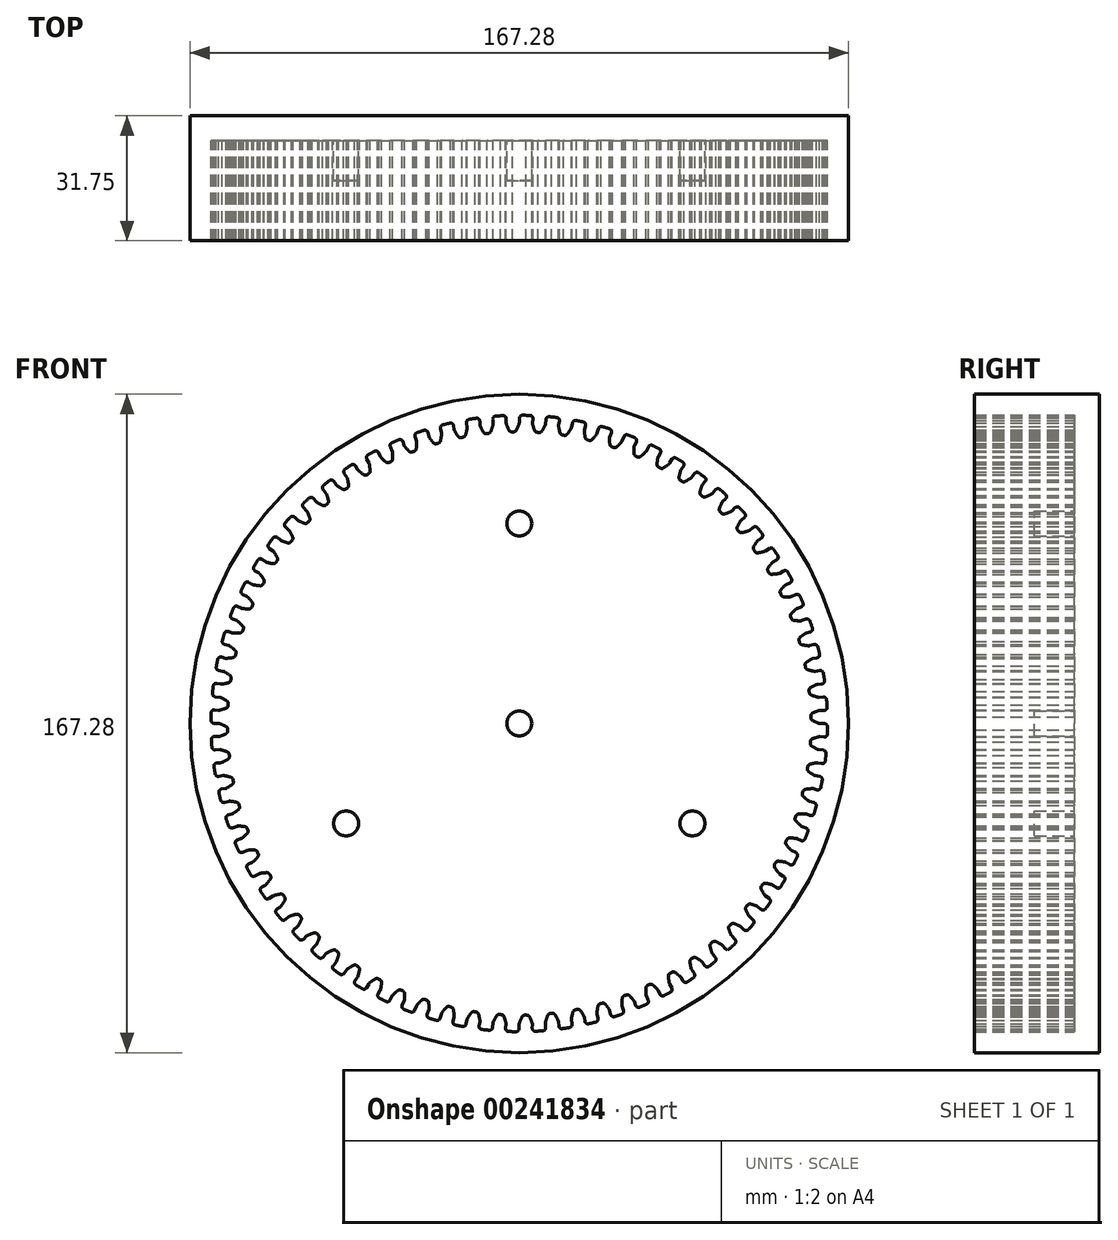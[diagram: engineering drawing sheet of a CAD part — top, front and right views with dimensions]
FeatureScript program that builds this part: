
annotation { "Feature Type Name" : "Feature", "Feature Type Description" : "" }
export const myFeature = defineFeature(function(context is Context, id is Id, definition is map)
    precondition{}
    {
        {
            var Q0;
            Q0=qCreatedBy(makeId("Front.planeOp"),FACE);
            var sketch = newSketch(context, id + "F0", { "sketchPlane" : qUnion([Q0])});
            skArc(sketch, "E0", {"start": v(-4.13, 78.2) * mm, "mid": v(-5.07, 78.15) * mm, "end": v(-6, 78.09) * mm});
            skLineSegment(sketch, "E1.MirrorCS", {"start": v(-3.32, 76.41) * mm, "end": v(-3.3, 77.4) * mm});
            skArc(sketch, "E2.MirrorCS", {"start": v(-3.28, 76.14) * mm, "mid": v(-2.99, 75.35) * mm, "end": v(-2.66, 74.57) * mm});
            skLineSegment(sketch, "E3.MirrorCS", {"start": v(-1.97, 74.1) * mm, "end": v(-1.7, 74.09) * mm});
            skLineSegment(sketch, "E4.MirrorCS", {"start": v(-1.44, 74.09) * mm, "end": v(-1.7, 74.09) * mm});
            skArc(sketch, "E5.MirrorCS", {"start": v(-0.05, 76.07) * mm, "mid": v(-0.38, 75.29) * mm, "end": v(-0.74, 74.52) * mm});
            skLineSegment(sketch, "E6.MirrorCS", {"start": v(0, 76.34) * mm, "end": v(0.03, 77.54) * mm});
            skPoint(sketch, "E7.visualSharp", {"position": v(-0.96, 74.09) * mm});
            skArc(sketch, "E7.filletArc", {"start": v(-1.44, 74.09) * mm, "mid": v(-1.03, 74.2) * mm, "end": v(-0.74, 74.52) * mm});
            skPoint(sketch, "E8.visualSharp", {"position": v(0, 76.2) * mm});
            skArc(sketch, "E8.filletArc", {"start": v(-0.05, 76.07) * mm, "mid": v(-0.01, 76.2) * mm, "end": v(0, 76.34) * mm});
            skPoint(sketch, "E9.visualSharp", {"position": v(-2.45, 74.12) * mm});
            skArc(sketch, "E9.filletArc", {"start": v(-2.66, 74.57) * mm, "mid": v(-2.38, 74.24) * mm, "end": v(-1.97, 74.1) * mm});
            skPoint(sketch, "E10.visualSharp", {"position": v(-3.32, 76.27) * mm});
            skArc(sketch, "E10.filletArc", {"start": v(-3.32, 76.41) * mm, "mid": v(-3.31, 76.27) * mm, "end": v(-3.28, 76.14) * mm});
            skPoint(sketch, "E11.visualSharp", {"position": v(0.05, 78.32) * mm});
            skArc(sketch, "E11.filletArc", {"start": v(0.82, 78.31) * mm, "mid": v(0.27, 78.1) * mm, "end": v(0.03, 77.54) * mm});
            skPoint(sketch, "E12.visualSharp", {"position": v(-3.28, 78.25) * mm});
            skArc(sketch, "E12.filletArc", {"start": v(-3.3, 77.4) * mm, "mid": v(-3.54, 77.99) * mm, "end": v(-4.13, 78.2) * mm});
            skArc(sketch, "E13.1.0", {"start": v(-6, 78.09) * mm, "mid": v(-6.54, 77.82) * mm, "end": v(-6.73, 77.25) * mm});
            skArc(sketch, "E13.1.1", {"start": v(-6.68, 75.77) * mm, "mid": v(-6.94, 74.97) * mm, "end": v(-7.23, 74.18) * mm});
            skLineSegment(sketch, "E13.1.2", {"start": v(-6.65, 76.05) * mm, "end": v(-6.73, 77.25) * mm});
            skArc(sketch, "E13.1.3", {"start": v(-6.68, 75.77) * mm, "mid": v(-6.65, 75.9) * mm, "end": v(-6.65, 76.05) * mm});
            skArc(sketch, "E13.1.4", {"start": v(-7.9, 73.68) * mm, "mid": v(-7.5, 73.83) * mm, "end": v(-7.23, 74.18) * mm});
            skLineSegment(sketch, "E13.1.5", {"start": v(-7.9, 73.68) * mm, "end": v(-8.16, 73.66) * mm});
            skLineSegment(sketch, "E13.1.6", {"start": v(-8.43, 73.65) * mm, "end": v(-8.16, 73.66) * mm});
            skArc(sketch, "E13.1.7", {"start": v(-9.15, 74.05) * mm, "mid": v(-8.84, 73.75) * mm, "end": v(-8.43, 73.65) * mm});
            skArc(sketch, "E13.1.8", {"start": v(-9.9, 75.56) * mm, "mid": v(-9.54, 74.8) * mm, "end": v(-9.15, 74.05) * mm});
            skArc(sketch, "E13.1.9", {"start": v(-9.97, 75.83) * mm, "mid": v(-9.95, 75.7) * mm, "end": v(-9.9, 75.56) * mm});
            skLineSegment(sketch, "E13.1.10", {"start": v(-9.97, 75.83) * mm, "end": v(-10.03, 76.82) * mm});
            skArc(sketch, "E13.1.11", {"start": v(-10.03, 76.82) * mm, "mid": v(-10.32, 77.38) * mm, "end": v(-10.93, 77.55) * mm});
            skArc(sketch, "E13.2.0", {"start": v(-12.79, 77.27) * mm, "mid": v(-13.3, 76.95) * mm, "end": v(-13.44, 76.37) * mm});
            skArc(sketch, "E13.2.1", {"start": v(-13.26, 74.9) * mm, "mid": v(-13.45, 74.08) * mm, "end": v(-13.67, 73.26) * mm});
            skLineSegment(sketch, "E13.2.2", {"start": v(-13.25, 75.18) * mm, "end": v(-13.44, 76.37) * mm});
            skArc(sketch, "E13.2.3", {"start": v(-13.26, 74.9) * mm, "mid": v(-13.24, 75.04) * mm, "end": v(-13.25, 75.18) * mm});
            skArc(sketch, "E13.2.4", {"start": v(-14.29, 72.71) * mm, "mid": v(-13.9, 72.9) * mm, "end": v(-13.67, 73.26) * mm});
            skLineSegment(sketch, "E13.2.5", {"start": v(-14.29, 72.71) * mm, "end": v(-14.55, 72.67) * mm});
            skLineSegment(sketch, "E13.2.6", {"start": v(-14.81, 72.63) * mm, "end": v(-14.55, 72.67) * mm});
            skArc(sketch, "E13.2.7", {"start": v(-15.57, 72.97) * mm, "mid": v(-15.24, 72.7) * mm, "end": v(-14.81, 72.63) * mm});
            skArc(sketch, "E13.2.8", {"start": v(-16.45, 74.41) * mm, "mid": v(-16.02, 73.68) * mm, "end": v(-15.57, 72.97) * mm});
            skArc(sketch, "E13.2.9", {"start": v(-16.54, 74.67) * mm, "mid": v(-16.5, 74.54) * mm, "end": v(-16.45, 74.41) * mm});
            skLineSegment(sketch, "E13.2.10", {"start": v(-16.54, 74.67) * mm, "end": v(-16.7, 75.66) * mm});
            skArc(sketch, "E13.2.11", {"start": v(-16.7, 75.66) * mm, "mid": v(-17.03, 76.19) * mm, "end": v(-17.65, 76.3) * mm});
            skArc(sketch, "E13.3.0", {"start": v(-19.47, 75.86) * mm, "mid": v(-19.95, 75.5) * mm, "end": v(-20.04, 74.9) * mm});
            skArc(sketch, "E13.3.1", {"start": v(-19.74, 73.46) * mm, "mid": v(-19.85, 72.63) * mm, "end": v(-20, 71.8) * mm});
            skLineSegment(sketch, "E13.3.2", {"start": v(-19.76, 73.74) * mm, "end": v(-20.04, 74.9) * mm});
            skArc(sketch, "E13.3.3", {"start": v(-19.74, 73.46) * mm, "mid": v(-19.73, 73.6) * mm, "end": v(-19.76, 73.74) * mm});
            skArc(sketch, "E13.3.4", {"start": v(-20.57, 71.2) * mm, "mid": v(-20.2, 71.41) * mm, "end": v(-20, 71.8) * mm});
            skLineSegment(sketch, "E13.3.5", {"start": v(-20.57, 71.2) * mm, "end": v(-20.83, 71.12) * mm});
            skLineSegment(sketch, "E13.3.6", {"start": v(-21.09, 71.06) * mm, "end": v(-20.83, 71.12) * mm});
            skArc(sketch, "E13.3.7", {"start": v(-21.87, 71.34) * mm, "mid": v(-21.52, 71.1) * mm, "end": v(-21.09, 71.06) * mm});
            skArc(sketch, "E13.3.8", {"start": v(-22.87, 72.7) * mm, "mid": v(-22.39, 72) * mm, "end": v(-21.87, 71.34) * mm});
            skArc(sketch, "E13.3.9", {"start": v(-22.98, 72.95) * mm, "mid": v(-22.94, 72.82) * mm, "end": v(-22.87, 72.7) * mm});
            skLineSegment(sketch, "E13.3.10", {"start": v(-22.98, 72.95) * mm, "end": v(-23.22, 73.91) * mm});
            skArc(sketch, "E13.3.11", {"start": v(-23.22, 73.91) * mm, "mid": v(-23.6, 74.41) * mm, "end": v(-24.23, 74.47) * mm});
            skArc(sketch, "E13.4.0", {"start": v(-26, 73.87) * mm, "mid": v(-26.46, 73.47) * mm, "end": v(-26.5, 72.88) * mm});
            skArc(sketch, "E13.4.1", {"start": v(-26.07, 71.46) * mm, "mid": v(-26.1, 70.62) * mm, "end": v(-26.18, 69.78) * mm});
            skLineSegment(sketch, "E13.4.2", {"start": v(-26.1, 71.74) * mm, "end": v(-26.5, 72.88) * mm});
            skArc(sketch, "E13.4.3", {"start": v(-26.07, 71.46) * mm, "mid": v(-26.07, 71.6) * mm, "end": v(-26.1, 71.74) * mm});
            skArc(sketch, "E13.4.4", {"start": v(-26.7, 69.13) * mm, "mid": v(-26.35, 69.38) * mm, "end": v(-26.18, 69.78) * mm});
            skLineSegment(sketch, "E13.4.5", {"start": v(-26.7, 69.13) * mm, "end": v(-26.95, 69.04) * mm});
            skLineSegment(sketch, "E13.4.6", {"start": v(-27.2, 68.96) * mm, "end": v(-26.95, 69.04) * mm});
            skArc(sketch, "E13.4.7", {"start": v(-28, 69.16) * mm, "mid": v(-27.63, 68.94) * mm, "end": v(-27.2, 68.96) * mm});
            skArc(sketch, "E13.4.8", {"start": v(-29.12, 70.43) * mm, "mid": v(-28.58, 69.78) * mm, "end": v(-28, 69.16) * mm});
            skArc(sketch, "E13.4.9", {"start": v(-29.25, 70.67) * mm, "mid": v(-29.2, 70.54) * mm, "end": v(-29.12, 70.43) * mm});
            skLineSegment(sketch, "E13.4.10", {"start": v(-29.25, 70.67) * mm, "end": v(-29.57, 71.6) * mm});
            skArc(sketch, "E13.4.11", {"start": v(-29.57, 71.6) * mm, "mid": v(-30, 72.07) * mm, "end": v(-30.63, 72.08) * mm});
            skArc(sketch, "E13.5.0", {"start": v(-32.35, 71.32) * mm, "mid": v(-32.76, 70.89) * mm, "end": v(-32.74, 70.29) * mm});
            skArc(sketch, "E13.5.1", {"start": v(-32.2, 68.92) * mm, "mid": v(-32.16, 68.08) * mm, "end": v(-32.16, 67.23) * mm});
            skLineSegment(sketch, "E13.5.2", {"start": v(-32.26, 69.19) * mm, "end": v(-32.74, 70.29) * mm});
            skArc(sketch, "E13.5.3", {"start": v(-32.2, 68.92) * mm, "mid": v(-32.21, 69.06) * mm, "end": v(-32.26, 69.19) * mm});
            skArc(sketch, "E13.5.4", {"start": v(-32.62, 66.54) * mm, "mid": v(-32.3, 66.82) * mm, "end": v(-32.16, 67.23) * mm});
            skLineSegment(sketch, "E13.5.5", {"start": v(-32.62, 66.54) * mm, "end": v(-32.86, 66.43) * mm});
            skLineSegment(sketch, "E13.5.6", {"start": v(-33.1, 66.32) * mm, "end": v(-32.86, 66.43) * mm});
            skArc(sketch, "E13.5.7", {"start": v(-33.92, 66.46) * mm, "mid": v(-33.53, 66.27) * mm, "end": v(-33.1, 66.32) * mm});
            skArc(sketch, "E13.5.8", {"start": v(-35.15, 67.62) * mm, "mid": v(-34.55, 67.02) * mm, "end": v(-33.92, 66.46) * mm});
            skArc(sketch, "E13.5.9", {"start": v(-35.3, 67.85) * mm, "mid": v(-35.24, 67.73) * mm, "end": v(-35.15, 67.62) * mm});
            skLineSegment(sketch, "E13.5.10", {"start": v(-35.3, 67.85) * mm, "end": v(-35.7, 68.76) * mm});
            skArc(sketch, "E13.5.11", {"start": v(-35.7, 68.76) * mm, "mid": v(-36.17, 69.18) * mm, "end": v(-36.8, 69.14) * mm});
            skArc(sketch, "E13.6.0", {"start": v(-38.44, 68.23) * mm, "mid": v(-38.81, 67.76) * mm, "end": v(-38.75, 67.17) * mm});
            skArc(sketch, "E13.6.1", {"start": v(-38.08, 65.85) * mm, "mid": v(-37.97, 65.01) * mm, "end": v(-37.9, 64.17) * mm});
            skLineSegment(sketch, "E13.6.2", {"start": v(-38.17, 66.11) * mm, "end": v(-38.75, 67.17) * mm});
            skArc(sketch, "E13.6.3", {"start": v(-38.08, 65.85) * mm, "mid": v(-38.11, 65.99) * mm, "end": v(-38.17, 66.11) * mm});
            skArc(sketch, "E13.6.4", {"start": v(-38.3, 63.44) * mm, "mid": v(-38, 63.75) * mm, "end": v(-37.9, 64.17) * mm});
            skLineSegment(sketch, "E13.6.5", {"start": v(-38.3, 63.44) * mm, "end": v(-38.52, 63.3) * mm});
            skLineSegment(sketch, "E13.6.6", {"start": v(-38.76, 63.19) * mm, "end": v(-38.52, 63.3) * mm});
            skArc(sketch, "E13.6.7", {"start": v(-39.59, 63.25) * mm, "mid": v(-39.18, 63.1) * mm, "end": v(-38.76, 63.19) * mm});
            skArc(sketch, "E13.6.8", {"start": v(-40.9, 64.3) * mm, "mid": v(-40.26, 63.76) * mm, "end": v(-39.59, 63.25) * mm});
            skArc(sketch, "E13.6.9", {"start": v(-41.08, 64.51) * mm, "mid": v(-41, 64.4) * mm, "end": v(-40.9, 64.3) * mm});
            skLineSegment(sketch, "E13.6.10", {"start": v(-41.08, 64.51) * mm, "end": v(-41.56, 65.38) * mm});
            skArc(sketch, "E13.6.11", {"start": v(-41.56, 65.38) * mm, "mid": v(-42.06, 65.77) * mm, "end": v(-42.68, 65.67) * mm});
            skArc(sketch, "E13.7.0", {"start": v(-44.24, 64.62) * mm, "mid": v(-44.57, 64.12) * mm, "end": v(-44.45, 63.54) * mm});
            skArc(sketch, "E13.7.1", {"start": v(-43.67, 62.28) * mm, "mid": v(-43.5, 61.46) * mm, "end": v(-43.35, 60.62) * mm});
            skLineSegment(sketch, "E13.7.2", {"start": v(-43.78, 62.53) * mm, "end": v(-44.45, 63.54) * mm});
            skArc(sketch, "E13.7.3", {"start": v(-43.67, 62.28) * mm, "mid": v(-43.72, 62.41) * mm, "end": v(-43.78, 62.53) * mm});
            skArc(sketch, "E13.7.4", {"start": v(-43.68, 59.86) * mm, "mid": v(-43.4, 60.2) * mm, "end": v(-43.35, 60.62) * mm});
            skLineSegment(sketch, "E13.7.5", {"start": v(-43.68, 59.86) * mm, "end": v(-43.9, 59.71) * mm});
            skLineSegment(sketch, "E13.7.6", {"start": v(-44.12, 59.57) * mm, "end": v(-43.9, 59.71) * mm});
            skArc(sketch, "E13.7.7", {"start": v(-44.95, 59.56) * mm, "mid": v(-44.53, 59.44) * mm, "end": v(-44.12, 59.57) * mm});
            skArc(sketch, "E13.7.8", {"start": v(-46.36, 60.49) * mm, "mid": v(-45.66, 60) * mm, "end": v(-44.95, 59.56) * mm});
            skArc(sketch, "E13.7.9", {"start": v(-46.55, 60.69) * mm, "mid": v(-46.46, 60.58) * mm, "end": v(-46.36, 60.49) * mm});
            skLineSegment(sketch, "E13.7.10", {"start": v(-46.55, 60.69) * mm, "end": v(-47.1, 61.51) * mm});
            skArc(sketch, "E13.7.11", {"start": v(-47.1, 61.51) * mm, "mid": v(-47.63, 61.85) * mm, "end": v(-48.24, 61.7) * mm});
            skArc(sketch, "E13.8.0", {"start": v(-49.7, 60.52) * mm, "mid": v(-49.99, 60) * mm, "end": v(-49.82, 59.42) * mm});
            skArc(sketch, "E13.8.1", {"start": v(-48.93, 58.24) * mm, "mid": v(-48.68, 57.43) * mm, "end": v(-48.47, 56.61) * mm});
            skLineSegment(sketch, "E13.8.2", {"start": v(-49.07, 58.48) * mm, "end": v(-49.82, 59.42) * mm});
            skArc(sketch, "E13.8.3", {"start": v(-48.93, 58.24) * mm, "mid": v(-49, 58.37) * mm, "end": v(-49.07, 58.48) * mm});
            skArc(sketch, "E13.8.4", {"start": v(-48.73, 55.83) * mm, "mid": v(-48.49, 56.18) * mm, "end": v(-48.47, 56.61) * mm});
            skLineSegment(sketch, "E13.8.5", {"start": v(-48.73, 55.83) * mm, "end": v(-48.93, 55.66) * mm});
            skLineSegment(sketch, "E13.8.6", {"start": v(-49.14, 55.5) * mm, "end": v(-48.93, 55.66) * mm});
            skArc(sketch, "E13.8.7", {"start": v(-49.97, 55.41) * mm, "mid": v(-49.54, 55.34) * mm, "end": v(-49.14, 55.5) * mm});
            skArc(sketch, "E13.8.8", {"start": v(-51.45, 56.22) * mm, "mid": v(-50.72, 55.8) * mm, "end": v(-49.97, 55.41) * mm});
            skArc(sketch, "E13.8.9", {"start": v(-51.66, 56.4) * mm, "mid": v(-51.56, 56.3) * mm, "end": v(-51.45, 56.22) * mm});
            skLineSegment(sketch, "E13.8.10", {"start": v(-51.66, 56.4) * mm, "end": v(-52.28, 57.17) * mm});
            skArc(sketch, "E13.8.11", {"start": v(-52.28, 57.17) * mm, "mid": v(-52.84, 57.47) * mm, "end": v(-53.43, 57.26) * mm});
            skArc(sketch, "E13.9.0", {"start": v(-54.8, 55.96) * mm, "mid": v(-55.03, 55.4) * mm, "end": v(-54.8, 54.85) * mm});
            skArc(sketch, "E13.9.1", {"start": v(-53.82, 53.75) * mm, "mid": v(-53.5, 52.97) * mm, "end": v(-53.22, 52.17) * mm});
            skLineSegment(sketch, "E13.9.2", {"start": v(-53.98, 53.98) * mm, "end": v(-54.8, 54.85) * mm});
            skArc(sketch, "E13.9.3", {"start": v(-53.82, 53.75) * mm, "mid": v(-53.9, 53.87) * mm, "end": v(-53.98, 53.98) * mm});
            skArc(sketch, "E13.9.4", {"start": v(-53.4, 51.37) * mm, "mid": v(-53.2, 51.74) * mm, "end": v(-53.22, 52.17) * mm});
            skLineSegment(sketch, "E13.9.5", {"start": v(-53.4, 51.37) * mm, "end": v(-53.6, 51.18) * mm});
            skLineSegment(sketch, "E13.9.6", {"start": v(-53.8, 51) * mm, "end": v(-53.6, 51.18) * mm});
            skArc(sketch, "E13.9.7", {"start": v(-54.6, 50.85) * mm, "mid": v(-54.18, 50.8) * mm, "end": v(-53.8, 51) * mm});
            skArc(sketch, "E13.9.8", {"start": v(-56.16, 51.52) * mm, "mid": v(-55.39, 51.17) * mm, "end": v(-54.6, 50.85) * mm});
            skArc(sketch, "E13.9.9", {"start": v(-56.38, 51.68) * mm, "mid": v(-56.27, 51.6) * mm, "end": v(-56.16, 51.52) * mm});
            skLineSegment(sketch, "E13.9.10", {"start": v(-56.38, 51.68) * mm, "end": v(-57.07, 52.4) * mm});
            skArc(sketch, "E13.9.11", {"start": v(-57.07, 52.4) * mm, "mid": v(-57.65, 52.64) * mm, "end": v(-58.22, 52.38) * mm});
            skArc(sketch, "E13.10.0", {"start": v(-59.46, 50.97) * mm, "mid": v(-59.65, 50.4) * mm, "end": v(-59.38, 49.87) * mm});
            skArc(sketch, "E13.10.1", {"start": v(-58.3, 48.86) * mm, "mid": v(-57.92, 48.1) * mm, "end": v(-57.56, 47.34) * mm});
            skLineSegment(sketch, "E13.10.2", {"start": v(-58.48, 49.07) * mm, "end": v(-59.38, 49.87) * mm});
            skArc(sketch, "E13.10.3", {"start": v(-58.3, 48.86) * mm, "mid": v(-58.38, 48.97) * mm, "end": v(-58.48, 49.07) * mm});
            skArc(sketch, "E13.10.4", {"start": v(-57.68, 46.52) * mm, "mid": v(-57.5, 46.91) * mm, "end": v(-57.56, 47.34) * mm});
            skLineSegment(sketch, "E13.10.5", {"start": v(-57.68, 46.52) * mm, "end": v(-57.85, 46.31) * mm});
            skLineSegment(sketch, "E13.10.6", {"start": v(-58.03, 46.12) * mm, "end": v(-57.85, 46.31) * mm});
            skArc(sketch, "E13.10.7", {"start": v(-58.83, 45.9) * mm, "mid": v(-58.4, 45.9) * mm, "end": v(-58.03, 46.12) * mm});
            skArc(sketch, "E13.10.8", {"start": v(-60.43, 46.43) * mm, "mid": v(-59.64, 46.14) * mm, "end": v(-58.83, 45.9) * mm});
            skArc(sketch, "E13.10.9", {"start": v(-60.67, 46.57) * mm, "mid": v(-60.56, 46.5) * mm, "end": v(-60.43, 46.43) * mm});
            skLineSegment(sketch, "E13.10.10", {"start": v(-60.67, 46.57) * mm, "end": v(-61.42, 47.23) * mm});
            skArc(sketch, "E13.10.11", {"start": v(-61.42, 47.23) * mm, "mid": v(-62.02, 47.42) * mm, "end": v(-62.56, 47.1) * mm});
            skArc(sketch, "E13.11.0", {"start": v(-63.68, 45.6) * mm, "mid": v(-63.81, 45.01) * mm, "end": v(-63.5, 44.5) * mm});
            skArc(sketch, "E13.11.1", {"start": v(-62.34, 43.59) * mm, "mid": v(-61.89, 42.87) * mm, "end": v(-61.47, 42.14) * mm});
            skLineSegment(sketch, "E13.11.2", {"start": v(-62.53, 43.79) * mm, "end": v(-63.5, 44.5) * mm});
            skArc(sketch, "E13.11.3", {"start": v(-62.34, 43.59) * mm, "mid": v(-62.43, 43.7) * mm, "end": v(-62.53, 43.79) * mm});
            skArc(sketch, "E13.11.4", {"start": v(-61.52, 41.31) * mm, "mid": v(-61.38, 41.72) * mm, "end": v(-61.47, 42.14) * mm});
            skLineSegment(sketch, "E13.11.5", {"start": v(-61.52, 41.31) * mm, "end": v(-61.67, 41.1) * mm});
            skLineSegment(sketch, "E13.11.6", {"start": v(-61.83, 40.89) * mm, "end": v(-61.67, 41.1) * mm});
            skArc(sketch, "E13.11.7", {"start": v(-62.6, 40.6) * mm, "mid": v(-62.18, 40.63) * mm, "end": v(-61.83, 40.89) * mm});
            skArc(sketch, "E13.11.8", {"start": v(-64.25, 40.99) * mm, "mid": v(-63.43, 40.77) * mm, "end": v(-62.6, 40.6) * mm});
            skArc(sketch, "E13.11.9", {"start": v(-64.5, 41.1) * mm, "mid": v(-64.38, 41.04) * mm, "end": v(-64.25, 40.99) * mm});
            skLineSegment(sketch, "E13.11.10", {"start": v(-64.5, 41.1) * mm, "end": v(-65.3, 41.7) * mm});
            skArc(sketch, "E13.11.11", {"start": v(-65.3, 41.7) * mm, "mid": v(-65.91, 41.83) * mm, "end": v(-66.43, 41.48) * mm});
            skArc(sketch, "E13.12.0", {"start": v(-67.4, 39.87) * mm, "mid": v(-67.5, 39.28) * mm, "end": v(-67.14, 38.8) * mm});
            skArc(sketch, "E13.12.1", {"start": v(-65.9, 37.99) * mm, "mid": v(-65.4, 37.32) * mm, "end": v(-64.9, 36.62) * mm});
            skLineSegment(sketch, "E13.12.2", {"start": v(-66.1, 38.17) * mm, "end": v(-67.14, 38.8) * mm});
            skArc(sketch, "E13.12.3", {"start": v(-65.9, 37.99) * mm, "mid": v(-66, 38.09) * mm, "end": v(-66.1, 38.17) * mm});
            skArc(sketch, "E13.12.4", {"start": v(-64.88, 35.8) * mm, "mid": v(-64.78, 36.21) * mm, "end": v(-64.9, 36.62) * mm});
            skLineSegment(sketch, "E13.12.5", {"start": v(-64.88, 35.8) * mm, "end": v(-65.02, 35.56) * mm});
            skLineSegment(sketch, "E13.12.6", {"start": v(-65.16, 35.34) * mm, "end": v(-65.02, 35.56) * mm});
            skArc(sketch, "E13.12.7", {"start": v(-65.9, 34.98) * mm, "mid": v(-65.48, 35.05) * mm, "end": v(-65.16, 35.34) * mm});
            skArc(sketch, "E13.12.8", {"start": v(-67.58, 35.23) * mm, "mid": v(-66.74, 35.09) * mm, "end": v(-65.9, 34.98) * mm});
            skArc(sketch, "E13.12.9", {"start": v(-67.83, 35.33) * mm, "mid": v(-67.71, 35.27) * mm, "end": v(-67.58, 35.23) * mm});
            skLineSegment(sketch, "E13.12.10", {"start": v(-67.83, 35.33) * mm, "end": v(-68.68, 35.85) * mm});
            skArc(sketch, "E13.12.11", {"start": v(-68.68, 35.85) * mm, "mid": v(-69.3, 35.93) * mm, "end": v(-69.8, 35.53) * mm});
            skArc(sketch, "E13.13.0", {"start": v(-70.63, 33.84) * mm, "mid": v(-70.66, 33.25) * mm, "end": v(-70.26, 32.8) * mm});
            skArc(sketch, "E13.13.1", {"start": v(-68.96, 32.1) * mm, "mid": v(-68.4, 31.48) * mm, "end": v(-67.85, 30.83) * mm});
            skLineSegment(sketch, "E13.13.2", {"start": v(-69.19, 32.26) * mm, "end": v(-70.26, 32.8) * mm});
            skArc(sketch, "E13.13.3", {"start": v(-68.96, 32.1) * mm, "mid": v(-69.07, 32.2) * mm, "end": v(-69.19, 32.26) * mm});
            skArc(sketch, "E13.13.4", {"start": v(-67.76, 30) * mm, "mid": v(-67.69, 30.43) * mm, "end": v(-67.85, 30.83) * mm});
            skLineSegment(sketch, "E13.13.5", {"start": v(-67.76, 30) * mm, "end": v(-67.87, 29.76) * mm});
            skLineSegment(sketch, "E13.13.6", {"start": v(-68, 29.53) * mm, "end": v(-67.87, 29.76) * mm});
            skArc(sketch, "E13.13.7", {"start": v(-68.7, 29.1) * mm, "mid": v(-68.29, 29.21) * mm, "end": v(-68, 29.53) * mm});
            skArc(sketch, "E13.13.8", {"start": v(-70.4, 29.2) * mm, "mid": v(-69.55, 29.14) * mm, "end": v(-68.7, 29.1) * mm});
            skArc(sketch, "E13.13.9", {"start": v(-70.66, 29.28) * mm, "mid": v(-70.53, 29.23) * mm, "end": v(-70.4, 29.2) * mm});
            skLineSegment(sketch, "E13.13.10", {"start": v(-70.66, 29.28) * mm, "end": v(-71.55, 29.72) * mm});
            skArc(sketch, "E13.13.11", {"start": v(-71.55, 29.72) * mm, "mid": v(-72.18, 29.75) * mm, "end": v(-72.62, 29.31) * mm});
            skArc(sketch, "E13.14.0", {"start": v(-73.3, 27.56) * mm, "mid": v(-73.29, 26.96) * mm, "end": v(-72.86, 26.55) * mm});
            skArc(sketch, "E13.14.1", {"start": v(-71.5, 25.97) * mm, "mid": v(-70.88, 25.4) * mm, "end": v(-70.28, 24.8) * mm});
            skLineSegment(sketch, "E13.14.2", {"start": v(-71.73, 26.11) * mm, "end": v(-72.86, 26.55) * mm});
            skArc(sketch, "E13.14.3", {"start": v(-71.5, 25.97) * mm, "mid": v(-71.6, 26.05) * mm, "end": v(-71.73, 26.11) * mm});
            skArc(sketch, "E13.14.4", {"start": v(-70.11, 23.98) * mm, "mid": v(-70.08, 24.41) * mm, "end": v(-70.28, 24.8) * mm});
            skLineSegment(sketch, "E13.14.5", {"start": v(-70.11, 23.98) * mm, "end": v(-70.2, 23.73) * mm});
            skLineSegment(sketch, "E13.14.6", {"start": v(-70.3, 23.49) * mm, "end": v(-70.2, 23.73) * mm});
            skArc(sketch, "E13.14.7", {"start": v(-70.98, 23) * mm, "mid": v(-70.57, 23.15) * mm, "end": v(-70.3, 23.49) * mm});
            skArc(sketch, "E13.14.8", {"start": v(-72.67, 22.96) * mm, "mid": v(-71.82, 22.96) * mm, "end": v(-70.98, 23) * mm});
            skArc(sketch, "E13.14.9", {"start": v(-72.94, 23.01) * mm, "mid": v(-72.8, 22.98) * mm, "end": v(-72.67, 22.96) * mm});
            skLineSegment(sketch, "E13.14.10", {"start": v(-72.94, 23.01) * mm, "end": v(-73.86, 23.37) * mm});
            skArc(sketch, "E13.14.11", {"start": v(-73.86, 23.37) * mm, "mid": v(-74.5, 23.35) * mm, "end": v(-74.9, 22.87) * mm});
            skArc(sketch, "E13.15.0", {"start": v(-75.43, 21.07) * mm, "mid": v(-75.36, 20.47) * mm, "end": v(-74.9, 20.1) * mm});
            skArc(sketch, "E13.15.1", {"start": v(-73.49, 19.64) * mm, "mid": v(-72.82, 19.12) * mm, "end": v(-72.18, 18.58) * mm});
            skLineSegment(sketch, "E13.15.2", {"start": v(-73.74, 19.76) * mm, "end": v(-74.9, 20.1) * mm});
            skArc(sketch, "E13.15.3", {"start": v(-73.49, 19.64) * mm, "mid": v(-73.6, 19.71) * mm, "end": v(-73.74, 19.76) * mm});
            skArc(sketch, "E13.15.4", {"start": v(-71.94, 17.78) * mm, "mid": v(-71.94, 18.21) * mm, "end": v(-72.18, 18.58) * mm});
            skLineSegment(sketch, "E13.15.5", {"start": v(-71.94, 17.78) * mm, "end": v(-72, 17.53) * mm});
            skLineSegment(sketch, "E13.15.6", {"start": v(-72.09, 17.27) * mm, "end": v(-72, 17.53) * mm});
            skArc(sketch, "E13.15.7", {"start": v(-72.71, 16.73) * mm, "mid": v(-72.32, 16.91) * mm, "end": v(-72.09, 17.27) * mm});
            skArc(sketch, "E13.15.8", {"start": v(-74.4, 16.54) * mm, "mid": v(-73.55, 16.62) * mm, "end": v(-72.71, 16.73) * mm});
            skArc(sketch, "E13.15.9", {"start": v(-74.67, 16.57) * mm, "mid": v(-74.53, 16.54) * mm, "end": v(-74.4, 16.54) * mm});
            skLineSegment(sketch, "E13.15.10", {"start": v(-74.67, 16.57) * mm, "end": v(-75.62, 16.85) * mm});
            skArc(sketch, "E13.15.11", {"start": v(-75.62, 16.85) * mm, "mid": v(-76.25, 16.77) * mm, "end": v(-76.61, 16.25) * mm});
            skArc(sketch, "E13.16.0", {"start": v(-76.98, 14.41) * mm, "mid": v(-76.86, 13.83) * mm, "end": v(-76.36, 13.5) * mm});
            skArc(sketch, "E13.16.1", {"start": v(-74.92, 13.16) * mm, "mid": v(-74.21, 12.7) * mm, "end": v(-73.52, 12.21) * mm});
            skLineSegment(sketch, "E13.16.2", {"start": v(-75.18, 13.26) * mm, "end": v(-76.36, 13.5) * mm});
            skArc(sketch, "E13.16.3", {"start": v(-74.92, 13.16) * mm, "mid": v(-75.05, 13.22) * mm, "end": v(-75.18, 13.26) * mm});
            skArc(sketch, "E13.16.4", {"start": v(-73.21, 11.44) * mm, "mid": v(-73.26, 11.87) * mm, "end": v(-73.52, 12.21) * mm});
            skLineSegment(sketch, "E13.16.5", {"start": v(-73.21, 11.44) * mm, "end": v(-73.26, 11.18) * mm});
            skLineSegment(sketch, "E13.16.6", {"start": v(-73.32, 10.92) * mm, "end": v(-73.26, 11.18) * mm});
            skArc(sketch, "E13.16.7", {"start": v(-73.9, 10.33) * mm, "mid": v(-73.52, 10.54) * mm, "end": v(-73.32, 10.92) * mm});
            skArc(sketch, "E13.16.8", {"start": v(-75.55, 10) * mm, "mid": v(-74.72, 10.14) * mm, "end": v(-73.9, 10.33) * mm});
            skArc(sketch, "E13.16.9", {"start": v(-75.83, 10) * mm, "mid": v(-75.69, 9.98) * mm, "end": v(-75.55, 10) * mm});
            skLineSegment(sketch, "E13.16.10", {"start": v(-75.83, 10) * mm, "end": v(-76.8, 10.2) * mm});
            skArc(sketch, "E13.16.11", {"start": v(-76.8, 10.2) * mm, "mid": v(-77.42, 10.06) * mm, "end": v(-77.74, 9.52) * mm});
            skArc(sketch, "E13.17.0", {"start": v(-77.94, 7.65) * mm, "mid": v(-77.77, 7.07) * mm, "end": v(-77.24, 6.79) * mm});
            skArc(sketch, "E13.17.1", {"start": v(-75.78, 6.58) * mm, "mid": v(-75.04, 6.19) * mm, "end": v(-74.3, 5.76) * mm});
            skLineSegment(sketch, "E13.17.2", {"start": v(-76.05, 6.66) * mm, "end": v(-77.24, 6.79) * mm});
            skArc(sketch, "E13.17.3", {"start": v(-75.78, 6.58) * mm, "mid": v(-75.91, 6.63) * mm, "end": v(-76.05, 6.66) * mm});
            skArc(sketch, "E13.17.4", {"start": v(-73.93, 5.02) * mm, "mid": v(-74.01, 5.44) * mm, "end": v(-74.3, 5.76) * mm});
            skLineSegment(sketch, "E13.17.5", {"start": v(-73.93, 5.02) * mm, "end": v(-73.96, 4.76) * mm});
            skLineSegment(sketch, "E13.17.6", {"start": v(-74, 4.5) * mm, "end": v(-73.96, 4.76) * mm});
            skArc(sketch, "E13.17.7", {"start": v(-74.51, 3.85) * mm, "mid": v(-74.16, 4.1) * mm, "end": v(-74, 4.5) * mm});
            skArc(sketch, "E13.17.8", {"start": v(-76.13, 3.37) * mm, "mid": v(-75.32, 3.6) * mm, "end": v(-74.51, 3.85) * mm});
            skArc(sketch, "E13.17.9", {"start": v(-76.4, 3.35) * mm, "mid": v(-76.27, 3.35) * mm, "end": v(-76.13, 3.37) * mm});
            skLineSegment(sketch, "E13.17.10", {"start": v(-76.4, 3.35) * mm, "end": v(-77.4, 3.46) * mm});
            skArc(sketch, "E13.17.11", {"start": v(-77.4, 3.46) * mm, "mid": v(-78, 3.27) * mm, "end": v(-78.27, 2.7) * mm});
            skArc(sketch, "E13.18.0", {"start": v(-78.31, 0.82) * mm, "mid": v(-78.1, 0.27) * mm, "end": v(-77.54, 0.03) * mm});
            skArc(sketch, "E13.18.1", {"start": v(-76.07, -0.05) * mm, "mid": v(-75.29, -0.38) * mm, "end": v(-74.52, -0.74) * mm});
            skLineSegment(sketch, "E13.18.2", {"start": v(-76.34, 0) * mm, "end": v(-77.54, 0.03) * mm});
            skArc(sketch, "E13.18.3", {"start": v(-76.07, -0.05) * mm, "mid": v(-76.2, -0.01) * mm, "end": v(-76.34, 0) * mm});
            skArc(sketch, "E13.18.4", {"start": v(-74.09, -1.44) * mm, "mid": v(-74.2, -1.03) * mm, "end": v(-74.52, -0.74) * mm});
            skLineSegment(sketch, "E13.18.5", {"start": v(-74.09, -1.44) * mm, "end": v(-74.09, -1.7) * mm});
            skLineSegment(sketch, "E13.18.6", {"start": v(-74.1, -1.97) * mm, "end": v(-74.09, -1.7) * mm});
            skArc(sketch, "E13.18.7", {"start": v(-74.57, -2.66) * mm, "mid": v(-74.24, -2.38) * mm, "end": v(-74.1, -1.97) * mm});
            skArc(sketch, "E13.18.8", {"start": v(-76.14, -3.28) * mm, "mid": v(-75.35, -2.99) * mm, "end": v(-74.57, -2.66) * mm});
            skArc(sketch, "E13.18.9", {"start": v(-76.41, -3.32) * mm, "mid": v(-76.27, -3.31) * mm, "end": v(-76.14, -3.28) * mm});
            skLineSegment(sketch, "E13.18.10", {"start": v(-76.41, -3.32) * mm, "end": v(-77.4, -3.3) * mm});
            skArc(sketch, "E13.18.11", {"start": v(-77.4, -3.3) * mm, "mid": v(-77.99, -3.54) * mm, "end": v(-78.2, -4.13) * mm});
            skArc(sketch, "E13.19.0", {"start": v(-78.09, -6) * mm, "mid": v(-77.82, -6.54) * mm, "end": v(-77.25, -6.73) * mm});
            skArc(sketch, "E13.19.1", {"start": v(-75.77, -6.68) * mm, "mid": v(-74.97, -6.94) * mm, "end": v(-74.18, -7.23) * mm});
            skLineSegment(sketch, "E13.19.2", {"start": v(-76.05, -6.65) * mm, "end": v(-77.25, -6.73) * mm});
            skArc(sketch, "E13.19.3", {"start": v(-75.77, -6.68) * mm, "mid": v(-75.9, -6.65) * mm, "end": v(-76.05, -6.65) * mm});
            skArc(sketch, "E13.19.4", {"start": v(-73.68, -7.9) * mm, "mid": v(-73.83, -7.5) * mm, "end": v(-74.18, -7.23) * mm});
            skLineSegment(sketch, "E13.19.5", {"start": v(-73.68, -7.9) * mm, "end": v(-73.66, -8.16) * mm});
            skLineSegment(sketch, "E13.19.6", {"start": v(-73.65, -8.43) * mm, "end": v(-73.66, -8.16) * mm});
            skArc(sketch, "E13.19.7", {"start": v(-74.05, -9.15) * mm, "mid": v(-73.75, -8.84) * mm, "end": v(-73.65, -8.43) * mm});
            skArc(sketch, "E13.19.8", {"start": v(-75.56, -9.9) * mm, "mid": v(-74.8, -9.54) * mm, "end": v(-74.05, -9.15) * mm});
            skArc(sketch, "E13.19.9", {"start": v(-75.83, -9.97) * mm, "mid": v(-75.7, -9.95) * mm, "end": v(-75.56, -9.9) * mm});
            skLineSegment(sketch, "E13.19.10", {"start": v(-75.83, -9.97) * mm, "end": v(-76.82, -10.03) * mm});
            skArc(sketch, "E13.19.11", {"start": v(-76.82, -10.03) * mm, "mid": v(-77.38, -10.32) * mm, "end": v(-77.55, -10.93) * mm});
            skArc(sketch, "E13.20.0", {"start": v(-77.27, -12.79) * mm, "mid": v(-76.95, -13.3) * mm, "end": v(-76.37, -13.44) * mm});
            skArc(sketch, "E13.20.1", {"start": v(-74.9, -13.26) * mm, "mid": v(-74.08, -13.45) * mm, "end": v(-73.26, -13.67) * mm});
            skLineSegment(sketch, "E13.20.2", {"start": v(-75.18, -13.25) * mm, "end": v(-76.37, -13.44) * mm});
            skArc(sketch, "E13.20.3", {"start": v(-74.9, -13.26) * mm, "mid": v(-75.04, -13.24) * mm, "end": v(-75.18, -13.25) * mm});
            skArc(sketch, "E13.20.4", {"start": v(-72.71, -14.29) * mm, "mid": v(-72.9, -13.9) * mm, "end": v(-73.26, -13.67) * mm});
            skLineSegment(sketch, "E13.20.5", {"start": v(-72.71, -14.29) * mm, "end": v(-72.67, -14.55) * mm});
            skLineSegment(sketch, "E13.20.6", {"start": v(-72.63, -14.81) * mm, "end": v(-72.67, -14.55) * mm});
            skArc(sketch, "E13.20.7", {"start": v(-72.97, -15.57) * mm, "mid": v(-72.7, -15.24) * mm, "end": v(-72.63, -14.81) * mm});
            skArc(sketch, "E13.20.8", {"start": v(-74.41, -16.45) * mm, "mid": v(-73.68, -16.02) * mm, "end": v(-72.97, -15.57) * mm});
            skArc(sketch, "E13.20.9", {"start": v(-74.67, -16.54) * mm, "mid": v(-74.54, -16.5) * mm, "end": v(-74.41, -16.45) * mm});
            skLineSegment(sketch, "E13.20.10", {"start": v(-74.67, -16.54) * mm, "end": v(-75.66, -16.7) * mm});
            skArc(sketch, "E13.20.11", {"start": v(-75.66, -16.7) * mm, "mid": v(-76.19, -17.03) * mm, "end": v(-76.3, -17.65) * mm});
            skArc(sketch, "E13.21.0", {"start": v(-75.86, -19.47) * mm, "mid": v(-75.5, -19.95) * mm, "end": v(-74.9, -20.04) * mm});
            skArc(sketch, "E13.21.1", {"start": v(-73.46, -19.74) * mm, "mid": v(-72.63, -19.85) * mm, "end": v(-71.8, -20) * mm});
            skLineSegment(sketch, "E13.21.2", {"start": v(-73.74, -19.76) * mm, "end": v(-74.9, -20.04) * mm});
            skArc(sketch, "E13.21.3", {"start": v(-73.46, -19.74) * mm, "mid": v(-73.6, -19.73) * mm, "end": v(-73.74, -19.76) * mm});
            skArc(sketch, "E13.21.4", {"start": v(-71.2, -20.57) * mm, "mid": v(-71.41, -20.2) * mm, "end": v(-71.8, -20) * mm});
            skLineSegment(sketch, "E13.21.5", {"start": v(-71.2, -20.57) * mm, "end": v(-71.12, -20.83) * mm});
            skLineSegment(sketch, "E13.21.6", {"start": v(-71.06, -21.09) * mm, "end": v(-71.12, -20.83) * mm});
            skArc(sketch, "E13.21.7", {"start": v(-71.34, -21.87) * mm, "mid": v(-71.1, -21.52) * mm, "end": v(-71.06, -21.09) * mm});
            skArc(sketch, "E13.21.8", {"start": v(-72.7, -22.87) * mm, "mid": v(-72, -22.39) * mm, "end": v(-71.34, -21.87) * mm});
            skArc(sketch, "E13.21.9", {"start": v(-72.95, -22.98) * mm, "mid": v(-72.82, -22.94) * mm, "end": v(-72.7, -22.87) * mm});
            skLineSegment(sketch, "E13.21.10", {"start": v(-72.95, -22.98) * mm, "end": v(-73.91, -23.22) * mm});
            skArc(sketch, "E13.21.11", {"start": v(-73.91, -23.22) * mm, "mid": v(-74.41, -23.6) * mm, "end": v(-74.47, -24.23) * mm});
            skArc(sketch, "E13.22.0", {"start": v(-73.87, -26) * mm, "mid": v(-73.47, -26.46) * mm, "end": v(-72.88, -26.5) * mm});
            skArc(sketch, "E13.22.1", {"start": v(-71.46, -26.07) * mm, "mid": v(-70.62, -26.1) * mm, "end": v(-69.78, -26.18) * mm});
            skLineSegment(sketch, "E13.22.2", {"start": v(-71.74, -26.1) * mm, "end": v(-72.88, -26.5) * mm});
            skArc(sketch, "E13.22.3", {"start": v(-71.46, -26.07) * mm, "mid": v(-71.6, -26.07) * mm, "end": v(-71.74, -26.1) * mm});
            skArc(sketch, "E13.22.4", {"start": v(-69.13, -26.7) * mm, "mid": v(-69.38, -26.35) * mm, "end": v(-69.78, -26.18) * mm});
            skLineSegment(sketch, "E13.22.5", {"start": v(-69.13, -26.7) * mm, "end": v(-69.04, -26.95) * mm});
            skLineSegment(sketch, "E13.22.6", {"start": v(-68.96, -27.2) * mm, "end": v(-69.04, -26.95) * mm});
            skArc(sketch, "E13.22.7", {"start": v(-69.16, -28) * mm, "mid": v(-68.94, -27.63) * mm, "end": v(-68.96, -27.2) * mm});
            skArc(sketch, "E13.22.8", {"start": v(-70.43, -29.12) * mm, "mid": v(-69.78, -28.58) * mm, "end": v(-69.16, -28) * mm});
            skArc(sketch, "E13.22.9", {"start": v(-70.67, -29.25) * mm, "mid": v(-70.54, -29.2) * mm, "end": v(-70.43, -29.12) * mm});
            skLineSegment(sketch, "E13.22.10", {"start": v(-70.67, -29.25) * mm, "end": v(-71.6, -29.57) * mm});
            skArc(sketch, "E13.22.11", {"start": v(-71.6, -29.57) * mm, "mid": v(-72.07, -30) * mm, "end": v(-72.08, -30.63) * mm});
            skArc(sketch, "E13.23.0", {"start": v(-71.32, -32.35) * mm, "mid": v(-70.89, -32.76) * mm, "end": v(-70.29, -32.74) * mm});
            skArc(sketch, "E13.23.1", {"start": v(-68.92, -32.2) * mm, "mid": v(-68.08, -32.16) * mm, "end": v(-67.23, -32.16) * mm});
            skLineSegment(sketch, "E13.23.2", {"start": v(-69.19, -32.26) * mm, "end": v(-70.29, -32.74) * mm});
            skArc(sketch, "E13.23.3", {"start": v(-68.92, -32.2) * mm, "mid": v(-69.06, -32.21) * mm, "end": v(-69.19, -32.26) * mm});
            skArc(sketch, "E13.23.4", {"start": v(-66.54, -32.62) * mm, "mid": v(-66.82, -32.3) * mm, "end": v(-67.23, -32.16) * mm});
            skLineSegment(sketch, "E13.23.5", {"start": v(-66.54, -32.62) * mm, "end": v(-66.43, -32.86) * mm});
            skLineSegment(sketch, "E13.23.6", {"start": v(-66.32, -33.1) * mm, "end": v(-66.43, -32.86) * mm});
            skArc(sketch, "E13.23.7", {"start": v(-66.46, -33.92) * mm, "mid": v(-66.27, -33.53) * mm, "end": v(-66.32, -33.1) * mm});
            skArc(sketch, "E13.23.8", {"start": v(-67.62, -35.15) * mm, "mid": v(-67.02, -34.55) * mm, "end": v(-66.46, -33.92) * mm});
            skArc(sketch, "E13.23.9", {"start": v(-67.85, -35.3) * mm, "mid": v(-67.73, -35.24) * mm, "end": v(-67.62, -35.15) * mm});
            skLineSegment(sketch, "E13.23.10", {"start": v(-67.85, -35.3) * mm, "end": v(-68.76, -35.7) * mm});
            skArc(sketch, "E13.23.11", {"start": v(-68.76, -35.7) * mm, "mid": v(-69.18, -36.17) * mm, "end": v(-69.14, -36.8) * mm});
            skArc(sketch, "E13.24.0", {"start": v(-68.23, -38.44) * mm, "mid": v(-67.76, -38.81) * mm, "end": v(-67.17, -38.75) * mm});
            skArc(sketch, "E13.24.1", {"start": v(-65.85, -38.08) * mm, "mid": v(-65.01, -37.97) * mm, "end": v(-64.17, -37.9) * mm});
            skLineSegment(sketch, "E13.24.2", {"start": v(-66.11, -38.17) * mm, "end": v(-67.17, -38.75) * mm});
            skArc(sketch, "E13.24.3", {"start": v(-65.85, -38.08) * mm, "mid": v(-65.99, -38.11) * mm, "end": v(-66.11, -38.17) * mm});
            skArc(sketch, "E13.24.4", {"start": v(-63.44, -38.3) * mm, "mid": v(-63.75, -38) * mm, "end": v(-64.17, -37.9) * mm});
            skLineSegment(sketch, "E13.24.5", {"start": v(-63.44, -38.3) * mm, "end": v(-63.3, -38.52) * mm});
            skLineSegment(sketch, "E13.24.6", {"start": v(-63.19, -38.76) * mm, "end": v(-63.3, -38.52) * mm});
            skArc(sketch, "E13.24.7", {"start": v(-63.25, -39.59) * mm, "mid": v(-63.1, -39.18) * mm, "end": v(-63.19, -38.76) * mm});
            skArc(sketch, "E13.24.8", {"start": v(-64.3, -40.9) * mm, "mid": v(-63.76, -40.26) * mm, "end": v(-63.25, -39.59) * mm});
            skArc(sketch, "E13.24.9", {"start": v(-64.51, -41.08) * mm, "mid": v(-64.4, -41) * mm, "end": v(-64.3, -40.9) * mm});
            skLineSegment(sketch, "E13.24.10", {"start": v(-64.51, -41.08) * mm, "end": v(-65.38, -41.56) * mm});
            skArc(sketch, "E13.24.11", {"start": v(-65.38, -41.56) * mm, "mid": v(-65.77, -42.06) * mm, "end": v(-65.67, -42.68) * mm});
            skArc(sketch, "E13.25.0", {"start": v(-64.62, -44.24) * mm, "mid": v(-64.12, -44.57) * mm, "end": v(-63.54, -44.45) * mm});
            skArc(sketch, "E13.25.1", {"start": v(-62.28, -43.67) * mm, "mid": v(-61.46, -43.5) * mm, "end": v(-60.62, -43.35) * mm});
            skLineSegment(sketch, "E13.25.2", {"start": v(-62.53, -43.78) * mm, "end": v(-63.54, -44.45) * mm});
            skArc(sketch, "E13.25.3", {"start": v(-62.28, -43.67) * mm, "mid": v(-62.41, -43.72) * mm, "end": v(-62.53, -43.78) * mm});
            skArc(sketch, "E13.25.4", {"start": v(-59.86, -43.68) * mm, "mid": v(-60.2, -43.4) * mm, "end": v(-60.62, -43.35) * mm});
            skLineSegment(sketch, "E13.25.5", {"start": v(-59.86, -43.68) * mm, "end": v(-59.71, -43.9) * mm});
            skLineSegment(sketch, "E13.25.6", {"start": v(-59.57, -44.12) * mm, "end": v(-59.71, -43.9) * mm});
            skArc(sketch, "E13.25.7", {"start": v(-59.56, -44.95) * mm, "mid": v(-59.44, -44.53) * mm, "end": v(-59.57, -44.12) * mm});
            skArc(sketch, "E13.25.8", {"start": v(-60.49, -46.36) * mm, "mid": v(-60, -45.66) * mm, "end": v(-59.56, -44.95) * mm});
            skArc(sketch, "E13.25.9", {"start": v(-60.69, -46.55) * mm, "mid": v(-60.58, -46.46) * mm, "end": v(-60.49, -46.36) * mm});
            skLineSegment(sketch, "E13.25.10", {"start": v(-60.69, -46.55) * mm, "end": v(-61.51, -47.1) * mm});
            skArc(sketch, "E13.25.11", {"start": v(-61.51, -47.1) * mm, "mid": v(-61.85, -47.63) * mm, "end": v(-61.7, -48.24) * mm});
            skArc(sketch, "E13.26.0", {"start": v(-60.52, -49.7) * mm, "mid": v(-60, -49.99) * mm, "end": v(-59.42, -49.82) * mm});
            skArc(sketch, "E13.26.1", {"start": v(-58.24, -48.93) * mm, "mid": v(-57.43, -48.68) * mm, "end": v(-56.61, -48.47) * mm});
            skLineSegment(sketch, "E13.26.2", {"start": v(-58.48, -49.07) * mm, "end": v(-59.42, -49.82) * mm});
            skArc(sketch, "E13.26.3", {"start": v(-58.24, -48.93) * mm, "mid": v(-58.37, -49) * mm, "end": v(-58.48, -49.07) * mm});
            skArc(sketch, "E13.26.4", {"start": v(-55.83, -48.73) * mm, "mid": v(-56.18, -48.49) * mm, "end": v(-56.61, -48.47) * mm});
            skLineSegment(sketch, "E13.26.5", {"start": v(-55.83, -48.73) * mm, "end": v(-55.66, -48.93) * mm});
            skLineSegment(sketch, "E13.26.6", {"start": v(-55.5, -49.14) * mm, "end": v(-55.66, -48.93) * mm});
            skArc(sketch, "E13.26.7", {"start": v(-55.41, -49.97) * mm, "mid": v(-55.34, -49.54) * mm, "end": v(-55.5, -49.14) * mm});
            skArc(sketch, "E13.26.8", {"start": v(-56.22, -51.45) * mm, "mid": v(-55.8, -50.72) * mm, "end": v(-55.41, -49.97) * mm});
            skArc(sketch, "E13.26.9", {"start": v(-56.4, -51.66) * mm, "mid": v(-56.3, -51.56) * mm, "end": v(-56.22, -51.45) * mm});
            skLineSegment(sketch, "E13.26.10", {"start": v(-56.4, -51.66) * mm, "end": v(-57.17, -52.28) * mm});
            skArc(sketch, "E13.26.11", {"start": v(-57.17, -52.28) * mm, "mid": v(-57.47, -52.84) * mm, "end": v(-57.26, -53.43) * mm});
            skArc(sketch, "E13.27.0", {"start": v(-55.96, -54.8) * mm, "mid": v(-55.4, -55.03) * mm, "end": v(-54.85, -54.8) * mm});
            skArc(sketch, "E13.27.1", {"start": v(-53.75, -53.82) * mm, "mid": v(-52.97, -53.5) * mm, "end": v(-52.17, -53.22) * mm});
            skLineSegment(sketch, "E13.27.2", {"start": v(-53.98, -53.98) * mm, "end": v(-54.85, -54.8) * mm});
            skArc(sketch, "E13.27.3", {"start": v(-53.75, -53.82) * mm, "mid": v(-53.87, -53.9) * mm, "end": v(-53.98, -53.98) * mm});
            skArc(sketch, "E13.27.4", {"start": v(-51.37, -53.4) * mm, "mid": v(-51.74, -53.2) * mm, "end": v(-52.17, -53.22) * mm});
            skLineSegment(sketch, "E13.27.5", {"start": v(-51.37, -53.4) * mm, "end": v(-51.18, -53.6) * mm});
            skLineSegment(sketch, "E13.27.6", {"start": v(-51, -53.8) * mm, "end": v(-51.18, -53.6) * mm});
            skArc(sketch, "E13.27.7", {"start": v(-50.85, -54.6) * mm, "mid": v(-50.8, -54.18) * mm, "end": v(-51, -53.8) * mm});
            skArc(sketch, "E13.27.8", {"start": v(-51.52, -56.16) * mm, "mid": v(-51.17, -55.39) * mm, "end": v(-50.85, -54.6) * mm});
            skArc(sketch, "E13.27.9", {"start": v(-51.68, -56.38) * mm, "mid": v(-51.6, -56.27) * mm, "end": v(-51.52, -56.16) * mm});
            skLineSegment(sketch, "E13.27.10", {"start": v(-51.68, -56.38) * mm, "end": v(-52.4, -57.07) * mm});
            skArc(sketch, "E13.27.11", {"start": v(-52.4, -57.07) * mm, "mid": v(-52.64, -57.65) * mm, "end": v(-52.38, -58.22) * mm});
            skArc(sketch, "E13.28.0", {"start": v(-50.97, -59.46) * mm, "mid": v(-50.4, -59.65) * mm, "end": v(-49.87, -59.38) * mm});
            skArc(sketch, "E13.28.1", {"start": v(-48.86, -58.3) * mm, "mid": v(-48.1, -57.92) * mm, "end": v(-47.34, -57.56) * mm});
            skLineSegment(sketch, "E13.28.2", {"start": v(-49.07, -58.48) * mm, "end": v(-49.87, -59.38) * mm});
            skArc(sketch, "E13.28.3", {"start": v(-48.86, -58.3) * mm, "mid": v(-48.97, -58.38) * mm, "end": v(-49.07, -58.48) * mm});
            skArc(sketch, "E13.28.4", {"start": v(-46.52, -57.68) * mm, "mid": v(-46.91, -57.5) * mm, "end": v(-47.34, -57.56) * mm});
            skLineSegment(sketch, "E13.28.5", {"start": v(-46.52, -57.68) * mm, "end": v(-46.31, -57.85) * mm});
            skLineSegment(sketch, "E13.28.6", {"start": v(-46.12, -58.03) * mm, "end": v(-46.31, -57.85) * mm});
            skArc(sketch, "E13.28.7", {"start": v(-45.9, -58.83) * mm, "mid": v(-45.9, -58.4) * mm, "end": v(-46.12, -58.03) * mm});
            skArc(sketch, "E13.28.8", {"start": v(-46.43, -60.43) * mm, "mid": v(-46.14, -59.64) * mm, "end": v(-45.9, -58.83) * mm});
            skArc(sketch, "E13.28.9", {"start": v(-46.57, -60.67) * mm, "mid": v(-46.5, -60.56) * mm, "end": v(-46.43, -60.43) * mm});
            skLineSegment(sketch, "E13.28.10", {"start": v(-46.57, -60.67) * mm, "end": v(-47.23, -61.42) * mm});
            skArc(sketch, "E13.28.11", {"start": v(-47.23, -61.42) * mm, "mid": v(-47.42, -62.02) * mm, "end": v(-47.1, -62.56) * mm});
            skArc(sketch, "E13.29.0", {"start": v(-45.6, -63.68) * mm, "mid": v(-45.01, -63.81) * mm, "end": v(-44.5, -63.5) * mm});
            skArc(sketch, "E13.29.1", {"start": v(-43.59, -62.34) * mm, "mid": v(-42.87, -61.89) * mm, "end": v(-42.14, -61.47) * mm});
            skLineSegment(sketch, "E13.29.2", {"start": v(-43.79, -62.53) * mm, "end": v(-44.5, -63.5) * mm});
            skArc(sketch, "E13.29.3", {"start": v(-43.59, -62.34) * mm, "mid": v(-43.7, -62.43) * mm, "end": v(-43.79, -62.53) * mm});
            skArc(sketch, "E13.29.4", {"start": v(-41.31, -61.52) * mm, "mid": v(-41.72, -61.38) * mm, "end": v(-42.14, -61.47) * mm});
            skLineSegment(sketch, "E13.29.5", {"start": v(-41.31, -61.52) * mm, "end": v(-41.1, -61.67) * mm});
            skLineSegment(sketch, "E13.29.6", {"start": v(-40.89, -61.83) * mm, "end": v(-41.1, -61.67) * mm});
            skArc(sketch, "E13.29.7", {"start": v(-40.6, -62.6) * mm, "mid": v(-40.63, -62.18) * mm, "end": v(-40.89, -61.83) * mm});
            skArc(sketch, "E13.29.8", {"start": v(-40.99, -64.25) * mm, "mid": v(-40.77, -63.43) * mm, "end": v(-40.6, -62.6) * mm});
            skArc(sketch, "E13.29.9", {"start": v(-41.1, -64.5) * mm, "mid": v(-41.04, -64.38) * mm, "end": v(-40.99, -64.25) * mm});
            skLineSegment(sketch, "E13.29.10", {"start": v(-41.1, -64.5) * mm, "end": v(-41.7, -65.3) * mm});
            skArc(sketch, "E13.29.11", {"start": v(-41.7, -65.3) * mm, "mid": v(-41.83, -65.91) * mm, "end": v(-41.48, -66.43) * mm});
            skArc(sketch, "E13.30.0", {"start": v(-39.87, -67.4) * mm, "mid": v(-39.28, -67.5) * mm, "end": v(-38.8, -67.14) * mm});
            skArc(sketch, "E13.30.1", {"start": v(-37.99, -65.9) * mm, "mid": v(-37.32, -65.4) * mm, "end": v(-36.62, -64.9) * mm});
            skLineSegment(sketch, "E13.30.2", {"start": v(-38.17, -66.1) * mm, "end": v(-38.8, -67.14) * mm});
            skArc(sketch, "E13.30.3", {"start": v(-37.99, -65.9) * mm, "mid": v(-38.09, -66) * mm, "end": v(-38.17, -66.1) * mm});
            skArc(sketch, "E13.30.4", {"start": v(-35.8, -64.88) * mm, "mid": v(-36.21, -64.78) * mm, "end": v(-36.62, -64.9) * mm});
            skLineSegment(sketch, "E13.30.5", {"start": v(-35.8, -64.88) * mm, "end": v(-35.56, -65.02) * mm});
            skLineSegment(sketch, "E13.30.6", {"start": v(-35.34, -65.16) * mm, "end": v(-35.56, -65.02) * mm});
            skArc(sketch, "E13.30.7", {"start": v(-34.98, -65.9) * mm, "mid": v(-35.05, -65.48) * mm, "end": v(-35.34, -65.16) * mm});
            skArc(sketch, "E13.30.8", {"start": v(-35.23, -67.58) * mm, "mid": v(-35.09, -66.74) * mm, "end": v(-34.98, -65.9) * mm});
            skArc(sketch, "E13.30.9", {"start": v(-35.33, -67.83) * mm, "mid": v(-35.27, -67.71) * mm, "end": v(-35.23, -67.58) * mm});
            skLineSegment(sketch, "E13.30.10", {"start": v(-35.33, -67.83) * mm, "end": v(-35.85, -68.68) * mm});
            skArc(sketch, "E13.30.11", {"start": v(-35.85, -68.68) * mm, "mid": v(-35.93, -69.3) * mm, "end": v(-35.53, -69.8) * mm});
            skArc(sketch, "E13.31.0", {"start": v(-33.84, -70.63) * mm, "mid": v(-33.25, -70.66) * mm, "end": v(-32.8, -70.26) * mm});
            skArc(sketch, "E13.31.1", {"start": v(-32.1, -68.96) * mm, "mid": v(-31.48, -68.4) * mm, "end": v(-30.83, -67.85) * mm});
            skLineSegment(sketch, "E13.31.2", {"start": v(-32.26, -69.19) * mm, "end": v(-32.8, -70.26) * mm});
            skArc(sketch, "E13.31.3", {"start": v(-32.1, -68.96) * mm, "mid": v(-32.2, -69.07) * mm, "end": v(-32.26, -69.19) * mm});
            skArc(sketch, "E13.31.4", {"start": v(-30, -67.76) * mm, "mid": v(-30.43, -67.69) * mm, "end": v(-30.83, -67.85) * mm});
            skLineSegment(sketch, "E13.31.5", {"start": v(-30, -67.76) * mm, "end": v(-29.76, -67.87) * mm});
            skLineSegment(sketch, "E13.31.6", {"start": v(-29.53, -68) * mm, "end": v(-29.76, -67.87) * mm});
            skArc(sketch, "E13.31.7", {"start": v(-29.1, -68.7) * mm, "mid": v(-29.21, -68.29) * mm, "end": v(-29.53, -68) * mm});
            skArc(sketch, "E13.31.8", {"start": v(-29.2, -70.4) * mm, "mid": v(-29.14, -69.55) * mm, "end": v(-29.1, -68.7) * mm});
            skArc(sketch, "E13.31.9", {"start": v(-29.28, -70.66) * mm, "mid": v(-29.23, -70.53) * mm, "end": v(-29.2, -70.4) * mm});
            skLineSegment(sketch, "E13.31.10", {"start": v(-29.28, -70.66) * mm, "end": v(-29.72, -71.55) * mm});
            skArc(sketch, "E13.31.11", {"start": v(-29.72, -71.55) * mm, "mid": v(-29.75, -72.18) * mm, "end": v(-29.31, -72.62) * mm});
            skArc(sketch, "E13.32.0", {"start": v(-27.56, -73.3) * mm, "mid": v(-26.96, -73.29) * mm, "end": v(-26.55, -72.86) * mm});
            skArc(sketch, "E13.32.1", {"start": v(-25.97, -71.5) * mm, "mid": v(-25.4, -70.88) * mm, "end": v(-24.8, -70.28) * mm});
            skLineSegment(sketch, "E13.32.2", {"start": v(-26.11, -71.73) * mm, "end": v(-26.55, -72.86) * mm});
            skArc(sketch, "E13.32.3", {"start": v(-25.97, -71.5) * mm, "mid": v(-26.05, -71.6) * mm, "end": v(-26.11, -71.73) * mm});
            skArc(sketch, "E13.32.4", {"start": v(-23.98, -70.11) * mm, "mid": v(-24.41, -70.08) * mm, "end": v(-24.8, -70.28) * mm});
            skLineSegment(sketch, "E13.32.5", {"start": v(-23.98, -70.11) * mm, "end": v(-23.73, -70.2) * mm});
            skLineSegment(sketch, "E13.32.6", {"start": v(-23.49, -70.3) * mm, "end": v(-23.73, -70.2) * mm});
            skArc(sketch, "E13.32.7", {"start": v(-23, -70.98) * mm, "mid": v(-23.15, -70.57) * mm, "end": v(-23.49, -70.3) * mm});
            skArc(sketch, "E13.32.8", {"start": v(-22.96, -72.67) * mm, "mid": v(-22.96, -71.82) * mm, "end": v(-23, -70.98) * mm});
            skArc(sketch, "E13.32.9", {"start": v(-23.01, -72.94) * mm, "mid": v(-22.98, -72.8) * mm, "end": v(-22.96, -72.67) * mm});
            skLineSegment(sketch, "E13.32.10", {"start": v(-23.01, -72.94) * mm, "end": v(-23.37, -73.86) * mm});
            skArc(sketch, "E13.32.11", {"start": v(-23.37, -73.86) * mm, "mid": v(-23.35, -74.5) * mm, "end": v(-22.87, -74.9) * mm});
            skArc(sketch, "E13.33.0", {"start": v(-21.07, -75.43) * mm, "mid": v(-20.47, -75.36) * mm, "end": v(-20.1, -74.9) * mm});
            skArc(sketch, "E13.33.1", {"start": v(-19.64, -73.49) * mm, "mid": v(-19.12, -72.82) * mm, "end": v(-18.58, -72.18) * mm});
            skLineSegment(sketch, "E13.33.2", {"start": v(-19.76, -73.74) * mm, "end": v(-20.1, -74.9) * mm});
            skArc(sketch, "E13.33.3", {"start": v(-19.64, -73.49) * mm, "mid": v(-19.71, -73.6) * mm, "end": v(-19.76, -73.74) * mm});
            skArc(sketch, "E13.33.4", {"start": v(-17.78, -71.94) * mm, "mid": v(-18.21, -71.94) * mm, "end": v(-18.58, -72.18) * mm});
            skLineSegment(sketch, "E13.33.5", {"start": v(-17.78, -71.94) * mm, "end": v(-17.53, -72) * mm});
            skLineSegment(sketch, "E13.33.6", {"start": v(-17.27, -72.09) * mm, "end": v(-17.53, -72) * mm});
            skArc(sketch, "E13.33.7", {"start": v(-16.73, -72.71) * mm, "mid": v(-16.91, -72.32) * mm, "end": v(-17.27, -72.09) * mm});
            skArc(sketch, "E13.33.8", {"start": v(-16.54, -74.4) * mm, "mid": v(-16.62, -73.55) * mm, "end": v(-16.73, -72.71) * mm});
            skArc(sketch, "E13.33.9", {"start": v(-16.57, -74.67) * mm, "mid": v(-16.54, -74.53) * mm, "end": v(-16.54, -74.4) * mm});
            skLineSegment(sketch, "E13.33.10", {"start": v(-16.57, -74.67) * mm, "end": v(-16.85, -75.62) * mm});
            skArc(sketch, "E13.33.11", {"start": v(-16.85, -75.62) * mm, "mid": v(-16.77, -76.25) * mm, "end": v(-16.25, -76.61) * mm});
            skArc(sketch, "E13.34.0", {"start": v(-14.41, -76.98) * mm, "mid": v(-13.83, -76.86) * mm, "end": v(-13.5, -76.36) * mm});
            skArc(sketch, "E13.34.1", {"start": v(-13.16, -74.92) * mm, "mid": v(-12.7, -74.21) * mm, "end": v(-12.21, -73.52) * mm});
            skLineSegment(sketch, "E13.34.2", {"start": v(-13.26, -75.18) * mm, "end": v(-13.5, -76.36) * mm});
            skArc(sketch, "E13.34.3", {"start": v(-13.16, -74.92) * mm, "mid": v(-13.22, -75.05) * mm, "end": v(-13.26, -75.18) * mm});
            skArc(sketch, "E13.34.4", {"start": v(-11.44, -73.21) * mm, "mid": v(-11.87, -73.26) * mm, "end": v(-12.21, -73.52) * mm});
            skLineSegment(sketch, "E13.34.5", {"start": v(-11.44, -73.21) * mm, "end": v(-11.18, -73.26) * mm});
            skLineSegment(sketch, "E13.34.6", {"start": v(-10.92, -73.32) * mm, "end": v(-11.18, -73.26) * mm});
            skArc(sketch, "E13.34.7", {"start": v(-10.33, -73.9) * mm, "mid": v(-10.54, -73.52) * mm, "end": v(-10.92, -73.32) * mm});
            skArc(sketch, "E13.34.8", {"start": v(-10, -75.55) * mm, "mid": v(-10.14, -74.72) * mm, "end": v(-10.33, -73.9) * mm});
            skArc(sketch, "E13.34.9", {"start": v(-10, -75.83) * mm, "mid": v(-9.98, -75.69) * mm, "end": v(-10, -75.55) * mm});
            skLineSegment(sketch, "E13.34.10", {"start": v(-10, -75.83) * mm, "end": v(-10.2, -76.8) * mm});
            skArc(sketch, "E13.34.11", {"start": v(-10.2, -76.8) * mm, "mid": v(-10.06, -77.42) * mm, "end": v(-9.52, -77.74) * mm});
            skArc(sketch, "E13.35.0", {"start": v(-7.65, -77.94) * mm, "mid": v(-7.07, -77.77) * mm, "end": v(-6.79, -77.24) * mm});
            skArc(sketch, "E13.35.1", {"start": v(-6.58, -75.78) * mm, "mid": v(-6.19, -75.04) * mm, "end": v(-5.76, -74.3) * mm});
            skLineSegment(sketch, "E13.35.2", {"start": v(-6.66, -76.05) * mm, "end": v(-6.79, -77.24) * mm});
            skArc(sketch, "E13.35.3", {"start": v(-6.58, -75.78) * mm, "mid": v(-6.63, -75.91) * mm, "end": v(-6.66, -76.05) * mm});
            skArc(sketch, "E13.35.4", {"start": v(-5.02, -73.93) * mm, "mid": v(-5.44, -74.01) * mm, "end": v(-5.76, -74.3) * mm});
            skLineSegment(sketch, "E13.35.5", {"start": v(-5.02, -73.93) * mm, "end": v(-4.76, -73.96) * mm});
            skLineSegment(sketch, "E13.35.6", {"start": v(-4.5, -74) * mm, "end": v(-4.76, -73.96) * mm});
            skArc(sketch, "E13.35.7", {"start": v(-3.85, -74.51) * mm, "mid": v(-4.1, -74.16) * mm, "end": v(-4.5, -74) * mm});
            skArc(sketch, "E13.35.8", {"start": v(-3.37, -76.13) * mm, "mid": v(-3.6, -75.32) * mm, "end": v(-3.85, -74.51) * mm});
            skArc(sketch, "E13.35.9", {"start": v(-3.35, -76.4) * mm, "mid": v(-3.35, -76.27) * mm, "end": v(-3.37, -76.13) * mm});
            skLineSegment(sketch, "E13.35.10", {"start": v(-3.35, -76.4) * mm, "end": v(-3.46, -77.4) * mm});
            skArc(sketch, "E13.35.11", {"start": v(-3.46, -77.4) * mm, "mid": v(-3.27, -78) * mm, "end": v(-2.7, -78.27) * mm});
            skArc(sketch, "E13.36.0", {"start": v(-0.82, -78.31) * mm, "mid": v(-0.27, -78.1) * mm, "end": v(-0.03, -77.54) * mm});
            skArc(sketch, "E13.36.1", {"start": v(0.05, -76.07) * mm, "mid": v(0.38, -75.29) * mm, "end": v(0.74, -74.52) * mm});
            skLineSegment(sketch, "E13.36.2", {"start": v(0, -76.34) * mm, "end": v(-0.03, -77.54) * mm});
            skArc(sketch, "E13.36.3", {"start": v(0.05, -76.07) * mm, "mid": v(0.01, -76.2) * mm, "end": v(0, -76.34) * mm});
            skArc(sketch, "E13.36.4", {"start": v(1.44, -74.09) * mm, "mid": v(1.03, -74.2) * mm, "end": v(0.74, -74.52) * mm});
            skLineSegment(sketch, "E13.36.5", {"start": v(1.44, -74.09) * mm, "end": v(1.7, -74.09) * mm});
            skLineSegment(sketch, "E13.36.6", {"start": v(1.97, -74.1) * mm, "end": v(1.7, -74.09) * mm});
            skArc(sketch, "E13.36.7", {"start": v(2.66, -74.57) * mm, "mid": v(2.38, -74.24) * mm, "end": v(1.97, -74.1) * mm});
            skArc(sketch, "E13.36.8", {"start": v(3.28, -76.14) * mm, "mid": v(2.99, -75.35) * mm, "end": v(2.66, -74.57) * mm});
            skArc(sketch, "E13.36.9", {"start": v(3.32, -76.41) * mm, "mid": v(3.31, -76.27) * mm, "end": v(3.28, -76.14) * mm});
            skLineSegment(sketch, "E13.36.10", {"start": v(3.32, -76.41) * mm, "end": v(3.3, -77.4) * mm});
            skArc(sketch, "E13.36.11", {"start": v(3.3, -77.4) * mm, "mid": v(3.54, -77.99) * mm, "end": v(4.13, -78.2) * mm});
            skArc(sketch, "E13.37.0", {"start": v(6, -78.09) * mm, "mid": v(6.54, -77.82) * mm, "end": v(6.73, -77.25) * mm});
            skArc(sketch, "E13.37.1", {"start": v(6.68, -75.77) * mm, "mid": v(6.94, -74.97) * mm, "end": v(7.23, -74.18) * mm});
            skLineSegment(sketch, "E13.37.2", {"start": v(6.65, -76.05) * mm, "end": v(6.73, -77.25) * mm});
            skArc(sketch, "E13.37.3", {"start": v(6.68, -75.77) * mm, "mid": v(6.65, -75.9) * mm, "end": v(6.65, -76.05) * mm});
            skArc(sketch, "E13.37.4", {"start": v(7.9, -73.68) * mm, "mid": v(7.5, -73.83) * mm, "end": v(7.23, -74.18) * mm});
            skLineSegment(sketch, "E13.37.5", {"start": v(7.9, -73.68) * mm, "end": v(8.16, -73.66) * mm});
            skLineSegment(sketch, "E13.37.6", {"start": v(8.43, -73.65) * mm, "end": v(8.16, -73.66) * mm});
            skArc(sketch, "E13.37.7", {"start": v(9.15, -74.05) * mm, "mid": v(8.84, -73.75) * mm, "end": v(8.43, -73.65) * mm});
            skArc(sketch, "E13.37.8", {"start": v(9.9, -75.56) * mm, "mid": v(9.54, -74.8) * mm, "end": v(9.15, -74.05) * mm});
            skArc(sketch, "E13.37.9", {"start": v(9.97, -75.83) * mm, "mid": v(9.95, -75.7) * mm, "end": v(9.9, -75.56) * mm});
            skLineSegment(sketch, "E13.37.10", {"start": v(9.97, -75.83) * mm, "end": v(10.03, -76.82) * mm});
            skArc(sketch, "E13.37.11", {"start": v(10.03, -76.82) * mm, "mid": v(10.32, -77.38) * mm, "end": v(10.93, -77.55) * mm});
            skArc(sketch, "E13.38.0", {"start": v(12.79, -77.27) * mm, "mid": v(13.3, -76.95) * mm, "end": v(13.44, -76.37) * mm});
            skArc(sketch, "E13.38.1", {"start": v(13.26, -74.9) * mm, "mid": v(13.45, -74.08) * mm, "end": v(13.67, -73.26) * mm});
            skLineSegment(sketch, "E13.38.2", {"start": v(13.25, -75.18) * mm, "end": v(13.44, -76.37) * mm});
            skArc(sketch, "E13.38.3", {"start": v(13.26, -74.9) * mm, "mid": v(13.24, -75.04) * mm, "end": v(13.25, -75.18) * mm});
            skArc(sketch, "E13.38.4", {"start": v(14.29, -72.71) * mm, "mid": v(13.9, -72.9) * mm, "end": v(13.67, -73.26) * mm});
            skLineSegment(sketch, "E13.38.5", {"start": v(14.29, -72.71) * mm, "end": v(14.55, -72.67) * mm});
            skLineSegment(sketch, "E13.38.6", {"start": v(14.81, -72.63) * mm, "end": v(14.55, -72.67) * mm});
            skArc(sketch, "E13.38.7", {"start": v(15.57, -72.97) * mm, "mid": v(15.24, -72.7) * mm, "end": v(14.81, -72.63) * mm});
            skArc(sketch, "E13.38.8", {"start": v(16.45, -74.41) * mm, "mid": v(16.02, -73.68) * mm, "end": v(15.57, -72.97) * mm});
            skArc(sketch, "E13.38.9", {"start": v(16.54, -74.67) * mm, "mid": v(16.5, -74.54) * mm, "end": v(16.45, -74.41) * mm});
            skLineSegment(sketch, "E13.38.10", {"start": v(16.54, -74.67) * mm, "end": v(16.7, -75.66) * mm});
            skArc(sketch, "E13.38.11", {"start": v(16.7, -75.66) * mm, "mid": v(17.03, -76.19) * mm, "end": v(17.65, -76.3) * mm});
            skArc(sketch, "E13.39.0", {"start": v(19.47, -75.86) * mm, "mid": v(19.95, -75.5) * mm, "end": v(20.04, -74.9) * mm});
            skArc(sketch, "E13.39.1", {"start": v(19.74, -73.46) * mm, "mid": v(19.85, -72.63) * mm, "end": v(20, -71.8) * mm});
            skLineSegment(sketch, "E13.39.2", {"start": v(19.76, -73.74) * mm, "end": v(20.04, -74.9) * mm});
            skArc(sketch, "E13.39.3", {"start": v(19.74, -73.46) * mm, "mid": v(19.73, -73.6) * mm, "end": v(19.76, -73.74) * mm});
            skArc(sketch, "E13.39.4", {"start": v(20.57, -71.2) * mm, "mid": v(20.2, -71.41) * mm, "end": v(20, -71.8) * mm});
            skLineSegment(sketch, "E13.39.5", {"start": v(20.57, -71.2) * mm, "end": v(20.83, -71.12) * mm});
            skLineSegment(sketch, "E13.39.6", {"start": v(21.09, -71.06) * mm, "end": v(20.83, -71.12) * mm});
            skArc(sketch, "E13.39.7", {"start": v(21.87, -71.34) * mm, "mid": v(21.52, -71.1) * mm, "end": v(21.09, -71.06) * mm});
            skArc(sketch, "E13.39.8", {"start": v(22.87, -72.7) * mm, "mid": v(22.39, -72) * mm, "end": v(21.87, -71.34) * mm});
            skArc(sketch, "E13.39.9", {"start": v(22.98, -72.95) * mm, "mid": v(22.94, -72.82) * mm, "end": v(22.87, -72.7) * mm});
            skLineSegment(sketch, "E13.39.10", {"start": v(22.98, -72.95) * mm, "end": v(23.22, -73.91) * mm});
            skArc(sketch, "E13.39.11", {"start": v(23.22, -73.91) * mm, "mid": v(23.6, -74.41) * mm, "end": v(24.23, -74.47) * mm});
            skArc(sketch, "E13.40.0", {"start": v(26, -73.87) * mm, "mid": v(26.46, -73.47) * mm, "end": v(26.5, -72.88) * mm});
            skArc(sketch, "E13.40.1", {"start": v(26.07, -71.46) * mm, "mid": v(26.1, -70.62) * mm, "end": v(26.18, -69.78) * mm});
            skLineSegment(sketch, "E13.40.2", {"start": v(26.1, -71.74) * mm, "end": v(26.5, -72.88) * mm});
            skArc(sketch, "E13.40.3", {"start": v(26.07, -71.46) * mm, "mid": v(26.07, -71.6) * mm, "end": v(26.1, -71.74) * mm});
            skArc(sketch, "E13.40.4", {"start": v(26.7, -69.13) * mm, "mid": v(26.35, -69.38) * mm, "end": v(26.18, -69.78) * mm});
            skLineSegment(sketch, "E13.40.5", {"start": v(26.7, -69.13) * mm, "end": v(26.95, -69.04) * mm});
            skLineSegment(sketch, "E13.40.6", {"start": v(27.2, -68.96) * mm, "end": v(26.95, -69.04) * mm});
            skArc(sketch, "E13.40.7", {"start": v(28, -69.16) * mm, "mid": v(27.63, -68.94) * mm, "end": v(27.2, -68.96) * mm});
            skArc(sketch, "E13.40.8", {"start": v(29.12, -70.43) * mm, "mid": v(28.58, -69.78) * mm, "end": v(28, -69.16) * mm});
            skArc(sketch, "E13.40.9", {"start": v(29.25, -70.67) * mm, "mid": v(29.2, -70.54) * mm, "end": v(29.12, -70.43) * mm});
            skLineSegment(sketch, "E13.40.10", {"start": v(29.25, -70.67) * mm, "end": v(29.57, -71.6) * mm});
            skArc(sketch, "E13.40.11", {"start": v(29.57, -71.6) * mm, "mid": v(30, -72.07) * mm, "end": v(30.63, -72.08) * mm});
            skArc(sketch, "E13.41.0", {"start": v(32.35, -71.32) * mm, "mid": v(32.76, -70.89) * mm, "end": v(32.74, -70.29) * mm});
            skArc(sketch, "E13.41.1", {"start": v(32.2, -68.92) * mm, "mid": v(32.16, -68.08) * mm, "end": v(32.16, -67.23) * mm});
            skLineSegment(sketch, "E13.41.2", {"start": v(32.26, -69.19) * mm, "end": v(32.74, -70.29) * mm});
            skArc(sketch, "E13.41.3", {"start": v(32.2, -68.92) * mm, "mid": v(32.21, -69.06) * mm, "end": v(32.26, -69.19) * mm});
            skArc(sketch, "E13.41.4", {"start": v(32.62, -66.54) * mm, "mid": v(32.3, -66.82) * mm, "end": v(32.16, -67.23) * mm});
            skLineSegment(sketch, "E13.41.5", {"start": v(32.62, -66.54) * mm, "end": v(32.86, -66.43) * mm});
            skLineSegment(sketch, "E13.41.6", {"start": v(33.1, -66.32) * mm, "end": v(32.86, -66.43) * mm});
            skArc(sketch, "E13.41.7", {"start": v(33.92, -66.46) * mm, "mid": v(33.53, -66.27) * mm, "end": v(33.1, -66.32) * mm});
            skArc(sketch, "E13.41.8", {"start": v(35.15, -67.62) * mm, "mid": v(34.55, -67.02) * mm, "end": v(33.92, -66.46) * mm});
            skArc(sketch, "E13.41.9", {"start": v(35.3, -67.85) * mm, "mid": v(35.24, -67.73) * mm, "end": v(35.15, -67.62) * mm});
            skLineSegment(sketch, "E13.41.10", {"start": v(35.3, -67.85) * mm, "end": v(35.7, -68.76) * mm});
            skArc(sketch, "E13.41.11", {"start": v(35.7, -68.76) * mm, "mid": v(36.17, -69.18) * mm, "end": v(36.8, -69.14) * mm});
            skArc(sketch, "E13.42.0", {"start": v(38.44, -68.23) * mm, "mid": v(38.81, -67.76) * mm, "end": v(38.75, -67.17) * mm});
            skArc(sketch, "E13.42.1", {"start": v(38.08, -65.85) * mm, "mid": v(37.97, -65.01) * mm, "end": v(37.9, -64.17) * mm});
            skLineSegment(sketch, "E13.42.2", {"start": v(38.17, -66.11) * mm, "end": v(38.75, -67.17) * mm});
            skArc(sketch, "E13.42.3", {"start": v(38.08, -65.85) * mm, "mid": v(38.11, -65.99) * mm, "end": v(38.17, -66.11) * mm});
            skArc(sketch, "E13.42.4", {"start": v(38.3, -63.44) * mm, "mid": v(38, -63.75) * mm, "end": v(37.9, -64.17) * mm});
            skLineSegment(sketch, "E13.42.5", {"start": v(38.3, -63.44) * mm, "end": v(38.52, -63.3) * mm});
            skLineSegment(sketch, "E13.42.6", {"start": v(38.76, -63.19) * mm, "end": v(38.52, -63.3) * mm});
            skArc(sketch, "E13.42.7", {"start": v(39.59, -63.25) * mm, "mid": v(39.18, -63.1) * mm, "end": v(38.76, -63.19) * mm});
            skArc(sketch, "E13.42.8", {"start": v(40.9, -64.3) * mm, "mid": v(40.26, -63.76) * mm, "end": v(39.59, -63.25) * mm});
            skArc(sketch, "E13.42.9", {"start": v(41.08, -64.51) * mm, "mid": v(41, -64.4) * mm, "end": v(40.9, -64.3) * mm});
            skLineSegment(sketch, "E13.42.10", {"start": v(41.08, -64.51) * mm, "end": v(41.56, -65.38) * mm});
            skArc(sketch, "E13.42.11", {"start": v(41.56, -65.38) * mm, "mid": v(42.06, -65.77) * mm, "end": v(42.68, -65.67) * mm});
            skArc(sketch, "E13.43.0", {"start": v(44.24, -64.62) * mm, "mid": v(44.57, -64.12) * mm, "end": v(44.45, -63.54) * mm});
            skArc(sketch, "E13.43.1", {"start": v(43.67, -62.28) * mm, "mid": v(43.5, -61.46) * mm, "end": v(43.35, -60.62) * mm});
            skLineSegment(sketch, "E13.43.2", {"start": v(43.78, -62.53) * mm, "end": v(44.45, -63.54) * mm});
            skArc(sketch, "E13.43.3", {"start": v(43.67, -62.28) * mm, "mid": v(43.72, -62.41) * mm, "end": v(43.78, -62.53) * mm});
            skArc(sketch, "E13.43.4", {"start": v(43.68, -59.86) * mm, "mid": v(43.4, -60.2) * mm, "end": v(43.35, -60.62) * mm});
            skLineSegment(sketch, "E13.43.5", {"start": v(43.68, -59.86) * mm, "end": v(43.9, -59.71) * mm});
            skLineSegment(sketch, "E13.43.6", {"start": v(44.12, -59.57) * mm, "end": v(43.9, -59.71) * mm});
            skArc(sketch, "E13.43.7", {"start": v(44.95, -59.56) * mm, "mid": v(44.53, -59.44) * mm, "end": v(44.12, -59.57) * mm});
            skArc(sketch, "E13.43.8", {"start": v(46.36, -60.49) * mm, "mid": v(45.66, -60) * mm, "end": v(44.95, -59.56) * mm});
            skArc(sketch, "E13.43.9", {"start": v(46.55, -60.69) * mm, "mid": v(46.46, -60.58) * mm, "end": v(46.36, -60.49) * mm});
            skLineSegment(sketch, "E13.43.10", {"start": v(46.55, -60.69) * mm, "end": v(47.1, -61.51) * mm});
            skArc(sketch, "E13.43.11", {"start": v(47.1, -61.51) * mm, "mid": v(47.63, -61.85) * mm, "end": v(48.24, -61.7) * mm});
            skArc(sketch, "E13.44.0", {"start": v(49.7, -60.52) * mm, "mid": v(49.99, -60) * mm, "end": v(49.82, -59.42) * mm});
            skArc(sketch, "E13.44.1", {"start": v(48.93, -58.24) * mm, "mid": v(48.68, -57.43) * mm, "end": v(48.47, -56.61) * mm});
            skLineSegment(sketch, "E13.44.2", {"start": v(49.07, -58.48) * mm, "end": v(49.82, -59.42) * mm});
            skArc(sketch, "E13.44.3", {"start": v(48.93, -58.24) * mm, "mid": v(49, -58.37) * mm, "end": v(49.07, -58.48) * mm});
            skArc(sketch, "E13.44.4", {"start": v(48.73, -55.83) * mm, "mid": v(48.49, -56.18) * mm, "end": v(48.47, -56.61) * mm});
            skLineSegment(sketch, "E13.44.5", {"start": v(48.73, -55.83) * mm, "end": v(48.93, -55.66) * mm});
            skLineSegment(sketch, "E13.44.6", {"start": v(49.14, -55.5) * mm, "end": v(48.93, -55.66) * mm});
            skArc(sketch, "E13.44.7", {"start": v(49.97, -55.41) * mm, "mid": v(49.54, -55.34) * mm, "end": v(49.14, -55.5) * mm});
            skArc(sketch, "E13.44.8", {"start": v(51.45, -56.22) * mm, "mid": v(50.72, -55.8) * mm, "end": v(49.97, -55.41) * mm});
            skArc(sketch, "E13.44.9", {"start": v(51.66, -56.4) * mm, "mid": v(51.56, -56.3) * mm, "end": v(51.45, -56.22) * mm});
            skLineSegment(sketch, "E13.44.10", {"start": v(51.66, -56.4) * mm, "end": v(52.28, -57.17) * mm});
            skArc(sketch, "E13.44.11", {"start": v(52.28, -57.17) * mm, "mid": v(52.84, -57.47) * mm, "end": v(53.43, -57.26) * mm});
            skArc(sketch, "E13.45.0", {"start": v(54.8, -55.96) * mm, "mid": v(55.03, -55.4) * mm, "end": v(54.8, -54.85) * mm});
            skArc(sketch, "E13.45.1", {"start": v(53.82, -53.75) * mm, "mid": v(53.5, -52.97) * mm, "end": v(53.22, -52.17) * mm});
            skLineSegment(sketch, "E13.45.2", {"start": v(53.98, -53.98) * mm, "end": v(54.8, -54.85) * mm});
            skArc(sketch, "E13.45.3", {"start": v(53.82, -53.75) * mm, "mid": v(53.9, -53.87) * mm, "end": v(53.98, -53.98) * mm});
            skArc(sketch, "E13.45.4", {"start": v(53.4, -51.37) * mm, "mid": v(53.2, -51.74) * mm, "end": v(53.22, -52.17) * mm});
            skLineSegment(sketch, "E13.45.5", {"start": v(53.4, -51.37) * mm, "end": v(53.6, -51.18) * mm});
            skLineSegment(sketch, "E13.45.6", {"start": v(53.8, -51) * mm, "end": v(53.6, -51.18) * mm});
            skArc(sketch, "E13.45.7", {"start": v(54.6, -50.85) * mm, "mid": v(54.18, -50.8) * mm, "end": v(53.8, -51) * mm});
            skArc(sketch, "E13.45.8", {"start": v(56.16, -51.52) * mm, "mid": v(55.39, -51.17) * mm, "end": v(54.6, -50.85) * mm});
            skArc(sketch, "E13.45.9", {"start": v(56.38, -51.68) * mm, "mid": v(56.27, -51.6) * mm, "end": v(56.16, -51.52) * mm});
            skLineSegment(sketch, "E13.45.10", {"start": v(56.38, -51.68) * mm, "end": v(57.07, -52.4) * mm});
            skArc(sketch, "E13.45.11", {"start": v(57.07, -52.4) * mm, "mid": v(57.65, -52.64) * mm, "end": v(58.22, -52.38) * mm});
            skArc(sketch, "E13.46.0", {"start": v(59.46, -50.97) * mm, "mid": v(59.65, -50.4) * mm, "end": v(59.38, -49.87) * mm});
            skArc(sketch, "E13.46.1", {"start": v(58.3, -48.86) * mm, "mid": v(57.92, -48.1) * mm, "end": v(57.56, -47.34) * mm});
            skLineSegment(sketch, "E13.46.2", {"start": v(58.48, -49.07) * mm, "end": v(59.38, -49.87) * mm});
            skArc(sketch, "E13.46.3", {"start": v(58.3, -48.86) * mm, "mid": v(58.38, -48.97) * mm, "end": v(58.48, -49.07) * mm});
            skArc(sketch, "E13.46.4", {"start": v(57.68, -46.52) * mm, "mid": v(57.5, -46.91) * mm, "end": v(57.56, -47.34) * mm});
            skLineSegment(sketch, "E13.46.5", {"start": v(57.68, -46.52) * mm, "end": v(57.85, -46.31) * mm});
            skLineSegment(sketch, "E13.46.6", {"start": v(58.03, -46.12) * mm, "end": v(57.85, -46.31) * mm});
            skArc(sketch, "E13.46.7", {"start": v(58.83, -45.9) * mm, "mid": v(58.4, -45.9) * mm, "end": v(58.03, -46.12) * mm});
            skArc(sketch, "E13.46.8", {"start": v(60.43, -46.43) * mm, "mid": v(59.64, -46.14) * mm, "end": v(58.83, -45.9) * mm});
            skArc(sketch, "E13.46.9", {"start": v(60.67, -46.57) * mm, "mid": v(60.56, -46.5) * mm, "end": v(60.43, -46.43) * mm});
            skLineSegment(sketch, "E13.46.10", {"start": v(60.67, -46.57) * mm, "end": v(61.42, -47.23) * mm});
            skArc(sketch, "E13.46.11", {"start": v(61.42, -47.23) * mm, "mid": v(62.02, -47.42) * mm, "end": v(62.56, -47.1) * mm});
            skArc(sketch, "E13.47.0", {"start": v(63.68, -45.6) * mm, "mid": v(63.81, -45.01) * mm, "end": v(63.5, -44.5) * mm});
            skArc(sketch, "E13.47.1", {"start": v(62.34, -43.59) * mm, "mid": v(61.89, -42.87) * mm, "end": v(61.47, -42.14) * mm});
            skLineSegment(sketch, "E13.47.2", {"start": v(62.53, -43.79) * mm, "end": v(63.5, -44.5) * mm});
            skArc(sketch, "E13.47.3", {"start": v(62.34, -43.59) * mm, "mid": v(62.43, -43.7) * mm, "end": v(62.53, -43.79) * mm});
            skArc(sketch, "E13.47.4", {"start": v(61.52, -41.31) * mm, "mid": v(61.38, -41.72) * mm, "end": v(61.47, -42.14) * mm});
            skLineSegment(sketch, "E13.47.5", {"start": v(61.52, -41.31) * mm, "end": v(61.67, -41.1) * mm});
            skLineSegment(sketch, "E13.47.6", {"start": v(61.83, -40.89) * mm, "end": v(61.67, -41.1) * mm});
            skArc(sketch, "E13.47.7", {"start": v(62.6, -40.6) * mm, "mid": v(62.18, -40.63) * mm, "end": v(61.83, -40.89) * mm});
            skArc(sketch, "E13.47.8", {"start": v(64.25, -40.99) * mm, "mid": v(63.43, -40.77) * mm, "end": v(62.6, -40.6) * mm});
            skArc(sketch, "E13.47.9", {"start": v(64.5, -41.1) * mm, "mid": v(64.38, -41.04) * mm, "end": v(64.25, -40.99) * mm});
            skLineSegment(sketch, "E13.47.10", {"start": v(64.5, -41.1) * mm, "end": v(65.3, -41.7) * mm});
            skArc(sketch, "E13.47.11", {"start": v(65.3, -41.7) * mm, "mid": v(65.91, -41.83) * mm, "end": v(66.43, -41.48) * mm});
            skArc(sketch, "E13.48.0", {"start": v(67.4, -39.87) * mm, "mid": v(67.5, -39.28) * mm, "end": v(67.14, -38.8) * mm});
            skArc(sketch, "E13.48.1", {"start": v(65.9, -37.99) * mm, "mid": v(65.4, -37.32) * mm, "end": v(64.9, -36.62) * mm});
            skLineSegment(sketch, "E13.48.2", {"start": v(66.1, -38.17) * mm, "end": v(67.14, -38.8) * mm});
            skArc(sketch, "E13.48.3", {"start": v(65.9, -37.99) * mm, "mid": v(66, -38.09) * mm, "end": v(66.1, -38.17) * mm});
            skArc(sketch, "E13.48.4", {"start": v(64.88, -35.8) * mm, "mid": v(64.78, -36.21) * mm, "end": v(64.9, -36.62) * mm});
            skLineSegment(sketch, "E13.48.5", {"start": v(64.88, -35.8) * mm, "end": v(65.02, -35.56) * mm});
            skLineSegment(sketch, "E13.48.6", {"start": v(65.16, -35.34) * mm, "end": v(65.02, -35.56) * mm});
            skArc(sketch, "E13.48.7", {"start": v(65.9, -34.98) * mm, "mid": v(65.48, -35.05) * mm, "end": v(65.16, -35.34) * mm});
            skArc(sketch, "E13.48.8", {"start": v(67.58, -35.23) * mm, "mid": v(66.74, -35.09) * mm, "end": v(65.9, -34.98) * mm});
            skArc(sketch, "E13.48.9", {"start": v(67.83, -35.33) * mm, "mid": v(67.71, -35.27) * mm, "end": v(67.58, -35.23) * mm});
            skLineSegment(sketch, "E13.48.10", {"start": v(67.83, -35.33) * mm, "end": v(68.68, -35.85) * mm});
            skArc(sketch, "E13.48.11", {"start": v(68.68, -35.85) * mm, "mid": v(69.3, -35.93) * mm, "end": v(69.8, -35.53) * mm});
            skArc(sketch, "E13.49.0", {"start": v(70.63, -33.84) * mm, "mid": v(70.66, -33.25) * mm, "end": v(70.26, -32.8) * mm});
            skArc(sketch, "E13.49.1", {"start": v(68.96, -32.1) * mm, "mid": v(68.4, -31.48) * mm, "end": v(67.85, -30.83) * mm});
            skLineSegment(sketch, "E13.49.2", {"start": v(69.19, -32.26) * mm, "end": v(70.26, -32.8) * mm});
            skArc(sketch, "E13.49.3", {"start": v(68.96, -32.1) * mm, "mid": v(69.07, -32.2) * mm, "end": v(69.19, -32.26) * mm});
            skArc(sketch, "E13.49.4", {"start": v(67.76, -30) * mm, "mid": v(67.69, -30.43) * mm, "end": v(67.85, -30.83) * mm});
            skLineSegment(sketch, "E13.49.5", {"start": v(67.76, -30) * mm, "end": v(67.87, -29.76) * mm});
            skLineSegment(sketch, "E13.49.6", {"start": v(68, -29.53) * mm, "end": v(67.87, -29.76) * mm});
            skArc(sketch, "E13.49.7", {"start": v(68.7, -29.1) * mm, "mid": v(68.29, -29.21) * mm, "end": v(68, -29.53) * mm});
            skArc(sketch, "E13.49.8", {"start": v(70.4, -29.2) * mm, "mid": v(69.55, -29.14) * mm, "end": v(68.7, -29.1) * mm});
            skArc(sketch, "E13.49.9", {"start": v(70.66, -29.28) * mm, "mid": v(70.53, -29.23) * mm, "end": v(70.4, -29.2) * mm});
            skLineSegment(sketch, "E13.49.10", {"start": v(70.66, -29.28) * mm, "end": v(71.55, -29.72) * mm});
            skArc(sketch, "E13.49.11", {"start": v(71.55, -29.72) * mm, "mid": v(72.18, -29.75) * mm, "end": v(72.62, -29.31) * mm});
            skArc(sketch, "E13.50.0", {"start": v(73.3, -27.56) * mm, "mid": v(73.29, -26.96) * mm, "end": v(72.86, -26.55) * mm});
            skArc(sketch, "E13.50.1", {"start": v(71.5, -25.97) * mm, "mid": v(70.88, -25.4) * mm, "end": v(70.28, -24.8) * mm});
            skLineSegment(sketch, "E13.50.2", {"start": v(71.73, -26.11) * mm, "end": v(72.86, -26.55) * mm});
            skArc(sketch, "E13.50.3", {"start": v(71.5, -25.97) * mm, "mid": v(71.6, -26.05) * mm, "end": v(71.73, -26.11) * mm});
            skArc(sketch, "E13.50.4", {"start": v(70.11, -23.98) * mm, "mid": v(70.08, -24.41) * mm, "end": v(70.28, -24.8) * mm});
            skLineSegment(sketch, "E13.50.5", {"start": v(70.11, -23.98) * mm, "end": v(70.2, -23.73) * mm});
            skLineSegment(sketch, "E13.50.6", {"start": v(70.3, -23.49) * mm, "end": v(70.2, -23.73) * mm});
            skArc(sketch, "E13.50.7", {"start": v(70.98, -23) * mm, "mid": v(70.57, -23.15) * mm, "end": v(70.3, -23.49) * mm});
            skArc(sketch, "E13.50.8", {"start": v(72.67, -22.96) * mm, "mid": v(71.82, -22.96) * mm, "end": v(70.98, -23) * mm});
            skArc(sketch, "E13.50.9", {"start": v(72.94, -23.01) * mm, "mid": v(72.8, -22.98) * mm, "end": v(72.67, -22.96) * mm});
            skLineSegment(sketch, "E13.50.10", {"start": v(72.94, -23.01) * mm, "end": v(73.86, -23.37) * mm});
            skArc(sketch, "E13.50.11", {"start": v(73.86, -23.37) * mm, "mid": v(74.5, -23.35) * mm, "end": v(74.9, -22.87) * mm});
            skArc(sketch, "E13.51.0", {"start": v(75.43, -21.07) * mm, "mid": v(75.36, -20.47) * mm, "end": v(74.9, -20.1) * mm});
            skArc(sketch, "E13.51.1", {"start": v(73.49, -19.64) * mm, "mid": v(72.82, -19.12) * mm, "end": v(72.18, -18.58) * mm});
            skLineSegment(sketch, "E13.51.2", {"start": v(73.74, -19.76) * mm, "end": v(74.9, -20.1) * mm});
            skArc(sketch, "E13.51.3", {"start": v(73.49, -19.64) * mm, "mid": v(73.6, -19.71) * mm, "end": v(73.74, -19.76) * mm});
            skArc(sketch, "E13.51.4", {"start": v(71.94, -17.78) * mm, "mid": v(71.94, -18.21) * mm, "end": v(72.18, -18.58) * mm});
            skLineSegment(sketch, "E13.51.5", {"start": v(71.94, -17.78) * mm, "end": v(72, -17.53) * mm});
            skLineSegment(sketch, "E13.51.6", {"start": v(72.09, -17.27) * mm, "end": v(72, -17.53) * mm});
            skArc(sketch, "E13.51.7", {"start": v(72.71, -16.73) * mm, "mid": v(72.32, -16.91) * mm, "end": v(72.09, -17.27) * mm});
            skArc(sketch, "E13.51.8", {"start": v(74.4, -16.54) * mm, "mid": v(73.55, -16.62) * mm, "end": v(72.71, -16.73) * mm});
            skArc(sketch, "E13.51.9", {"start": v(74.67, -16.57) * mm, "mid": v(74.53, -16.54) * mm, "end": v(74.4, -16.54) * mm});
            skLineSegment(sketch, "E13.51.10", {"start": v(74.67, -16.57) * mm, "end": v(75.62, -16.85) * mm});
            skArc(sketch, "E13.51.11", {"start": v(75.62, -16.85) * mm, "mid": v(76.25, -16.77) * mm, "end": v(76.61, -16.25) * mm});
            skArc(sketch, "E13.52.0", {"start": v(76.98, -14.41) * mm, "mid": v(76.86, -13.83) * mm, "end": v(76.36, -13.5) * mm});
            skArc(sketch, "E13.52.1", {"start": v(74.92, -13.16) * mm, "mid": v(74.21, -12.7) * mm, "end": v(73.52, -12.21) * mm});
            skLineSegment(sketch, "E13.52.2", {"start": v(75.18, -13.26) * mm, "end": v(76.36, -13.5) * mm});
            skArc(sketch, "E13.52.3", {"start": v(74.92, -13.16) * mm, "mid": v(75.05, -13.22) * mm, "end": v(75.18, -13.26) * mm});
            skArc(sketch, "E13.52.4", {"start": v(73.21, -11.44) * mm, "mid": v(73.26, -11.87) * mm, "end": v(73.52, -12.21) * mm});
            skLineSegment(sketch, "E13.52.5", {"start": v(73.21, -11.44) * mm, "end": v(73.26, -11.18) * mm});
            skLineSegment(sketch, "E13.52.6", {"start": v(73.32, -10.92) * mm, "end": v(73.26, -11.18) * mm});
            skArc(sketch, "E13.52.7", {"start": v(73.9, -10.33) * mm, "mid": v(73.52, -10.54) * mm, "end": v(73.32, -10.92) * mm});
            skArc(sketch, "E13.52.8", {"start": v(75.55, -10) * mm, "mid": v(74.72, -10.14) * mm, "end": v(73.9, -10.33) * mm});
            skArc(sketch, "E13.52.9", {"start": v(75.83, -10) * mm, "mid": v(75.69, -9.98) * mm, "end": v(75.55, -10) * mm});
            skLineSegment(sketch, "E13.52.10", {"start": v(75.83, -10) * mm, "end": v(76.8, -10.2) * mm});
            skArc(sketch, "E13.52.11", {"start": v(76.8, -10.2) * mm, "mid": v(77.42, -10.06) * mm, "end": v(77.74, -9.52) * mm});
            skArc(sketch, "E13.53.0", {"start": v(77.94, -7.65) * mm, "mid": v(77.77, -7.07) * mm, "end": v(77.24, -6.79) * mm});
            skArc(sketch, "E13.53.1", {"start": v(75.78, -6.58) * mm, "mid": v(75.04, -6.19) * mm, "end": v(74.3, -5.76) * mm});
            skLineSegment(sketch, "E13.53.2", {"start": v(76.05, -6.66) * mm, "end": v(77.24, -6.79) * mm});
            skArc(sketch, "E13.53.3", {"start": v(75.78, -6.58) * mm, "mid": v(75.91, -6.63) * mm, "end": v(76.05, -6.66) * mm});
            skArc(sketch, "E13.53.4", {"start": v(73.93, -5.02) * mm, "mid": v(74.01, -5.44) * mm, "end": v(74.3, -5.76) * mm});
            skLineSegment(sketch, "E13.53.5", {"start": v(73.93, -5.02) * mm, "end": v(73.96, -4.76) * mm});
            skLineSegment(sketch, "E13.53.6", {"start": v(74, -4.5) * mm, "end": v(73.96, -4.76) * mm});
            skArc(sketch, "E13.53.7", {"start": v(74.51, -3.85) * mm, "mid": v(74.16, -4.1) * mm, "end": v(74, -4.5) * mm});
            skArc(sketch, "E13.53.8", {"start": v(76.13, -3.37) * mm, "mid": v(75.32, -3.6) * mm, "end": v(74.51, -3.85) * mm});
            skArc(sketch, "E13.53.9", {"start": v(76.4, -3.35) * mm, "mid": v(76.27, -3.35) * mm, "end": v(76.13, -3.37) * mm});
            skLineSegment(sketch, "E13.53.10", {"start": v(76.4, -3.35) * mm, "end": v(77.4, -3.46) * mm});
            skArc(sketch, "E13.53.11", {"start": v(77.4, -3.46) * mm, "mid": v(78, -3.27) * mm, "end": v(78.27, -2.7) * mm});
            skArc(sketch, "E13.54.0", {"start": v(78.31, -0.82) * mm, "mid": v(78.1, -0.27) * mm, "end": v(77.54, -0.03) * mm});
            skArc(sketch, "E13.54.1", {"start": v(76.07, 0.05) * mm, "mid": v(75.29, 0.38) * mm, "end": v(74.52, 0.74) * mm});
            skLineSegment(sketch, "E13.54.2", {"start": v(76.34, 0) * mm, "end": v(77.54, -0.03) * mm});
            skArc(sketch, "E13.54.3", {"start": v(76.07, 0.05) * mm, "mid": v(76.2, 0.01) * mm, "end": v(76.34, 0) * mm});
            skArc(sketch, "E13.54.4", {"start": v(74.09, 1.44) * mm, "mid": v(74.2, 1.03) * mm, "end": v(74.52, 0.74) * mm});
            skLineSegment(sketch, "E13.54.5", {"start": v(74.09, 1.44) * mm, "end": v(74.09, 1.7) * mm});
            skLineSegment(sketch, "E13.54.6", {"start": v(74.1, 1.97) * mm, "end": v(74.09, 1.7) * mm});
            skArc(sketch, "E13.54.7", {"start": v(74.57, 2.66) * mm, "mid": v(74.24, 2.38) * mm, "end": v(74.1, 1.97) * mm});
            skArc(sketch, "E13.54.8", {"start": v(76.14, 3.28) * mm, "mid": v(75.35, 2.99) * mm, "end": v(74.57, 2.66) * mm});
            skArc(sketch, "E13.54.9", {"start": v(76.41, 3.32) * mm, "mid": v(76.27, 3.31) * mm, "end": v(76.14, 3.28) * mm});
            skLineSegment(sketch, "E13.54.10", {"start": v(76.41, 3.32) * mm, "end": v(77.4, 3.3) * mm});
            skArc(sketch, "E13.54.11", {"start": v(77.4, 3.3) * mm, "mid": v(77.99, 3.54) * mm, "end": v(78.2, 4.13) * mm});
            skArc(sketch, "E13.55.0", {"start": v(78.09, 6) * mm, "mid": v(77.82, 6.54) * mm, "end": v(77.25, 6.73) * mm});
            skArc(sketch, "E13.55.1", {"start": v(75.77, 6.68) * mm, "mid": v(74.97, 6.94) * mm, "end": v(74.18, 7.23) * mm});
            skLineSegment(sketch, "E13.55.2", {"start": v(76.05, 6.65) * mm, "end": v(77.25, 6.73) * mm});
            skArc(sketch, "E13.55.3", {"start": v(75.77, 6.68) * mm, "mid": v(75.9, 6.65) * mm, "end": v(76.05, 6.65) * mm});
            skArc(sketch, "E13.55.4", {"start": v(73.68, 7.9) * mm, "mid": v(73.83, 7.5) * mm, "end": v(74.18, 7.23) * mm});
            skLineSegment(sketch, "E13.55.5", {"start": v(73.68, 7.9) * mm, "end": v(73.66, 8.16) * mm});
            skLineSegment(sketch, "E13.55.6", {"start": v(73.65, 8.43) * mm, "end": v(73.66, 8.16) * mm});
            skArc(sketch, "E13.55.7", {"start": v(74.05, 9.15) * mm, "mid": v(73.75, 8.84) * mm, "end": v(73.65, 8.43) * mm});
            skArc(sketch, "E13.55.8", {"start": v(75.56, 9.9) * mm, "mid": v(74.8, 9.54) * mm, "end": v(74.05, 9.15) * mm});
            skArc(sketch, "E13.55.9", {"start": v(75.83, 9.97) * mm, "mid": v(75.7, 9.95) * mm, "end": v(75.56, 9.9) * mm});
            skLineSegment(sketch, "E13.55.10", {"start": v(75.83, 9.97) * mm, "end": v(76.82, 10.03) * mm});
            skArc(sketch, "E13.55.11", {"start": v(76.82, 10.03) * mm, "mid": v(77.38, 10.32) * mm, "end": v(77.55, 10.93) * mm});
            skArc(sketch, "E13.56.0", {"start": v(77.27, 12.79) * mm, "mid": v(76.95, 13.3) * mm, "end": v(76.37, 13.44) * mm});
            skArc(sketch, "E13.56.1", {"start": v(74.9, 13.26) * mm, "mid": v(74.08, 13.45) * mm, "end": v(73.26, 13.67) * mm});
            skLineSegment(sketch, "E13.56.2", {"start": v(75.18, 13.25) * mm, "end": v(76.37, 13.44) * mm});
            skArc(sketch, "E13.56.3", {"start": v(74.9, 13.26) * mm, "mid": v(75.04, 13.24) * mm, "end": v(75.18, 13.25) * mm});
            skArc(sketch, "E13.56.4", {"start": v(72.71, 14.29) * mm, "mid": v(72.9, 13.9) * mm, "end": v(73.26, 13.67) * mm});
            skLineSegment(sketch, "E13.56.5", {"start": v(72.71, 14.29) * mm, "end": v(72.67, 14.55) * mm});
            skLineSegment(sketch, "E13.56.6", {"start": v(72.63, 14.81) * mm, "end": v(72.67, 14.55) * mm});
            skArc(sketch, "E13.56.7", {"start": v(72.97, 15.57) * mm, "mid": v(72.7, 15.24) * mm, "end": v(72.63, 14.81) * mm});
            skArc(sketch, "E13.56.8", {"start": v(74.41, 16.45) * mm, "mid": v(73.68, 16.02) * mm, "end": v(72.97, 15.57) * mm});
            skArc(sketch, "E13.56.9", {"start": v(74.67, 16.54) * mm, "mid": v(74.54, 16.5) * mm, "end": v(74.41, 16.45) * mm});
            skLineSegment(sketch, "E13.56.10", {"start": v(74.67, 16.54) * mm, "end": v(75.66, 16.7) * mm});
            skArc(sketch, "E13.56.11", {"start": v(75.66, 16.7) * mm, "mid": v(76.19, 17.03) * mm, "end": v(76.3, 17.65) * mm});
            skArc(sketch, "E13.57.0", {"start": v(75.86, 19.47) * mm, "mid": v(75.5, 19.95) * mm, "end": v(74.9, 20.04) * mm});
            skArc(sketch, "E13.57.1", {"start": v(73.46, 19.74) * mm, "mid": v(72.63, 19.85) * mm, "end": v(71.8, 20) * mm});
            skLineSegment(sketch, "E13.57.2", {"start": v(73.74, 19.76) * mm, "end": v(74.9, 20.04) * mm});
            skArc(sketch, "E13.57.3", {"start": v(73.46, 19.74) * mm, "mid": v(73.6, 19.73) * mm, "end": v(73.74, 19.76) * mm});
            skArc(sketch, "E13.57.4", {"start": v(71.2, 20.57) * mm, "mid": v(71.41, 20.2) * mm, "end": v(71.8, 20) * mm});
            skLineSegment(sketch, "E13.57.5", {"start": v(71.2, 20.57) * mm, "end": v(71.12, 20.83) * mm});
            skLineSegment(sketch, "E13.57.6", {"start": v(71.06, 21.09) * mm, "end": v(71.12, 20.83) * mm});
            skArc(sketch, "E13.57.7", {"start": v(71.34, 21.87) * mm, "mid": v(71.1, 21.52) * mm, "end": v(71.06, 21.09) * mm});
            skArc(sketch, "E13.57.8", {"start": v(72.7, 22.87) * mm, "mid": v(72, 22.39) * mm, "end": v(71.34, 21.87) * mm});
            skArc(sketch, "E13.57.9", {"start": v(72.95, 22.98) * mm, "mid": v(72.82, 22.94) * mm, "end": v(72.7, 22.87) * mm});
            skLineSegment(sketch, "E13.57.10", {"start": v(72.95, 22.98) * mm, "end": v(73.91, 23.22) * mm});
            skArc(sketch, "E13.57.11", {"start": v(73.91, 23.22) * mm, "mid": v(74.41, 23.6) * mm, "end": v(74.47, 24.23) * mm});
            skArc(sketch, "E13.58.0", {"start": v(73.87, 26) * mm, "mid": v(73.47, 26.46) * mm, "end": v(72.88, 26.5) * mm});
            skArc(sketch, "E13.58.1", {"start": v(71.46, 26.07) * mm, "mid": v(70.62, 26.1) * mm, "end": v(69.78, 26.18) * mm});
            skLineSegment(sketch, "E13.58.2", {"start": v(71.74, 26.1) * mm, "end": v(72.88, 26.5) * mm});
            skArc(sketch, "E13.58.3", {"start": v(71.46, 26.07) * mm, "mid": v(71.6, 26.07) * mm, "end": v(71.74, 26.1) * mm});
            skArc(sketch, "E13.58.4", {"start": v(69.13, 26.7) * mm, "mid": v(69.38, 26.35) * mm, "end": v(69.78, 26.18) * mm});
            skLineSegment(sketch, "E13.58.5", {"start": v(69.13, 26.7) * mm, "end": v(69.04, 26.95) * mm});
            skLineSegment(sketch, "E13.58.6", {"start": v(68.96, 27.2) * mm, "end": v(69.04, 26.95) * mm});
            skArc(sketch, "E13.58.7", {"start": v(69.16, 28) * mm, "mid": v(68.94, 27.63) * mm, "end": v(68.96, 27.2) * mm});
            skArc(sketch, "E13.58.8", {"start": v(70.43, 29.12) * mm, "mid": v(69.78, 28.58) * mm, "end": v(69.16, 28) * mm});
            skArc(sketch, "E13.58.9", {"start": v(70.67, 29.25) * mm, "mid": v(70.54, 29.2) * mm, "end": v(70.43, 29.12) * mm});
            skLineSegment(sketch, "E13.58.10", {"start": v(70.67, 29.25) * mm, "end": v(71.6, 29.57) * mm});
            skArc(sketch, "E13.58.11", {"start": v(71.6, 29.57) * mm, "mid": v(72.07, 30) * mm, "end": v(72.08, 30.63) * mm});
            skArc(sketch, "E13.59.0", {"start": v(71.32, 32.35) * mm, "mid": v(70.89, 32.76) * mm, "end": v(70.29, 32.74) * mm});
            skArc(sketch, "E13.59.1", {"start": v(68.92, 32.2) * mm, "mid": v(68.08, 32.16) * mm, "end": v(67.23, 32.16) * mm});
            skLineSegment(sketch, "E13.59.2", {"start": v(69.19, 32.26) * mm, "end": v(70.29, 32.74) * mm});
            skArc(sketch, "E13.59.3", {"start": v(68.92, 32.2) * mm, "mid": v(69.06, 32.21) * mm, "end": v(69.19, 32.26) * mm});
            skArc(sketch, "E13.59.4", {"start": v(66.54, 32.62) * mm, "mid": v(66.82, 32.3) * mm, "end": v(67.23, 32.16) * mm});
            skLineSegment(sketch, "E13.59.5", {"start": v(66.54, 32.62) * mm, "end": v(66.43, 32.86) * mm});
            skLineSegment(sketch, "E13.59.6", {"start": v(66.32, 33.1) * mm, "end": v(66.43, 32.86) * mm});
            skArc(sketch, "E13.59.7", {"start": v(66.46, 33.92) * mm, "mid": v(66.27, 33.53) * mm, "end": v(66.32, 33.1) * mm});
            skArc(sketch, "E13.59.8", {"start": v(67.62, 35.15) * mm, "mid": v(67.02, 34.55) * mm, "end": v(66.46, 33.92) * mm});
            skArc(sketch, "E13.59.9", {"start": v(67.85, 35.3) * mm, "mid": v(67.73, 35.24) * mm, "end": v(67.62, 35.15) * mm});
            skLineSegment(sketch, "E13.59.10", {"start": v(67.85, 35.3) * mm, "end": v(68.76, 35.7) * mm});
            skArc(sketch, "E13.59.11", {"start": v(68.76, 35.7) * mm, "mid": v(69.18, 36.17) * mm, "end": v(69.14, 36.8) * mm});
            skArc(sketch, "E13.60.0", {"start": v(68.23, 38.44) * mm, "mid": v(67.76, 38.81) * mm, "end": v(67.17, 38.75) * mm});
            skArc(sketch, "E13.60.1", {"start": v(65.85, 38.08) * mm, "mid": v(65.01, 37.97) * mm, "end": v(64.17, 37.9) * mm});
            skLineSegment(sketch, "E13.60.2", {"start": v(66.11, 38.17) * mm, "end": v(67.17, 38.75) * mm});
            skArc(sketch, "E13.60.3", {"start": v(65.85, 38.08) * mm, "mid": v(65.99, 38.11) * mm, "end": v(66.11, 38.17) * mm});
            skArc(sketch, "E13.60.4", {"start": v(63.44, 38.3) * mm, "mid": v(63.75, 38) * mm, "end": v(64.17, 37.9) * mm});
            skLineSegment(sketch, "E13.60.5", {"start": v(63.44, 38.3) * mm, "end": v(63.3, 38.52) * mm});
            skLineSegment(sketch, "E13.60.6", {"start": v(63.19, 38.76) * mm, "end": v(63.3, 38.52) * mm});
            skArc(sketch, "E13.60.7", {"start": v(63.25, 39.59) * mm, "mid": v(63.1, 39.18) * mm, "end": v(63.19, 38.76) * mm});
            skArc(sketch, "E13.60.8", {"start": v(64.3, 40.9) * mm, "mid": v(63.76, 40.26) * mm, "end": v(63.25, 39.59) * mm});
            skArc(sketch, "E13.60.9", {"start": v(64.51, 41.08) * mm, "mid": v(64.4, 41) * mm, "end": v(64.3, 40.9) * mm});
            skLineSegment(sketch, "E13.60.10", {"start": v(64.51, 41.08) * mm, "end": v(65.38, 41.56) * mm});
            skArc(sketch, "E13.60.11", {"start": v(65.38, 41.56) * mm, "mid": v(65.77, 42.06) * mm, "end": v(65.67, 42.68) * mm});
            skArc(sketch, "E13.61.0", {"start": v(64.62, 44.24) * mm, "mid": v(64.12, 44.57) * mm, "end": v(63.54, 44.45) * mm});
            skArc(sketch, "E13.61.1", {"start": v(62.28, 43.67) * mm, "mid": v(61.46, 43.5) * mm, "end": v(60.62, 43.35) * mm});
            skLineSegment(sketch, "E13.61.2", {"start": v(62.53, 43.78) * mm, "end": v(63.54, 44.45) * mm});
            skArc(sketch, "E13.61.3", {"start": v(62.28, 43.67) * mm, "mid": v(62.41, 43.72) * mm, "end": v(62.53, 43.78) * mm});
            skArc(sketch, "E13.61.4", {"start": v(59.86, 43.68) * mm, "mid": v(60.2, 43.4) * mm, "end": v(60.62, 43.35) * mm});
            skLineSegment(sketch, "E13.61.5", {"start": v(59.86, 43.68) * mm, "end": v(59.71, 43.9) * mm});
            skLineSegment(sketch, "E13.61.6", {"start": v(59.57, 44.12) * mm, "end": v(59.71, 43.9) * mm});
            skArc(sketch, "E13.61.7", {"start": v(59.56, 44.95) * mm, "mid": v(59.44, 44.53) * mm, "end": v(59.57, 44.12) * mm});
            skArc(sketch, "E13.61.8", {"start": v(60.49, 46.36) * mm, "mid": v(60, 45.66) * mm, "end": v(59.56, 44.95) * mm});
            skArc(sketch, "E13.61.9", {"start": v(60.69, 46.55) * mm, "mid": v(60.58, 46.46) * mm, "end": v(60.49, 46.36) * mm});
            skLineSegment(sketch, "E13.61.10", {"start": v(60.69, 46.55) * mm, "end": v(61.51, 47.1) * mm});
            skArc(sketch, "E13.61.11", {"start": v(61.51, 47.1) * mm, "mid": v(61.85, 47.63) * mm, "end": v(61.7, 48.24) * mm});
            skArc(sketch, "E13.62.0", {"start": v(60.52, 49.7) * mm, "mid": v(60, 49.99) * mm, "end": v(59.42, 49.82) * mm});
            skArc(sketch, "E13.62.1", {"start": v(58.24, 48.93) * mm, "mid": v(57.43, 48.68) * mm, "end": v(56.61, 48.47) * mm});
            skLineSegment(sketch, "E13.62.2", {"start": v(58.48, 49.07) * mm, "end": v(59.42, 49.82) * mm});
            skArc(sketch, "E13.62.3", {"start": v(58.24, 48.93) * mm, "mid": v(58.37, 49) * mm, "end": v(58.48, 49.07) * mm});
            skArc(sketch, "E13.62.4", {"start": v(55.83, 48.73) * mm, "mid": v(56.18, 48.49) * mm, "end": v(56.61, 48.47) * mm});
            skLineSegment(sketch, "E13.62.5", {"start": v(55.83, 48.73) * mm, "end": v(55.66, 48.93) * mm});
            skLineSegment(sketch, "E13.62.6", {"start": v(55.5, 49.14) * mm, "end": v(55.66, 48.93) * mm});
            skArc(sketch, "E13.62.7", {"start": v(55.41, 49.97) * mm, "mid": v(55.34, 49.54) * mm, "end": v(55.5, 49.14) * mm});
            skArc(sketch, "E13.62.8", {"start": v(56.22, 51.45) * mm, "mid": v(55.8, 50.72) * mm, "end": v(55.41, 49.97) * mm});
            skArc(sketch, "E13.62.9", {"start": v(56.4, 51.66) * mm, "mid": v(56.3, 51.56) * mm, "end": v(56.22, 51.45) * mm});
            skLineSegment(sketch, "E13.62.10", {"start": v(56.4, 51.66) * mm, "end": v(57.17, 52.28) * mm});
            skArc(sketch, "E13.62.11", {"start": v(57.17, 52.28) * mm, "mid": v(57.47, 52.84) * mm, "end": v(57.26, 53.43) * mm});
            skArc(sketch, "E13.63.0", {"start": v(55.96, 54.8) * mm, "mid": v(55.4, 55.03) * mm, "end": v(54.85, 54.8) * mm});
            skArc(sketch, "E13.63.1", {"start": v(53.75, 53.82) * mm, "mid": v(52.97, 53.5) * mm, "end": v(52.17, 53.22) * mm});
            skLineSegment(sketch, "E13.63.2", {"start": v(53.98, 53.98) * mm, "end": v(54.85, 54.8) * mm});
            skArc(sketch, "E13.63.3", {"start": v(53.75, 53.82) * mm, "mid": v(53.87, 53.9) * mm, "end": v(53.98, 53.98) * mm});
            skArc(sketch, "E13.63.4", {"start": v(51.37, 53.4) * mm, "mid": v(51.74, 53.2) * mm, "end": v(52.17, 53.22) * mm});
            skLineSegment(sketch, "E13.63.5", {"start": v(51.37, 53.4) * mm, "end": v(51.18, 53.6) * mm});
            skLineSegment(sketch, "E13.63.6", {"start": v(51, 53.8) * mm, "end": v(51.18, 53.6) * mm});
            skArc(sketch, "E13.63.7", {"start": v(50.85, 54.6) * mm, "mid": v(50.8, 54.18) * mm, "end": v(51, 53.8) * mm});
            skArc(sketch, "E13.63.8", {"start": v(51.52, 56.16) * mm, "mid": v(51.17, 55.39) * mm, "end": v(50.85, 54.6) * mm});
            skArc(sketch, "E13.63.9", {"start": v(51.68, 56.38) * mm, "mid": v(51.6, 56.27) * mm, "end": v(51.52, 56.16) * mm});
            skLineSegment(sketch, "E13.63.10", {"start": v(51.68, 56.38) * mm, "end": v(52.4, 57.07) * mm});
            skArc(sketch, "E13.63.11", {"start": v(52.4, 57.07) * mm, "mid": v(52.64, 57.65) * mm, "end": v(52.38, 58.22) * mm});
            skArc(sketch, "E13.64.0", {"start": v(50.97, 59.46) * mm, "mid": v(50.4, 59.65) * mm, "end": v(49.87, 59.38) * mm});
            skArc(sketch, "E13.64.1", {"start": v(48.86, 58.3) * mm, "mid": v(48.1, 57.92) * mm, "end": v(47.34, 57.56) * mm});
            skLineSegment(sketch, "E13.64.2", {"start": v(49.07, 58.48) * mm, "end": v(49.87, 59.38) * mm});
            skArc(sketch, "E13.64.3", {"start": v(48.86, 58.3) * mm, "mid": v(48.97, 58.38) * mm, "end": v(49.07, 58.48) * mm});
            skArc(sketch, "E13.64.4", {"start": v(46.52, 57.68) * mm, "mid": v(46.91, 57.5) * mm, "end": v(47.34, 57.56) * mm});
            skLineSegment(sketch, "E13.64.5", {"start": v(46.52, 57.68) * mm, "end": v(46.31, 57.85) * mm});
            skLineSegment(sketch, "E13.64.6", {"start": v(46.12, 58.03) * mm, "end": v(46.31, 57.85) * mm});
            skArc(sketch, "E13.64.7", {"start": v(45.9, 58.83) * mm, "mid": v(45.9, 58.4) * mm, "end": v(46.12, 58.03) * mm});
            skArc(sketch, "E13.64.8", {"start": v(46.43, 60.43) * mm, "mid": v(46.14, 59.64) * mm, "end": v(45.9, 58.83) * mm});
            skArc(sketch, "E13.64.9", {"start": v(46.57, 60.67) * mm, "mid": v(46.5, 60.56) * mm, "end": v(46.43, 60.43) * mm});
            skLineSegment(sketch, "E13.64.10", {"start": v(46.57, 60.67) * mm, "end": v(47.23, 61.42) * mm});
            skArc(sketch, "E13.64.11", {"start": v(47.23, 61.42) * mm, "mid": v(47.42, 62.02) * mm, "end": v(47.1, 62.56) * mm});
            skArc(sketch, "E13.65.0", {"start": v(45.6, 63.68) * mm, "mid": v(45.01, 63.81) * mm, "end": v(44.5, 63.5) * mm});
            skArc(sketch, "E13.65.1", {"start": v(43.59, 62.34) * mm, "mid": v(42.87, 61.89) * mm, "end": v(42.14, 61.47) * mm});
            skLineSegment(sketch, "E13.65.2", {"start": v(43.79, 62.53) * mm, "end": v(44.5, 63.5) * mm});
            skArc(sketch, "E13.65.3", {"start": v(43.59, 62.34) * mm, "mid": v(43.7, 62.43) * mm, "end": v(43.79, 62.53) * mm});
            skArc(sketch, "E13.65.4", {"start": v(41.31, 61.52) * mm, "mid": v(41.72, 61.38) * mm, "end": v(42.14, 61.47) * mm});
            skLineSegment(sketch, "E13.65.5", {"start": v(41.31, 61.52) * mm, "end": v(41.1, 61.67) * mm});
            skLineSegment(sketch, "E13.65.6", {"start": v(40.89, 61.83) * mm, "end": v(41.1, 61.67) * mm});
            skArc(sketch, "E13.65.7", {"start": v(40.6, 62.6) * mm, "mid": v(40.63, 62.18) * mm, "end": v(40.89, 61.83) * mm});
            skArc(sketch, "E13.65.8", {"start": v(40.99, 64.25) * mm, "mid": v(40.77, 63.43) * mm, "end": v(40.6, 62.6) * mm});
            skArc(sketch, "E13.65.9", {"start": v(41.1, 64.5) * mm, "mid": v(41.04, 64.38) * mm, "end": v(40.99, 64.25) * mm});
            skLineSegment(sketch, "E13.65.10", {"start": v(41.1, 64.5) * mm, "end": v(41.7, 65.3) * mm});
            skArc(sketch, "E13.65.11", {"start": v(41.7, 65.3) * mm, "mid": v(41.83, 65.91) * mm, "end": v(41.48, 66.43) * mm});
            skArc(sketch, "E13.66.0", {"start": v(39.87, 67.4) * mm, "mid": v(39.28, 67.5) * mm, "end": v(38.8, 67.14) * mm});
            skArc(sketch, "E13.66.1", {"start": v(37.99, 65.9) * mm, "mid": v(37.32, 65.4) * mm, "end": v(36.62, 64.9) * mm});
            skLineSegment(sketch, "E13.66.2", {"start": v(38.17, 66.1) * mm, "end": v(38.8, 67.14) * mm});
            skArc(sketch, "E13.66.3", {"start": v(37.99, 65.9) * mm, "mid": v(38.09, 66) * mm, "end": v(38.17, 66.1) * mm});
            skArc(sketch, "E13.66.4", {"start": v(35.8, 64.88) * mm, "mid": v(36.21, 64.78) * mm, "end": v(36.62, 64.9) * mm});
            skLineSegment(sketch, "E13.66.5", {"start": v(35.8, 64.88) * mm, "end": v(35.56, 65.02) * mm});
            skLineSegment(sketch, "E13.66.6", {"start": v(35.34, 65.16) * mm, "end": v(35.56, 65.02) * mm});
            skArc(sketch, "E13.66.7", {"start": v(34.98, 65.9) * mm, "mid": v(35.05, 65.48) * mm, "end": v(35.34, 65.16) * mm});
            skArc(sketch, "E13.66.8", {"start": v(35.23, 67.58) * mm, "mid": v(35.09, 66.74) * mm, "end": v(34.98, 65.9) * mm});
            skArc(sketch, "E13.66.9", {"start": v(35.33, 67.83) * mm, "mid": v(35.27, 67.71) * mm, "end": v(35.23, 67.58) * mm});
            skLineSegment(sketch, "E13.66.10", {"start": v(35.33, 67.83) * mm, "end": v(35.85, 68.68) * mm});
            skArc(sketch, "E13.66.11", {"start": v(35.85, 68.68) * mm, "mid": v(35.93, 69.3) * mm, "end": v(35.53, 69.8) * mm});
            skArc(sketch, "E13.67.0", {"start": v(33.84, 70.63) * mm, "mid": v(33.25, 70.66) * mm, "end": v(32.8, 70.26) * mm});
            skArc(sketch, "E13.67.1", {"start": v(32.1, 68.96) * mm, "mid": v(31.48, 68.4) * mm, "end": v(30.83, 67.85) * mm});
            skLineSegment(sketch, "E13.67.2", {"start": v(32.26, 69.19) * mm, "end": v(32.8, 70.26) * mm});
            skArc(sketch, "E13.67.3", {"start": v(32.1, 68.96) * mm, "mid": v(32.2, 69.07) * mm, "end": v(32.26, 69.19) * mm});
            skArc(sketch, "E13.67.4", {"start": v(30, 67.76) * mm, "mid": v(30.43, 67.69) * mm, "end": v(30.83, 67.85) * mm});
            skLineSegment(sketch, "E13.67.5", {"start": v(30, 67.76) * mm, "end": v(29.76, 67.87) * mm});
            skLineSegment(sketch, "E13.67.6", {"start": v(29.53, 68) * mm, "end": v(29.76, 67.87) * mm});
            skArc(sketch, "E13.67.7", {"start": v(29.1, 68.7) * mm, "mid": v(29.21, 68.29) * mm, "end": v(29.53, 68) * mm});
            skArc(sketch, "E13.67.8", {"start": v(29.2, 70.4) * mm, "mid": v(29.14, 69.55) * mm, "end": v(29.1, 68.7) * mm});
            skArc(sketch, "E13.67.9", {"start": v(29.28, 70.66) * mm, "mid": v(29.23, 70.53) * mm, "end": v(29.2, 70.4) * mm});
            skLineSegment(sketch, "E13.67.10", {"start": v(29.28, 70.66) * mm, "end": v(29.72, 71.55) * mm});
            skArc(sketch, "E13.67.11", {"start": v(29.72, 71.55) * mm, "mid": v(29.75, 72.18) * mm, "end": v(29.31, 72.62) * mm});
            skArc(sketch, "E13.68.0", {"start": v(27.56, 73.3) * mm, "mid": v(26.96, 73.29) * mm, "end": v(26.55, 72.86) * mm});
            skArc(sketch, "E13.68.1", {"start": v(25.97, 71.5) * mm, "mid": v(25.4, 70.88) * mm, "end": v(24.8, 70.28) * mm});
            skLineSegment(sketch, "E13.68.2", {"start": v(26.11, 71.73) * mm, "end": v(26.55, 72.86) * mm});
            skArc(sketch, "E13.68.3", {"start": v(25.97, 71.5) * mm, "mid": v(26.05, 71.6) * mm, "end": v(26.11, 71.73) * mm});
            skArc(sketch, "E13.68.4", {"start": v(23.98, 70.11) * mm, "mid": v(24.41, 70.08) * mm, "end": v(24.8, 70.28) * mm});
            skLineSegment(sketch, "E13.68.5", {"start": v(23.98, 70.11) * mm, "end": v(23.73, 70.2) * mm});
            skLineSegment(sketch, "E13.68.6", {"start": v(23.49, 70.3) * mm, "end": v(23.73, 70.2) * mm});
            skArc(sketch, "E13.68.7", {"start": v(23, 70.98) * mm, "mid": v(23.15, 70.57) * mm, "end": v(23.49, 70.3) * mm});
            skArc(sketch, "E13.68.8", {"start": v(22.96, 72.67) * mm, "mid": v(22.96, 71.82) * mm, "end": v(23, 70.98) * mm});
            skArc(sketch, "E13.68.9", {"start": v(23.01, 72.94) * mm, "mid": v(22.98, 72.8) * mm, "end": v(22.96, 72.67) * mm});
            skLineSegment(sketch, "E13.68.10", {"start": v(23.01, 72.94) * mm, "end": v(23.37, 73.86) * mm});
            skArc(sketch, "E13.68.11", {"start": v(23.37, 73.86) * mm, "mid": v(23.35, 74.5) * mm, "end": v(22.87, 74.9) * mm});
            skArc(sketch, "E13.69.0", {"start": v(21.07, 75.43) * mm, "mid": v(20.47, 75.36) * mm, "end": v(20.1, 74.9) * mm});
            skArc(sketch, "E13.69.1", {"start": v(19.64, 73.49) * mm, "mid": v(19.12, 72.82) * mm, "end": v(18.58, 72.18) * mm});
            skLineSegment(sketch, "E13.69.2", {"start": v(19.76, 73.74) * mm, "end": v(20.1, 74.9) * mm});
            skArc(sketch, "E13.69.3", {"start": v(19.64, 73.49) * mm, "mid": v(19.71, 73.6) * mm, "end": v(19.76, 73.74) * mm});
            skArc(sketch, "E13.69.4", {"start": v(17.78, 71.94) * mm, "mid": v(18.21, 71.94) * mm, "end": v(18.58, 72.18) * mm});
            skLineSegment(sketch, "E13.69.5", {"start": v(17.78, 71.94) * mm, "end": v(17.53, 72) * mm});
            skLineSegment(sketch, "E13.69.6", {"start": v(17.27, 72.09) * mm, "end": v(17.53, 72) * mm});
            skArc(sketch, "E13.69.7", {"start": v(16.73, 72.71) * mm, "mid": v(16.91, 72.32) * mm, "end": v(17.27, 72.09) * mm});
            skArc(sketch, "E13.69.8", {"start": v(16.54, 74.4) * mm, "mid": v(16.62, 73.55) * mm, "end": v(16.73, 72.71) * mm});
            skArc(sketch, "E13.69.9", {"start": v(16.57, 74.67) * mm, "mid": v(16.54, 74.53) * mm, "end": v(16.54, 74.4) * mm});
            skLineSegment(sketch, "E13.69.10", {"start": v(16.57, 74.67) * mm, "end": v(16.85, 75.62) * mm});
            skArc(sketch, "E13.69.11", {"start": v(16.85, 75.62) * mm, "mid": v(16.77, 76.25) * mm, "end": v(16.25, 76.61) * mm});
            skArc(sketch, "E13.70.0", {"start": v(14.41, 76.98) * mm, "mid": v(13.83, 76.86) * mm, "end": v(13.5, 76.36) * mm});
            skArc(sketch, "E13.70.1", {"start": v(13.16, 74.92) * mm, "mid": v(12.7, 74.21) * mm, "end": v(12.21, 73.52) * mm});
            skLineSegment(sketch, "E13.70.2", {"start": v(13.26, 75.18) * mm, "end": v(13.5, 76.36) * mm});
            skArc(sketch, "E13.70.3", {"start": v(13.16, 74.92) * mm, "mid": v(13.22, 75.05) * mm, "end": v(13.26, 75.18) * mm});
            skArc(sketch, "E13.70.4", {"start": v(11.44, 73.21) * mm, "mid": v(11.87, 73.26) * mm, "end": v(12.21, 73.52) * mm});
            skLineSegment(sketch, "E13.70.5", {"start": v(11.44, 73.21) * mm, "end": v(11.18, 73.26) * mm});
            skLineSegment(sketch, "E13.70.6", {"start": v(10.92, 73.32) * mm, "end": v(11.18, 73.26) * mm});
            skArc(sketch, "E13.70.7", {"start": v(10.33, 73.9) * mm, "mid": v(10.54, 73.52) * mm, "end": v(10.92, 73.32) * mm});
            skArc(sketch, "E13.70.8", {"start": v(10, 75.55) * mm, "mid": v(10.14, 74.72) * mm, "end": v(10.33, 73.9) * mm});
            skArc(sketch, "E13.70.9", {"start": v(10, 75.83) * mm, "mid": v(9.98, 75.69) * mm, "end": v(10, 75.55) * mm});
            skLineSegment(sketch, "E13.70.10", {"start": v(10, 75.83) * mm, "end": v(10.2, 76.8) * mm});
            skArc(sketch, "E13.70.11", {"start": v(10.2, 76.8) * mm, "mid": v(10.06, 77.42) * mm, "end": v(9.52, 77.74) * mm});
            skArc(sketch, "E13.71.0", {"start": v(7.65, 77.94) * mm, "mid": v(7.07, 77.77) * mm, "end": v(6.79, 77.24) * mm});
            skArc(sketch, "E13.71.1", {"start": v(6.58, 75.78) * mm, "mid": v(6.19, 75.04) * mm, "end": v(5.76, 74.3) * mm});
            skLineSegment(sketch, "E13.71.2", {"start": v(6.66, 76.05) * mm, "end": v(6.79, 77.24) * mm});
            skArc(sketch, "E13.71.3", {"start": v(6.58, 75.78) * mm, "mid": v(6.63, 75.91) * mm, "end": v(6.66, 76.05) * mm});
            skArc(sketch, "E13.71.4", {"start": v(5.02, 73.93) * mm, "mid": v(5.44, 74.01) * mm, "end": v(5.76, 74.3) * mm});
            skLineSegment(sketch, "E13.71.5", {"start": v(5.02, 73.93) * mm, "end": v(4.76, 73.96) * mm});
            skLineSegment(sketch, "E13.71.6", {"start": v(4.5, 74) * mm, "end": v(4.76, 73.96) * mm});
            skArc(sketch, "E13.71.7", {"start": v(3.85, 74.51) * mm, "mid": v(4.1, 74.16) * mm, "end": v(4.5, 74) * mm});
            skArc(sketch, "E13.71.8", {"start": v(3.37, 76.13) * mm, "mid": v(3.6, 75.32) * mm, "end": v(3.85, 74.51) * mm});
            skArc(sketch, "E13.71.9", {"start": v(3.35, 76.4) * mm, "mid": v(3.35, 76.27) * mm, "end": v(3.37, 76.13) * mm});
            skLineSegment(sketch, "E13.71.10", {"start": v(3.35, 76.4) * mm, "end": v(3.46, 77.4) * mm});
            skArc(sketch, "E13.71.11", {"start": v(3.46, 77.4) * mm, "mid": v(3.27, 78) * mm, "end": v(2.7, 78.27) * mm});
            skArc(sketch, "E14.trimOffspring", {"start": v(-10.93, 77.55) * mm, "mid": v(-11.86, 77.41) * mm, "end": v(-12.79, 77.27) * mm});
            skArc(sketch, "E15.trimOffspring", {"start": v(-17.65, 76.3) * mm, "mid": v(-18.56, 76.09) * mm, "end": v(-19.47, 75.86) * mm});
            skArc(sketch, "E16.trimOffspring", {"start": v(-24.23, 74.47) * mm, "mid": v(-25.12, 74.18) * mm, "end": v(-26, 73.87) * mm});
            skArc(sketch, "E17.trimOffspring", {"start": v(-30.63, 72.08) * mm, "mid": v(-31.5, 71.7) * mm, "end": v(-32.35, 71.32) * mm});
            skArc(sketch, "E18.trimOffspring", {"start": v(-36.8, 69.14) * mm, "mid": v(-37.62, 68.69) * mm, "end": v(-38.44, 68.23) * mm});
            skArc(sketch, "E19.trimOffspring", {"start": v(-42.68, 65.67) * mm, "mid": v(-43.46, 65.15) * mm, "end": v(-44.24, 64.62) * mm});
            skArc(sketch, "E20.trimOffspring", {"start": v(-48.24, 61.7) * mm, "mid": v(-48.98, 61.11) * mm, "end": v(-49.7, 60.52) * mm});
            skArc(sketch, "E21.trimOffspring", {"start": v(-53.43, 57.26) * mm, "mid": v(-54.12, 56.61) * mm, "end": v(-54.8, 55.96) * mm});
            skArc(sketch, "E22.trimOffspring", {"start": v(2.7, 78.27) * mm, "mid": v(1.76, 78.3) * mm, "end": v(0.82, 78.31) * mm});
            skArc(sketch, "E23.trimOffspring", {"start": v(9.52, 77.74) * mm, "mid": v(8.58, 77.85) * mm, "end": v(7.65, 77.94) * mm});
            skArc(sketch, "E24.trimOffspring", {"start": v(16.25, 76.61) * mm, "mid": v(15.33, 76.8) * mm, "end": v(14.41, 76.98) * mm});
            skArc(sketch, "E25.trimOffspring", {"start": v(22.87, 74.9) * mm, "mid": v(21.97, 75.17) * mm, "end": v(21.07, 75.43) * mm});
            skArc(sketch, "E26.trimOffspring", {"start": v(-58.22, 52.38) * mm, "mid": v(-58.84, 51.68) * mm, "end": v(-59.46, 50.97) * mm});
            skArc(sketch, "E27.trimOffspring", {"start": v(-62.56, 47.1) * mm, "mid": v(-63.12, 46.35) * mm, "end": v(-63.68, 45.6) * mm});
            skArc(sketch, "E28.trimOffspring", {"start": v(-66.43, 41.48) * mm, "mid": v(-66.92, 40.68) * mm, "end": v(-67.4, 39.87) * mm});
            skArc(sketch, "E29.trimOffspring", {"start": v(-69.8, 35.53) * mm, "mid": v(-70.22, 34.69) * mm, "end": v(-70.63, 33.84) * mm});
            skArc(sketch, "E30.trimOffspring", {"start": v(-72.62, 29.31) * mm, "mid": v(-72.97, 28.44) * mm, "end": v(-73.3, 27.56) * mm});
            skArc(sketch, "E31.trimOffspring", {"start": v(-74.9, 22.87) * mm, "mid": v(-75.17, 21.97) * mm, "end": v(-75.43, 21.07) * mm});
            skArc(sketch, "E32.trimOffspring", {"start": v(-76.61, 16.25) * mm, "mid": v(-76.8, 15.33) * mm, "end": v(-76.98, 14.41) * mm});
            skArc(sketch, "E33.trimOffspring", {"start": v(-77.74, 9.52) * mm, "mid": v(-77.85, 8.58) * mm, "end": v(-77.94, 7.65) * mm});
            skArc(sketch, "E34.trimOffspring", {"start": v(-78.27, 2.7) * mm, "mid": v(-78.3, 1.76) * mm, "end": v(-78.31, 0.82) * mm});
            skArc(sketch, "E35.trimOffspring", {"start": v(-78.2, -4.13) * mm, "mid": v(-78.15, -5.07) * mm, "end": v(-78.09, -6) * mm});
            skArc(sketch, "E36.trimOffspring", {"start": v(-77.55, -10.93) * mm, "mid": v(-77.41, -11.86) * mm, "end": v(-77.27, -12.79) * mm});
            skArc(sketch, "E37.trimOffspring", {"start": v(-76.3, -17.65) * mm, "mid": v(-76.09, -18.56) * mm, "end": v(-75.86, -19.47) * mm});
            skArc(sketch, "E38.trimOffspring", {"start": v(-74.47, -24.23) * mm, "mid": v(-74.18, -25.12) * mm, "end": v(-73.87, -26) * mm});
            skArc(sketch, "E39.trimOffspring", {"start": v(-72.08, -30.63) * mm, "mid": v(-71.7, -31.5) * mm, "end": v(-71.32, -32.35) * mm});
            skArc(sketch, "E40.trimOffspring", {"start": v(-69.14, -36.8) * mm, "mid": v(-68.69, -37.62) * mm, "end": v(-68.23, -38.44) * mm});
            skArc(sketch, "E41.trimOffspring", {"start": v(-65.67, -42.68) * mm, "mid": v(-65.15, -43.46) * mm, "end": v(-64.62, -44.24) * mm});
            skArc(sketch, "E42.trimOffspring", {"start": v(-61.7, -48.24) * mm, "mid": v(-61.11, -48.98) * mm, "end": v(-60.52, -49.7) * mm});
            skArc(sketch, "E43.trimOffspring", {"start": v(-57.26, -53.43) * mm, "mid": v(-56.61, -54.12) * mm, "end": v(-55.96, -54.8) * mm});
            skArc(sketch, "E44.trimOffspring", {"start": v(-52.38, -58.22) * mm, "mid": v(-51.68, -58.84) * mm, "end": v(-50.97, -59.46) * mm});
            skArc(sketch, "E45.trimOffspring", {"start": v(-47.1, -62.56) * mm, "mid": v(-46.35, -63.12) * mm, "end": v(-45.6, -63.68) * mm});
            skArc(sketch, "E46.trimOffspring", {"start": v(-41.48, -66.43) * mm, "mid": v(-40.68, -66.92) * mm, "end": v(-39.87, -67.4) * mm});
            skArc(sketch, "E47.trimOffspring", {"start": v(-35.53, -69.8) * mm, "mid": v(-34.69, -70.22) * mm, "end": v(-33.84, -70.63) * mm});
            skArc(sketch, "E48.trimOffspring", {"start": v(-29.31, -72.62) * mm, "mid": v(-28.44, -72.97) * mm, "end": v(-27.56, -73.3) * mm});
            skArc(sketch, "E49.trimOffspring", {"start": v(-22.87, -74.9) * mm, "mid": v(-21.97, -75.17) * mm, "end": v(-21.07, -75.43) * mm});
            skArc(sketch, "E50.trimOffspring", {"start": v(-16.25, -76.61) * mm, "mid": v(-15.33, -76.8) * mm, "end": v(-14.41, -76.98) * mm});
            skArc(sketch, "E51.trimOffspring", {"start": v(-9.52, -77.74) * mm, "mid": v(-8.58, -77.85) * mm, "end": v(-7.65, -77.94) * mm});
            skArc(sketch, "E52.trimOffspring", {"start": v(-2.7, -78.27) * mm, "mid": v(-1.76, -78.3) * mm, "end": v(-0.82, -78.31) * mm});
            skArc(sketch, "E53.trimOffspring", {"start": v(4.13, -78.2) * mm, "mid": v(5.07, -78.15) * mm, "end": v(6, -78.09) * mm});
            skArc(sketch, "E54.trimOffspring", {"start": v(10.93, -77.55) * mm, "mid": v(11.86, -77.41) * mm, "end": v(12.79, -77.27) * mm});
            skArc(sketch, "E55.trimOffspring", {"start": v(17.65, -76.3) * mm, "mid": v(18.56, -76.09) * mm, "end": v(19.47, -75.86) * mm});
            skArc(sketch, "E56.trimOffspring", {"start": v(24.23, -74.47) * mm, "mid": v(25.12, -74.18) * mm, "end": v(26, -73.87) * mm});
            skArc(sketch, "E57.trimOffspring", {"start": v(30.63, -72.08) * mm, "mid": v(31.5, -71.7) * mm, "end": v(32.35, -71.32) * mm});
            skArc(sketch, "E58.trimOffspring", {"start": v(36.8, -69.14) * mm, "mid": v(37.62, -68.69) * mm, "end": v(38.44, -68.23) * mm});
            skArc(sketch, "E59.trimOffspring", {"start": v(42.68, -65.67) * mm, "mid": v(43.46, -65.15) * mm, "end": v(44.24, -64.62) * mm});
            skArc(sketch, "E60.trimOffspring", {"start": v(48.24, -61.7) * mm, "mid": v(48.98, -61.11) * mm, "end": v(49.7, -60.52) * mm});
            skArc(sketch, "E61.trimOffspring", {"start": v(53.43, -57.26) * mm, "mid": v(54.12, -56.61) * mm, "end": v(54.8, -55.96) * mm});
            skArc(sketch, "E62.trimOffspring", {"start": v(58.22, -52.38) * mm, "mid": v(58.84, -51.68) * mm, "end": v(59.46, -50.97) * mm});
            skArc(sketch, "E63.trimOffspring", {"start": v(62.56, -47.1) * mm, "mid": v(63.12, -46.35) * mm, "end": v(63.68, -45.6) * mm});
            skArc(sketch, "E64.trimOffspring", {"start": v(66.43, -41.48) * mm, "mid": v(66.92, -40.68) * mm, "end": v(67.4, -39.87) * mm});
            skArc(sketch, "E65.trimOffspring", {"start": v(69.8, -35.53) * mm, "mid": v(70.22, -34.69) * mm, "end": v(70.63, -33.84) * mm});
            skArc(sketch, "E66.trimOffspring", {"start": v(72.62, -29.31) * mm, "mid": v(72.97, -28.44) * mm, "end": v(73.3, -27.56) * mm});
            skArc(sketch, "E67.trimOffspring", {"start": v(74.9, -22.87) * mm, "mid": v(75.17, -21.97) * mm, "end": v(75.43, -21.07) * mm});
            skArc(sketch, "E68.trimOffspring", {"start": v(76.61, -16.25) * mm, "mid": v(76.8, -15.33) * mm, "end": v(76.98, -14.41) * mm});
            skArc(sketch, "E69.trimOffspring", {"start": v(77.74, -9.52) * mm, "mid": v(77.85, -8.58) * mm, "end": v(77.94, -7.65) * mm});
            skArc(sketch, "E70.trimOffspring", {"start": v(78.27, -2.7) * mm, "mid": v(78.3, -1.76) * mm, "end": v(78.31, -0.82) * mm});
            skArc(sketch, "E71.trimOffspring", {"start": v(78.2, 4.13) * mm, "mid": v(78.15, 5.07) * mm, "end": v(78.09, 6) * mm});
            skArc(sketch, "E72.trimOffspring", {"start": v(77.55, 10.93) * mm, "mid": v(77.41, 11.86) * mm, "end": v(77.27, 12.79) * mm});
            skArc(sketch, "E73.trimOffspring", {"start": v(76.3, 17.65) * mm, "mid": v(76.09, 18.56) * mm, "end": v(75.86, 19.47) * mm});
            skArc(sketch, "E74.trimOffspring", {"start": v(74.47, 24.23) * mm, "mid": v(74.18, 25.12) * mm, "end": v(73.87, 26) * mm});
            skArc(sketch, "E75.trimOffspring", {"start": v(72.08, 30.63) * mm, "mid": v(71.7, 31.5) * mm, "end": v(71.32, 32.35) * mm});
            skArc(sketch, "E76.trimOffspring", {"start": v(69.14, 36.8) * mm, "mid": v(68.69, 37.62) * mm, "end": v(68.23, 38.44) * mm});
            skArc(sketch, "E77.trimOffspring", {"start": v(65.67, 42.68) * mm, "mid": v(65.15, 43.46) * mm, "end": v(64.62, 44.24) * mm});
            skArc(sketch, "E78.trimOffspring", {"start": v(61.7, 48.24) * mm, "mid": v(61.11, 48.98) * mm, "end": v(60.52, 49.7) * mm});
            skArc(sketch, "E79.trimOffspring", {"start": v(57.26, 53.43) * mm, "mid": v(56.61, 54.12) * mm, "end": v(55.96, 54.8) * mm});
            skArc(sketch, "E80.trimOffspring", {"start": v(52.38, 58.22) * mm, "mid": v(51.68, 58.84) * mm, "end": v(50.97, 59.46) * mm});
            skArc(sketch, "E81.trimOffspring", {"start": v(47.1, 62.56) * mm, "mid": v(46.35, 63.12) * mm, "end": v(45.6, 63.68) * mm});
            skArc(sketch, "E82.trimOffspring", {"start": v(41.48, 66.43) * mm, "mid": v(40.68, 66.92) * mm, "end": v(39.87, 67.4) * mm});
            skArc(sketch, "E83.trimOffspring", {"start": v(35.53, 69.8) * mm, "mid": v(34.69, 70.22) * mm, "end": v(33.84, 70.63) * mm});
            skArc(sketch, "E84.trimOffspring", {"start": v(29.31, 72.62) * mm, "mid": v(28.44, 72.97) * mm, "end": v(27.56, 73.3) * mm});
            skCircle(sketch, "E85", {"center": v(0, 0) * mm, "radius": 83.64 * mm});
            skSolve(sketch);
        }
        {
            var Q0;
            Q0=makeQuery(id+"F0.imprint","IMPRINT",FACE,{"disambiguationData":[TD([[makeQuery(id+"F0.imprint","IMPRINT",EDGE,{"derivedFrom":sQuery(id+"F0.wireOp",EDGE,"E0")}),1.0]])]});
            extrude(context, id + "F1", {"entities" : qUnion([Q0]), "depth" : 6.35 * mm});
        }
        {
            var Q0;
            Q0=makeQuery(id+"F0.imprint","IMPRINT",FACE,{"disambiguationData":[TD([[makeQuery(id+"F0.imprint","IMPRINT",EDGE,{"derivedFrom":sQuery(id+"F0.wireOp",EDGE,"E0")}),-1.0]])]});
            extrude(context, id + "F2", {"entities" : qUnion([Q0]), "operationType" : NewBodyOperationType.ADD, "depth" : 31.75 * mm});
        }
        {
            var Q0;
            Q0=makeQuery(id+"F1.opExtrude","CAP_FACE",FACE,{"disambiguationData":[OSD([sQuery(id+"F0.wireOp",EDGE,"E0"),sQuery(id+"F0.wireOp",EDGE,"E1.MirrorCS"),sQuery(id+"F0.wireOp",EDGE,"E2.MirrorCS"),sQuery(id+"F0.wireOp",EDGE,"E3.MirrorCS"),sQuery(id+"F0.wireOp",EDGE,"E4.MirrorCS"),sQuery(id+"F0.wireOp",EDGE,"E5.MirrorCS"),sQuery(id+"F0.wireOp",EDGE,"E6.MirrorCS"),sQuery(id+"F0.wireOp",EDGE,"E7.filletArc"),sQuery(id+"F0.wireOp",EDGE,"E8.filletArc"),sQuery(id+"F0.wireOp",EDGE,"E9.filletArc"),sQuery(id+"F0.wireOp",EDGE,"E10.filletArc"),sQuery(id+"F0.wireOp",EDGE,"E11.filletArc"),sQuery(id+"F0.wireOp",EDGE,"E12.filletArc"),sQuery(id+"F0.wireOp",EDGE,"E13.1.0"),sQuery(id+"F0.wireOp",EDGE,"E13.1.1"),sQuery(id+"F0.wireOp",EDGE,"E13.1.2"),sQuery(id+"F0.wireOp",EDGE,"E13.1.3"),sQuery(id+"F0.wireOp",EDGE,"E13.1.4"),sQuery(id+"F0.wireOp",EDGE,"E13.1.5"),sQuery(id+"F0.wireOp",EDGE,"E13.1.6"),sQuery(id+"F0.wireOp",EDGE,"E13.1.7"),sQuery(id+"F0.wireOp",EDGE,"E13.1.8"),sQuery(id+"F0.wireOp",EDGE,"E13.1.9"),sQuery(id+"F0.wireOp",EDGE,"E13.1.10"),sQuery(id+"F0.wireOp",EDGE,"E13.1.11"),sQuery(id+"F0.wireOp",EDGE,"E13.2.0"),sQuery(id+"F0.wireOp",EDGE,"E13.2.1"),sQuery(id+"F0.wireOp",EDGE,"E13.2.2"),sQuery(id+"F0.wireOp",EDGE,"E13.2.3"),sQuery(id+"F0.wireOp",EDGE,"E13.2.4"),sQuery(id+"F0.wireOp",EDGE,"E13.2.5"),sQuery(id+"F0.wireOp",EDGE,"E13.2.6"),sQuery(id+"F0.wireOp",EDGE,"E13.2.7"),sQuery(id+"F0.wireOp",EDGE,"E13.2.8"),sQuery(id+"F0.wireOp",EDGE,"E13.2.9"),sQuery(id+"F0.wireOp",EDGE,"E13.2.10"),sQuery(id+"F0.wireOp",EDGE,"E13.2.11"),sQuery(id+"F0.wireOp",EDGE,"E13.3.0"),sQuery(id+"F0.wireOp",EDGE,"E13.3.1"),sQuery(id+"F0.wireOp",EDGE,"E13.3.2"),sQuery(id+"F0.wireOp",EDGE,"E13.3.3"),sQuery(id+"F0.wireOp",EDGE,"E13.3.4"),sQuery(id+"F0.wireOp",EDGE,"E13.3.5"),sQuery(id+"F0.wireOp",EDGE,"E13.3.6"),sQuery(id+"F0.wireOp",EDGE,"E13.3.7"),sQuery(id+"F0.wireOp",EDGE,"E13.3.8"),sQuery(id+"F0.wireOp",EDGE,"E13.3.9"),sQuery(id+"F0.wireOp",EDGE,"E13.3.10"),sQuery(id+"F0.wireOp",EDGE,"E13.3.11"),sQuery(id+"F0.wireOp",EDGE,"E13.4.0"),sQuery(id+"F0.wireOp",EDGE,"E13.4.1"),sQuery(id+"F0.wireOp",EDGE,"E13.4.2"),sQuery(id+"F0.wireOp",EDGE,"E13.4.3"),sQuery(id+"F0.wireOp",EDGE,"E13.4.4"),sQuery(id+"F0.wireOp",EDGE,"E13.4.5"),sQuery(id+"F0.wireOp",EDGE,"E13.4.6"),sQuery(id+"F0.wireOp",EDGE,"E13.4.7"),sQuery(id+"F0.wireOp",EDGE,"E13.4.8"),sQuery(id+"F0.wireOp",EDGE,"E13.4.9"),sQuery(id+"F0.wireOp",EDGE,"E13.4.10"),sQuery(id+"F0.wireOp",EDGE,"E13.4.11"),sQuery(id+"F0.wireOp",EDGE,"E13.5.0"),sQuery(id+"F0.wireOp",EDGE,"E13.5.1"),sQuery(id+"F0.wireOp",EDGE,"E13.5.2"),sQuery(id+"F0.wireOp",EDGE,"E13.5.3"),sQuery(id+"F0.wireOp",EDGE,"E13.5.4"),sQuery(id+"F0.wireOp",EDGE,"E13.5.5"),sQuery(id+"F0.wireOp",EDGE,"E13.5.6"),sQuery(id+"F0.wireOp",EDGE,"E13.5.7"),sQuery(id+"F0.wireOp",EDGE,"E13.5.8"),sQuery(id+"F0.wireOp",EDGE,"E13.5.9"),sQuery(id+"F0.wireOp",EDGE,"E13.5.10"),sQuery(id+"F0.wireOp",EDGE,"E13.5.11"),sQuery(id+"F0.wireOp",EDGE,"E13.6.0"),sQuery(id+"F0.wireOp",EDGE,"E13.6.1"),sQuery(id+"F0.wireOp",EDGE,"E13.6.2"),sQuery(id+"F0.wireOp",EDGE,"E13.6.3"),sQuery(id+"F0.wireOp",EDGE,"E13.6.4"),sQuery(id+"F0.wireOp",EDGE,"E13.6.5"),sQuery(id+"F0.wireOp",EDGE,"E13.6.6"),sQuery(id+"F0.wireOp",EDGE,"E13.6.7"),sQuery(id+"F0.wireOp",EDGE,"E13.6.8"),sQuery(id+"F0.wireOp",EDGE,"E13.6.9"),sQuery(id+"F0.wireOp",EDGE,"E13.6.10"),sQuery(id+"F0.wireOp",EDGE,"E13.6.11"),sQuery(id+"F0.wireOp",EDGE,"E13.7.0"),sQuery(id+"F0.wireOp",EDGE,"E13.7.1"),sQuery(id+"F0.wireOp",EDGE,"E13.7.2"),sQuery(id+"F0.wireOp",EDGE,"E13.7.3"),sQuery(id+"F0.wireOp",EDGE,"E13.7.4"),sQuery(id+"F0.wireOp",EDGE,"E13.7.5"),sQuery(id+"F0.wireOp",EDGE,"E13.7.6"),sQuery(id+"F0.wireOp",EDGE,"E13.7.7"),sQuery(id+"F0.wireOp",EDGE,"E13.7.8"),sQuery(id+"F0.wireOp",EDGE,"E13.7.9"),sQuery(id+"F0.wireOp",EDGE,"E13.7.10"),sQuery(id+"F0.wireOp",EDGE,"E13.7.11"),sQuery(id+"F0.wireOp",EDGE,"E13.8.0"),sQuery(id+"F0.wireOp",EDGE,"E13.8.1"),sQuery(id+"F0.wireOp",EDGE,"E13.8.2"),sQuery(id+"F0.wireOp",EDGE,"E13.8.3"),sQuery(id+"F0.wireOp",EDGE,"E13.8.4"),sQuery(id+"F0.wireOp",EDGE,"E13.8.5"),sQuery(id+"F0.wireOp",EDGE,"E13.8.6"),sQuery(id+"F0.wireOp",EDGE,"E13.8.7"),sQuery(id+"F0.wireOp",EDGE,"E13.8.8"),sQuery(id+"F0.wireOp",EDGE,"E13.8.9"),sQuery(id+"F0.wireOp",EDGE,"E13.8.10"),sQuery(id+"F0.wireOp",EDGE,"E13.8.11"),sQuery(id+"F0.wireOp",EDGE,"E13.9.0"),sQuery(id+"F0.wireOp",EDGE,"E13.9.1"),sQuery(id+"F0.wireOp",EDGE,"E13.9.2"),sQuery(id+"F0.wireOp",EDGE,"E13.9.3"),sQuery(id+"F0.wireOp",EDGE,"E13.9.4"),sQuery(id+"F0.wireOp",EDGE,"E13.9.5"),sQuery(id+"F0.wireOp",EDGE,"E13.9.6"),sQuery(id+"F0.wireOp",EDGE,"E13.9.7"),sQuery(id+"F0.wireOp",EDGE,"E13.9.8"),sQuery(id+"F0.wireOp",EDGE,"E13.9.9"),sQuery(id+"F0.wireOp",EDGE,"E13.9.10"),sQuery(id+"F0.wireOp",EDGE,"E13.9.11"),sQuery(id+"F0.wireOp",EDGE,"E13.10.0"),sQuery(id+"F0.wireOp",EDGE,"E13.10.1"),sQuery(id+"F0.wireOp",EDGE,"E13.10.2"),sQuery(id+"F0.wireOp",EDGE,"E13.10.3"),sQuery(id+"F0.wireOp",EDGE,"E13.10.4"),sQuery(id+"F0.wireOp",EDGE,"E13.10.5"),sQuery(id+"F0.wireOp",EDGE,"E13.10.6"),sQuery(id+"F0.wireOp",EDGE,"E13.10.7"),sQuery(id+"F0.wireOp",EDGE,"E13.10.8"),sQuery(id+"F0.wireOp",EDGE,"E13.10.9"),sQuery(id+"F0.wireOp",EDGE,"E13.10.10"),sQuery(id+"F0.wireOp",EDGE,"E13.10.11"),sQuery(id+"F0.wireOp",EDGE,"E13.11.0"),sQuery(id+"F0.wireOp",EDGE,"E13.11.1"),sQuery(id+"F0.wireOp",EDGE,"E13.11.2"),sQuery(id+"F0.wireOp",EDGE,"E13.11.3"),sQuery(id+"F0.wireOp",EDGE,"E13.11.4"),sQuery(id+"F0.wireOp",EDGE,"E13.11.5"),sQuery(id+"F0.wireOp",EDGE,"E13.11.6"),sQuery(id+"F0.wireOp",EDGE,"E13.11.7"),sQuery(id+"F0.wireOp",EDGE,"E13.11.8"),sQuery(id+"F0.wireOp",EDGE,"E13.11.9"),sQuery(id+"F0.wireOp",EDGE,"E13.11.10"),sQuery(id+"F0.wireOp",EDGE,"E13.11.11"),sQuery(id+"F0.wireOp",EDGE,"E13.12.0"),sQuery(id+"F0.wireOp",EDGE,"E13.12.1"),sQuery(id+"F0.wireOp",EDGE,"E13.12.2"),sQuery(id+"F0.wireOp",EDGE,"E13.12.3"),sQuery(id+"F0.wireOp",EDGE,"E13.12.4"),sQuery(id+"F0.wireOp",EDGE,"E13.12.5"),sQuery(id+"F0.wireOp",EDGE,"E13.12.6"),sQuery(id+"F0.wireOp",EDGE,"E13.12.7"),sQuery(id+"F0.wireOp",EDGE,"E13.12.8"),sQuery(id+"F0.wireOp",EDGE,"E13.12.9"),sQuery(id+"F0.wireOp",EDGE,"E13.12.10"),sQuery(id+"F0.wireOp",EDGE,"E13.12.11"),sQuery(id+"F0.wireOp",EDGE,"E13.13.0"),sQuery(id+"F0.wireOp",EDGE,"E13.13.1"),sQuery(id+"F0.wireOp",EDGE,"E13.13.2"),sQuery(id+"F0.wireOp",EDGE,"E13.13.3"),sQuery(id+"F0.wireOp",EDGE,"E13.13.4"),sQuery(id+"F0.wireOp",EDGE,"E13.13.5"),sQuery(id+"F0.wireOp",EDGE,"E13.13.6"),sQuery(id+"F0.wireOp",EDGE,"E13.13.7"),sQuery(id+"F0.wireOp",EDGE,"E13.13.8"),sQuery(id+"F0.wireOp",EDGE,"E13.13.9"),sQuery(id+"F0.wireOp",EDGE,"E13.13.10"),sQuery(id+"F0.wireOp",EDGE,"E13.13.11"),sQuery(id+"F0.wireOp",EDGE,"E13.14.0"),sQuery(id+"F0.wireOp",EDGE,"E13.14.1"),sQuery(id+"F0.wireOp",EDGE,"E13.14.2"),sQuery(id+"F0.wireOp",EDGE,"E13.14.3"),sQuery(id+"F0.wireOp",EDGE,"E13.14.4"),sQuery(id+"F0.wireOp",EDGE,"E13.14.5"),sQuery(id+"F0.wireOp",EDGE,"E13.14.6"),sQuery(id+"F0.wireOp",EDGE,"E13.14.7"),sQuery(id+"F0.wireOp",EDGE,"E13.14.8"),sQuery(id+"F0.wireOp",EDGE,"E13.14.9"),sQuery(id+"F0.wireOp",EDGE,"E13.14.10"),sQuery(id+"F0.wireOp",EDGE,"E13.14.11"),sQuery(id+"F0.wireOp",EDGE,"E13.15.0"),sQuery(id+"F0.wireOp",EDGE,"E13.15.1"),sQuery(id+"F0.wireOp",EDGE,"E13.15.2"),sQuery(id+"F0.wireOp",EDGE,"E13.15.3"),sQuery(id+"F0.wireOp",EDGE,"E13.15.4"),sQuery(id+"F0.wireOp",EDGE,"E13.15.5"),sQuery(id+"F0.wireOp",EDGE,"E13.15.6"),sQuery(id+"F0.wireOp",EDGE,"E13.15.7"),sQuery(id+"F0.wireOp",EDGE,"E13.15.8"),sQuery(id+"F0.wireOp",EDGE,"E13.15.9"),sQuery(id+"F0.wireOp",EDGE,"E13.15.10"),sQuery(id+"F0.wireOp",EDGE,"E13.15.11"),sQuery(id+"F0.wireOp",EDGE,"E13.16.0"),sQuery(id+"F0.wireOp",EDGE,"E13.16.1"),sQuery(id+"F0.wireOp",EDGE,"E13.16.2"),sQuery(id+"F0.wireOp",EDGE,"E13.16.3"),sQuery(id+"F0.wireOp",EDGE,"E13.16.4"),sQuery(id+"F0.wireOp",EDGE,"E13.16.5"),sQuery(id+"F0.wireOp",EDGE,"E13.16.6"),sQuery(id+"F0.wireOp",EDGE,"E13.16.7"),sQuery(id+"F0.wireOp",EDGE,"E13.16.8"),sQuery(id+"F0.wireOp",EDGE,"E13.16.9"),sQuery(id+"F0.wireOp",EDGE,"E13.16.10"),sQuery(id+"F0.wireOp",EDGE,"E13.16.11"),sQuery(id+"F0.wireOp",EDGE,"E13.17.0"),sQuery(id+"F0.wireOp",EDGE,"E13.17.1"),sQuery(id+"F0.wireOp",EDGE,"E13.17.2"),sQuery(id+"F0.wireOp",EDGE,"E13.17.3"),sQuery(id+"F0.wireOp",EDGE,"E13.17.4"),sQuery(id+"F0.wireOp",EDGE,"E13.17.5"),sQuery(id+"F0.wireOp",EDGE,"E13.17.6"),sQuery(id+"F0.wireOp",EDGE,"E13.17.7"),sQuery(id+"F0.wireOp",EDGE,"E13.17.8"),sQuery(id+"F0.wireOp",EDGE,"E13.17.9"),sQuery(id+"F0.wireOp",EDGE,"E13.17.10"),sQuery(id+"F0.wireOp",EDGE,"E13.17.11"),sQuery(id+"F0.wireOp",EDGE,"E13.18.0"),sQuery(id+"F0.wireOp",EDGE,"E13.18.1"),sQuery(id+"F0.wireOp",EDGE,"E13.18.2"),sQuery(id+"F0.wireOp",EDGE,"E13.18.3"),sQuery(id+"F0.wireOp",EDGE,"E13.18.4"),sQuery(id+"F0.wireOp",EDGE,"E13.18.5"),sQuery(id+"F0.wireOp",EDGE,"E13.18.6"),sQuery(id+"F0.wireOp",EDGE,"E13.18.7"),sQuery(id+"F0.wireOp",EDGE,"E13.18.8"),sQuery(id+"F0.wireOp",EDGE,"E13.18.9"),sQuery(id+"F0.wireOp",EDGE,"E13.18.10"),sQuery(id+"F0.wireOp",EDGE,"E13.18.11"),sQuery(id+"F0.wireOp",EDGE,"E13.19.0"),sQuery(id+"F0.wireOp",EDGE,"E13.19.1"),sQuery(id+"F0.wireOp",EDGE,"E13.19.2"),sQuery(id+"F0.wireOp",EDGE,"E13.19.3"),sQuery(id+"F0.wireOp",EDGE,"E13.19.4"),sQuery(id+"F0.wireOp",EDGE,"E13.19.5"),sQuery(id+"F0.wireOp",EDGE,"E13.19.6"),sQuery(id+"F0.wireOp",EDGE,"E13.19.7"),sQuery(id+"F0.wireOp",EDGE,"E13.19.8"),sQuery(id+"F0.wireOp",EDGE,"E13.19.9"),sQuery(id+"F0.wireOp",EDGE,"E13.19.10"),sQuery(id+"F0.wireOp",EDGE,"E13.19.11"),sQuery(id+"F0.wireOp",EDGE,"E13.20.0"),sQuery(id+"F0.wireOp",EDGE,"E13.20.1"),sQuery(id+"F0.wireOp",EDGE,"E13.20.2"),sQuery(id+"F0.wireOp",EDGE,"E13.20.3"),sQuery(id+"F0.wireOp",EDGE,"E13.20.4"),sQuery(id+"F0.wireOp",EDGE,"E13.20.5"),sQuery(id+"F0.wireOp",EDGE,"E13.20.6"),sQuery(id+"F0.wireOp",EDGE,"E13.20.7"),sQuery(id+"F0.wireOp",EDGE,"E13.20.8"),sQuery(id+"F0.wireOp",EDGE,"E13.20.9"),sQuery(id+"F0.wireOp",EDGE,"E13.20.10"),sQuery(id+"F0.wireOp",EDGE,"E13.20.11"),sQuery(id+"F0.wireOp",EDGE,"E13.21.0"),sQuery(id+"F0.wireOp",EDGE,"E13.21.1"),sQuery(id+"F0.wireOp",EDGE,"E13.21.2"),sQuery(id+"F0.wireOp",EDGE,"E13.21.3"),sQuery(id+"F0.wireOp",EDGE,"E13.21.4"),sQuery(id+"F0.wireOp",EDGE,"E13.21.5"),sQuery(id+"F0.wireOp",EDGE,"E13.21.6"),sQuery(id+"F0.wireOp",EDGE,"E13.21.7"),sQuery(id+"F0.wireOp",EDGE,"E13.21.8"),sQuery(id+"F0.wireOp",EDGE,"E13.21.9"),sQuery(id+"F0.wireOp",EDGE,"E13.21.10"),sQuery(id+"F0.wireOp",EDGE,"E13.21.11"),sQuery(id+"F0.wireOp",EDGE,"E13.22.0"),sQuery(id+"F0.wireOp",EDGE,"E13.22.1"),sQuery(id+"F0.wireOp",EDGE,"E13.22.2"),sQuery(id+"F0.wireOp",EDGE,"E13.22.3"),sQuery(id+"F0.wireOp",EDGE,"E13.22.4"),sQuery(id+"F0.wireOp",EDGE,"E13.22.5"),sQuery(id+"F0.wireOp",EDGE,"E13.22.6"),sQuery(id+"F0.wireOp",EDGE,"E13.22.7"),sQuery(id+"F0.wireOp",EDGE,"E13.22.8"),sQuery(id+"F0.wireOp",EDGE,"E13.22.9"),sQuery(id+"F0.wireOp",EDGE,"E13.22.10"),sQuery(id+"F0.wireOp",EDGE,"E13.22.11"),sQuery(id+"F0.wireOp",EDGE,"E13.23.0"),sQuery(id+"F0.wireOp",EDGE,"E13.23.1"),sQuery(id+"F0.wireOp",EDGE,"E13.23.2"),sQuery(id+"F0.wireOp",EDGE,"E13.23.3"),sQuery(id+"F0.wireOp",EDGE,"E13.23.4"),sQuery(id+"F0.wireOp",EDGE,"E13.23.5"),sQuery(id+"F0.wireOp",EDGE,"E13.23.6"),sQuery(id+"F0.wireOp",EDGE,"E13.23.7"),sQuery(id+"F0.wireOp",EDGE,"E13.23.8"),sQuery(id+"F0.wireOp",EDGE,"E13.23.9"),sQuery(id+"F0.wireOp",EDGE,"E13.23.10"),sQuery(id+"F0.wireOp",EDGE,"E13.23.11"),sQuery(id+"F0.wireOp",EDGE,"E13.24.0"),sQuery(id+"F0.wireOp",EDGE,"E13.24.1"),sQuery(id+"F0.wireOp",EDGE,"E13.24.2"),sQuery(id+"F0.wireOp",EDGE,"E13.24.3"),sQuery(id+"F0.wireOp",EDGE,"E13.24.4"),sQuery(id+"F0.wireOp",EDGE,"E13.24.5"),sQuery(id+"F0.wireOp",EDGE,"E13.24.6"),sQuery(id+"F0.wireOp",EDGE,"E13.24.7"),sQuery(id+"F0.wireOp",EDGE,"E13.24.8"),sQuery(id+"F0.wireOp",EDGE,"E13.24.9"),sQuery(id+"F0.wireOp",EDGE,"E13.24.10"),sQuery(id+"F0.wireOp",EDGE,"E13.24.11"),sQuery(id+"F0.wireOp",EDGE,"E13.25.0"),sQuery(id+"F0.wireOp",EDGE,"E13.25.1"),sQuery(id+"F0.wireOp",EDGE,"E13.25.2"),sQuery(id+"F0.wireOp",EDGE,"E13.25.3"),sQuery(id+"F0.wireOp",EDGE,"E13.25.4"),sQuery(id+"F0.wireOp",EDGE,"E13.25.5"),sQuery(id+"F0.wireOp",EDGE,"E13.25.6"),sQuery(id+"F0.wireOp",EDGE,"E13.25.7"),sQuery(id+"F0.wireOp",EDGE,"E13.25.8"),sQuery(id+"F0.wireOp",EDGE,"E13.25.9"),sQuery(id+"F0.wireOp",EDGE,"E13.25.10"),sQuery(id+"F0.wireOp",EDGE,"E13.25.11"),sQuery(id+"F0.wireOp",EDGE,"E13.26.0"),sQuery(id+"F0.wireOp",EDGE,"E13.26.1"),sQuery(id+"F0.wireOp",EDGE,"E13.26.2"),sQuery(id+"F0.wireOp",EDGE,"E13.26.3"),sQuery(id+"F0.wireOp",EDGE,"E13.26.4"),sQuery(id+"F0.wireOp",EDGE,"E13.26.5"),sQuery(id+"F0.wireOp",EDGE,"E13.26.6"),sQuery(id+"F0.wireOp",EDGE,"E13.26.7"),sQuery(id+"F0.wireOp",EDGE,"E13.26.8"),sQuery(id+"F0.wireOp",EDGE,"E13.26.9"),sQuery(id+"F0.wireOp",EDGE,"E13.26.10"),sQuery(id+"F0.wireOp",EDGE,"E13.26.11"),sQuery(id+"F0.wireOp",EDGE,"E13.27.0"),sQuery(id+"F0.wireOp",EDGE,"E13.27.1"),sQuery(id+"F0.wireOp",EDGE,"E13.27.2"),sQuery(id+"F0.wireOp",EDGE,"E13.27.3"),sQuery(id+"F0.wireOp",EDGE,"E13.27.4"),sQuery(id+"F0.wireOp",EDGE,"E13.27.5"),sQuery(id+"F0.wireOp",EDGE,"E13.27.6"),sQuery(id+"F0.wireOp",EDGE,"E13.27.7"),sQuery(id+"F0.wireOp",EDGE,"E13.27.8"),sQuery(id+"F0.wireOp",EDGE,"E13.27.9"),sQuery(id+"F0.wireOp",EDGE,"E13.27.10"),sQuery(id+"F0.wireOp",EDGE,"E13.27.11"),sQuery(id+"F0.wireOp",EDGE,"E13.28.0"),sQuery(id+"F0.wireOp",EDGE,"E13.28.1"),sQuery(id+"F0.wireOp",EDGE,"E13.28.2"),sQuery(id+"F0.wireOp",EDGE,"E13.28.3"),sQuery(id+"F0.wireOp",EDGE,"E13.28.4"),sQuery(id+"F0.wireOp",EDGE,"E13.28.5"),sQuery(id+"F0.wireOp",EDGE,"E13.28.6"),sQuery(id+"F0.wireOp",EDGE,"E13.28.7"),sQuery(id+"F0.wireOp",EDGE,"E13.28.8"),sQuery(id+"F0.wireOp",EDGE,"E13.28.9"),sQuery(id+"F0.wireOp",EDGE,"E13.28.10"),sQuery(id+"F0.wireOp",EDGE,"E13.28.11"),sQuery(id+"F0.wireOp",EDGE,"E13.29.0"),sQuery(id+"F0.wireOp",EDGE,"E13.29.1"),sQuery(id+"F0.wireOp",EDGE,"E13.29.2"),sQuery(id+"F0.wireOp",EDGE,"E13.29.3"),sQuery(id+"F0.wireOp",EDGE,"E13.29.4"),sQuery(id+"F0.wireOp",EDGE,"E13.29.5"),sQuery(id+"F0.wireOp",EDGE,"E13.29.6"),sQuery(id+"F0.wireOp",EDGE,"E13.29.7"),sQuery(id+"F0.wireOp",EDGE,"E13.29.8"),sQuery(id+"F0.wireOp",EDGE,"E13.29.9"),sQuery(id+"F0.wireOp",EDGE,"E13.29.10"),sQuery(id+"F0.wireOp",EDGE,"E13.29.11"),sQuery(id+"F0.wireOp",EDGE,"E13.30.0"),sQuery(id+"F0.wireOp",EDGE,"E13.30.1"),sQuery(id+"F0.wireOp",EDGE,"E13.30.2"),sQuery(id+"F0.wireOp",EDGE,"E13.30.3"),sQuery(id+"F0.wireOp",EDGE,"E13.30.4"),sQuery(id+"F0.wireOp",EDGE,"E13.30.5"),sQuery(id+"F0.wireOp",EDGE,"E13.30.6"),sQuery(id+"F0.wireOp",EDGE,"E13.30.7"),sQuery(id+"F0.wireOp",EDGE,"E13.30.8"),sQuery(id+"F0.wireOp",EDGE,"E13.30.9"),sQuery(id+"F0.wireOp",EDGE,"E13.30.10"),sQuery(id+"F0.wireOp",EDGE,"E13.30.11"),sQuery(id+"F0.wireOp",EDGE,"E13.31.0"),sQuery(id+"F0.wireOp",EDGE,"E13.31.1"),sQuery(id+"F0.wireOp",EDGE,"E13.31.2"),sQuery(id+"F0.wireOp",EDGE,"E13.31.3"),sQuery(id+"F0.wireOp",EDGE,"E13.31.4"),sQuery(id+"F0.wireOp",EDGE,"E13.31.5"),sQuery(id+"F0.wireOp",EDGE,"E13.31.6"),sQuery(id+"F0.wireOp",EDGE,"E13.31.7"),sQuery(id+"F0.wireOp",EDGE,"E13.31.8"),sQuery(id+"F0.wireOp",EDGE,"E13.31.9"),sQuery(id+"F0.wireOp",EDGE,"E13.31.10"),sQuery(id+"F0.wireOp",EDGE,"E13.31.11"),sQuery(id+"F0.wireOp",EDGE,"E13.32.0"),sQuery(id+"F0.wireOp",EDGE,"E13.32.1"),sQuery(id+"F0.wireOp",EDGE,"E13.32.2"),sQuery(id+"F0.wireOp",EDGE,"E13.32.3"),sQuery(id+"F0.wireOp",EDGE,"E13.32.4"),sQuery(id+"F0.wireOp",EDGE,"E13.32.5"),sQuery(id+"F0.wireOp",EDGE,"E13.32.6"),sQuery(id+"F0.wireOp",EDGE,"E13.32.7"),sQuery(id+"F0.wireOp",EDGE,"E13.32.8"),sQuery(id+"F0.wireOp",EDGE,"E13.32.9"),sQuery(id+"F0.wireOp",EDGE,"E13.32.10"),sQuery(id+"F0.wireOp",EDGE,"E13.32.11"),sQuery(id+"F0.wireOp",EDGE,"E13.33.0"),sQuery(id+"F0.wireOp",EDGE,"E13.33.1"),sQuery(id+"F0.wireOp",EDGE,"E13.33.2"),sQuery(id+"F0.wireOp",EDGE,"E13.33.3"),sQuery(id+"F0.wireOp",EDGE,"E13.33.4"),sQuery(id+"F0.wireOp",EDGE,"E13.33.5"),sQuery(id+"F0.wireOp",EDGE,"E13.33.6"),sQuery(id+"F0.wireOp",EDGE,"E13.33.7"),sQuery(id+"F0.wireOp",EDGE,"E13.33.8"),sQuery(id+"F0.wireOp",EDGE,"E13.33.9"),sQuery(id+"F0.wireOp",EDGE,"E13.33.10"),sQuery(id+"F0.wireOp",EDGE,"E13.33.11"),sQuery(id+"F0.wireOp",EDGE,"E13.34.0"),sQuery(id+"F0.wireOp",EDGE,"E13.34.1"),sQuery(id+"F0.wireOp",EDGE,"E13.34.2"),sQuery(id+"F0.wireOp",EDGE,"E13.34.3"),sQuery(id+"F0.wireOp",EDGE,"E13.34.4"),sQuery(id+"F0.wireOp",EDGE,"E13.34.5"),sQuery(id+"F0.wireOp",EDGE,"E13.34.6"),sQuery(id+"F0.wireOp",EDGE,"E13.34.7"),sQuery(id+"F0.wireOp",EDGE,"E13.34.8"),sQuery(id+"F0.wireOp",EDGE,"E13.34.9"),sQuery(id+"F0.wireOp",EDGE,"E13.34.10"),sQuery(id+"F0.wireOp",EDGE,"E13.34.11"),sQuery(id+"F0.wireOp",EDGE,"E13.35.0"),sQuery(id+"F0.wireOp",EDGE,"E13.35.1"),sQuery(id+"F0.wireOp",EDGE,"E13.35.2"),sQuery(id+"F0.wireOp",EDGE,"E13.35.3"),sQuery(id+"F0.wireOp",EDGE,"E13.35.4"),sQuery(id+"F0.wireOp",EDGE,"E13.35.5"),sQuery(id+"F0.wireOp",EDGE,"E13.35.6"),sQuery(id+"F0.wireOp",EDGE,"E13.35.7"),sQuery(id+"F0.wireOp",EDGE,"E13.35.8"),sQuery(id+"F0.wireOp",EDGE,"E13.35.9"),sQuery(id+"F0.wireOp",EDGE,"E13.35.10"),sQuery(id+"F0.wireOp",EDGE,"E13.35.11"),sQuery(id+"F0.wireOp",EDGE,"E13.36.0"),sQuery(id+"F0.wireOp",EDGE,"E13.36.1"),sQuery(id+"F0.wireOp",EDGE,"E13.36.2"),sQuery(id+"F0.wireOp",EDGE,"E13.36.3"),sQuery(id+"F0.wireOp",EDGE,"E13.36.4"),sQuery(id+"F0.wireOp",EDGE,"E13.36.5"),sQuery(id+"F0.wireOp",EDGE,"E13.36.6"),sQuery(id+"F0.wireOp",EDGE,"E13.36.7"),sQuery(id+"F0.wireOp",EDGE,"E13.36.8"),sQuery(id+"F0.wireOp",EDGE,"E13.36.9"),sQuery(id+"F0.wireOp",EDGE,"E13.36.10"),sQuery(id+"F0.wireOp",EDGE,"E13.36.11"),sQuery(id+"F0.wireOp",EDGE,"E13.37.0"),sQuery(id+"F0.wireOp",EDGE,"E13.37.1"),sQuery(id+"F0.wireOp",EDGE,"E13.37.2"),sQuery(id+"F0.wireOp",EDGE,"E13.37.3"),sQuery(id+"F0.wireOp",EDGE,"E13.37.4"),sQuery(id+"F0.wireOp",EDGE,"E13.37.5"),sQuery(id+"F0.wireOp",EDGE,"E13.37.6"),sQuery(id+"F0.wireOp",EDGE,"E13.37.7"),sQuery(id+"F0.wireOp",EDGE,"E13.37.8"),sQuery(id+"F0.wireOp",EDGE,"E13.37.9"),sQuery(id+"F0.wireOp",EDGE,"E13.37.10"),sQuery(id+"F0.wireOp",EDGE,"E13.37.11"),sQuery(id+"F0.wireOp",EDGE,"E13.38.0"),sQuery(id+"F0.wireOp",EDGE,"E13.38.1"),sQuery(id+"F0.wireOp",EDGE,"E13.38.2"),sQuery(id+"F0.wireOp",EDGE,"E13.38.3"),sQuery(id+"F0.wireOp",EDGE,"E13.38.4"),sQuery(id+"F0.wireOp",EDGE,"E13.38.5"),sQuery(id+"F0.wireOp",EDGE,"E13.38.6"),sQuery(id+"F0.wireOp",EDGE,"E13.38.7"),sQuery(id+"F0.wireOp",EDGE,"E13.38.8"),sQuery(id+"F0.wireOp",EDGE,"E13.38.9"),sQuery(id+"F0.wireOp",EDGE,"E13.38.10"),sQuery(id+"F0.wireOp",EDGE,"E13.38.11"),sQuery(id+"F0.wireOp",EDGE,"E13.39.0"),sQuery(id+"F0.wireOp",EDGE,"E13.39.1"),sQuery(id+"F0.wireOp",EDGE,"E13.39.2"),sQuery(id+"F0.wireOp",EDGE,"E13.39.3"),sQuery(id+"F0.wireOp",EDGE,"E13.39.4"),sQuery(id+"F0.wireOp",EDGE,"E13.39.5"),sQuery(id+"F0.wireOp",EDGE,"E13.39.6"),sQuery(id+"F0.wireOp",EDGE,"E13.39.7"),sQuery(id+"F0.wireOp",EDGE,"E13.39.8"),sQuery(id+"F0.wireOp",EDGE,"E13.39.9"),sQuery(id+"F0.wireOp",EDGE,"E13.39.10"),sQuery(id+"F0.wireOp",EDGE,"E13.39.11"),sQuery(id+"F0.wireOp",EDGE,"E13.40.0"),sQuery(id+"F0.wireOp",EDGE,"E13.40.1"),sQuery(id+"F0.wireOp",EDGE,"E13.40.2"),sQuery(id+"F0.wireOp",EDGE,"E13.40.3"),sQuery(id+"F0.wireOp",EDGE,"E13.40.4"),sQuery(id+"F0.wireOp",EDGE,"E13.40.5"),sQuery(id+"F0.wireOp",EDGE,"E13.40.6"),sQuery(id+"F0.wireOp",EDGE,"E13.40.7"),sQuery(id+"F0.wireOp",EDGE,"E13.40.8"),sQuery(id+"F0.wireOp",EDGE,"E13.40.9"),sQuery(id+"F0.wireOp",EDGE,"E13.40.10"),sQuery(id+"F0.wireOp",EDGE,"E13.40.11"),sQuery(id+"F0.wireOp",EDGE,"E13.41.0"),sQuery(id+"F0.wireOp",EDGE,"E13.41.1"),sQuery(id+"F0.wireOp",EDGE,"E13.41.2"),sQuery(id+"F0.wireOp",EDGE,"E13.41.3"),sQuery(id+"F0.wireOp",EDGE,"E13.41.4"),sQuery(id+"F0.wireOp",EDGE,"E13.41.5"),sQuery(id+"F0.wireOp",EDGE,"E13.41.6"),sQuery(id+"F0.wireOp",EDGE,"E13.41.7"),sQuery(id+"F0.wireOp",EDGE,"E13.41.8"),sQuery(id+"F0.wireOp",EDGE,"E13.41.9"),sQuery(id+"F0.wireOp",EDGE,"E13.41.10"),sQuery(id+"F0.wireOp",EDGE,"E13.41.11"),sQuery(id+"F0.wireOp",EDGE,"E13.42.0"),sQuery(id+"F0.wireOp",EDGE,"E13.42.1"),sQuery(id+"F0.wireOp",EDGE,"E13.42.2"),sQuery(id+"F0.wireOp",EDGE,"E13.42.3"),sQuery(id+"F0.wireOp",EDGE,"E13.42.4"),sQuery(id+"F0.wireOp",EDGE,"E13.42.5"),sQuery(id+"F0.wireOp",EDGE,"E13.42.6"),sQuery(id+"F0.wireOp",EDGE,"E13.42.7"),sQuery(id+"F0.wireOp",EDGE,"E13.42.8"),sQuery(id+"F0.wireOp",EDGE,"E13.42.9"),sQuery(id+"F0.wireOp",EDGE,"E13.42.10"),sQuery(id+"F0.wireOp",EDGE,"E13.42.11"),sQuery(id+"F0.wireOp",EDGE,"E13.43.0"),sQuery(id+"F0.wireOp",EDGE,"E13.43.1"),sQuery(id+"F0.wireOp",EDGE,"E13.43.2"),sQuery(id+"F0.wireOp",EDGE,"E13.43.3"),sQuery(id+"F0.wireOp",EDGE,"E13.43.4"),sQuery(id+"F0.wireOp",EDGE,"E13.43.5"),sQuery(id+"F0.wireOp",EDGE,"E13.43.6"),sQuery(id+"F0.wireOp",EDGE,"E13.43.7"),sQuery(id+"F0.wireOp",EDGE,"E13.43.8"),sQuery(id+"F0.wireOp",EDGE,"E13.43.9"),sQuery(id+"F0.wireOp",EDGE,"E13.43.10"),sQuery(id+"F0.wireOp",EDGE,"E13.43.11"),sQuery(id+"F0.wireOp",EDGE,"E13.44.0"),sQuery(id+"F0.wireOp",EDGE,"E13.44.1"),sQuery(id+"F0.wireOp",EDGE,"E13.44.2"),sQuery(id+"F0.wireOp",EDGE,"E13.44.3"),sQuery(id+"F0.wireOp",EDGE,"E13.44.4"),sQuery(id+"F0.wireOp",EDGE,"E13.44.5"),sQuery(id+"F0.wireOp",EDGE,"E13.44.6"),sQuery(id+"F0.wireOp",EDGE,"E13.44.7"),sQuery(id+"F0.wireOp",EDGE,"E13.44.8"),sQuery(id+"F0.wireOp",EDGE,"E13.44.9"),sQuery(id+"F0.wireOp",EDGE,"E13.44.10"),sQuery(id+"F0.wireOp",EDGE,"E13.44.11"),sQuery(id+"F0.wireOp",EDGE,"E13.45.0"),sQuery(id+"F0.wireOp",EDGE,"E13.45.1"),sQuery(id+"F0.wireOp",EDGE,"E13.45.2"),sQuery(id+"F0.wireOp",EDGE,"E13.45.3"),sQuery(id+"F0.wireOp",EDGE,"E13.45.4"),sQuery(id+"F0.wireOp",EDGE,"E13.45.5"),sQuery(id+"F0.wireOp",EDGE,"E13.45.6"),sQuery(id+"F0.wireOp",EDGE,"E13.45.7"),sQuery(id+"F0.wireOp",EDGE,"E13.45.8"),sQuery(id+"F0.wireOp",EDGE,"E13.45.9"),sQuery(id+"F0.wireOp",EDGE,"E13.45.10"),sQuery(id+"F0.wireOp",EDGE,"E13.45.11"),sQuery(id+"F0.wireOp",EDGE,"E13.46.0"),sQuery(id+"F0.wireOp",EDGE,"E13.46.1"),sQuery(id+"F0.wireOp",EDGE,"E13.46.2"),sQuery(id+"F0.wireOp",EDGE,"E13.46.3"),sQuery(id+"F0.wireOp",EDGE,"E13.46.4"),sQuery(id+"F0.wireOp",EDGE,"E13.46.5"),sQuery(id+"F0.wireOp",EDGE,"E13.46.6"),sQuery(id+"F0.wireOp",EDGE,"E13.46.7"),sQuery(id+"F0.wireOp",EDGE,"E13.46.8"),sQuery(id+"F0.wireOp",EDGE,"E13.46.9"),sQuery(id+"F0.wireOp",EDGE,"E13.46.10"),sQuery(id+"F0.wireOp",EDGE,"E13.46.11"),sQuery(id+"F0.wireOp",EDGE,"E13.47.0"),sQuery(id+"F0.wireOp",EDGE,"E13.47.1"),sQuery(id+"F0.wireOp",EDGE,"E13.47.2"),sQuery(id+"F0.wireOp",EDGE,"E13.47.3"),sQuery(id+"F0.wireOp",EDGE,"E13.47.4"),sQuery(id+"F0.wireOp",EDGE,"E13.47.5"),sQuery(id+"F0.wireOp",EDGE,"E13.47.6"),sQuery(id+"F0.wireOp",EDGE,"E13.47.7"),sQuery(id+"F0.wireOp",EDGE,"E13.47.8"),sQuery(id+"F0.wireOp",EDGE,"E13.47.9"),sQuery(id+"F0.wireOp",EDGE,"E13.47.10"),sQuery(id+"F0.wireOp",EDGE,"E13.47.11"),sQuery(id+"F0.wireOp",EDGE,"E13.48.0"),sQuery(id+"F0.wireOp",EDGE,"E13.48.1"),sQuery(id+"F0.wireOp",EDGE,"E13.48.2"),sQuery(id+"F0.wireOp",EDGE,"E13.48.3"),sQuery(id+"F0.wireOp",EDGE,"E13.48.4"),sQuery(id+"F0.wireOp",EDGE,"E13.48.5"),sQuery(id+"F0.wireOp",EDGE,"E13.48.6"),sQuery(id+"F0.wireOp",EDGE,"E13.48.7"),sQuery(id+"F0.wireOp",EDGE,"E13.48.8"),sQuery(id+"F0.wireOp",EDGE,"E13.48.9"),sQuery(id+"F0.wireOp",EDGE,"E13.48.10"),sQuery(id+"F0.wireOp",EDGE,"E13.48.11"),sQuery(id+"F0.wireOp",EDGE,"E13.49.0"),sQuery(id+"F0.wireOp",EDGE,"E13.49.1"),sQuery(id+"F0.wireOp",EDGE,"E13.49.2"),sQuery(id+"F0.wireOp",EDGE,"E13.49.3"),sQuery(id+"F0.wireOp",EDGE,"E13.49.4"),sQuery(id+"F0.wireOp",EDGE,"E13.49.5"),sQuery(id+"F0.wireOp",EDGE,"E13.49.6"),sQuery(id+"F0.wireOp",EDGE,"E13.49.7"),sQuery(id+"F0.wireOp",EDGE,"E13.49.8"),sQuery(id+"F0.wireOp",EDGE,"E13.49.9"),sQuery(id+"F0.wireOp",EDGE,"E13.49.10"),sQuery(id+"F0.wireOp",EDGE,"E13.49.11"),sQuery(id+"F0.wireOp",EDGE,"E13.50.0"),sQuery(id+"F0.wireOp",EDGE,"E13.50.1"),sQuery(id+"F0.wireOp",EDGE,"E13.50.2"),sQuery(id+"F0.wireOp",EDGE,"E13.50.3"),sQuery(id+"F0.wireOp",EDGE,"E13.50.4"),sQuery(id+"F0.wireOp",EDGE,"E13.50.5"),sQuery(id+"F0.wireOp",EDGE,"E13.50.6"),sQuery(id+"F0.wireOp",EDGE,"E13.50.7"),sQuery(id+"F0.wireOp",EDGE,"E13.50.8"),sQuery(id+"F0.wireOp",EDGE,"E13.50.9"),sQuery(id+"F0.wireOp",EDGE,"E13.50.10"),sQuery(id+"F0.wireOp",EDGE,"E13.50.11"),sQuery(id+"F0.wireOp",EDGE,"E13.51.0"),sQuery(id+"F0.wireOp",EDGE,"E13.51.1"),sQuery(id+"F0.wireOp",EDGE,"E13.51.2"),sQuery(id+"F0.wireOp",EDGE,"E13.51.3"),sQuery(id+"F0.wireOp",EDGE,"E13.51.4"),sQuery(id+"F0.wireOp",EDGE,"E13.51.5"),sQuery(id+"F0.wireOp",EDGE,"E13.51.6"),sQuery(id+"F0.wireOp",EDGE,"E13.51.7"),sQuery(id+"F0.wireOp",EDGE,"E13.51.8"),sQuery(id+"F0.wireOp",EDGE,"E13.51.9"),sQuery(id+"F0.wireOp",EDGE,"E13.51.10"),sQuery(id+"F0.wireOp",EDGE,"E13.51.11"),sQuery(id+"F0.wireOp",EDGE,"E13.52.0"),sQuery(id+"F0.wireOp",EDGE,"E13.52.1"),sQuery(id+"F0.wireOp",EDGE,"E13.52.2"),sQuery(id+"F0.wireOp",EDGE,"E13.52.3"),sQuery(id+"F0.wireOp",EDGE,"E13.52.4"),sQuery(id+"F0.wireOp",EDGE,"E13.52.5"),sQuery(id+"F0.wireOp",EDGE,"E13.52.6"),sQuery(id+"F0.wireOp",EDGE,"E13.52.7"),sQuery(id+"F0.wireOp",EDGE,"E13.52.8"),sQuery(id+"F0.wireOp",EDGE,"E13.52.9"),sQuery(id+"F0.wireOp",EDGE,"E13.52.10"),sQuery(id+"F0.wireOp",EDGE,"E13.52.11"),sQuery(id+"F0.wireOp",EDGE,"E13.53.0"),sQuery(id+"F0.wireOp",EDGE,"E13.53.1"),sQuery(id+"F0.wireOp",EDGE,"E13.53.2"),sQuery(id+"F0.wireOp",EDGE,"E13.53.3"),sQuery(id+"F0.wireOp",EDGE,"E13.53.4"),sQuery(id+"F0.wireOp",EDGE,"E13.53.5"),sQuery(id+"F0.wireOp",EDGE,"E13.53.6"),sQuery(id+"F0.wireOp",EDGE,"E13.53.7"),sQuery(id+"F0.wireOp",EDGE,"E13.53.8"),sQuery(id+"F0.wireOp",EDGE,"E13.53.9"),sQuery(id+"F0.wireOp",EDGE,"E13.53.10"),sQuery(id+"F0.wireOp",EDGE,"E13.53.11"),sQuery(id+"F0.wireOp",EDGE,"E13.54.0"),sQuery(id+"F0.wireOp",EDGE,"E13.54.1"),sQuery(id+"F0.wireOp",EDGE,"E13.54.2"),sQuery(id+"F0.wireOp",EDGE,"E13.54.3"),sQuery(id+"F0.wireOp",EDGE,"E13.54.4"),sQuery(id+"F0.wireOp",EDGE,"E13.54.5"),sQuery(id+"F0.wireOp",EDGE,"E13.54.6"),sQuery(id+"F0.wireOp",EDGE,"E13.54.7"),sQuery(id+"F0.wireOp",EDGE,"E13.54.8"),sQuery(id+"F0.wireOp",EDGE,"E13.54.9"),sQuery(id+"F0.wireOp",EDGE,"E13.54.10"),sQuery(id+"F0.wireOp",EDGE,"E13.54.11"),sQuery(id+"F0.wireOp",EDGE,"E13.55.0"),sQuery(id+"F0.wireOp",EDGE,"E13.55.1"),sQuery(id+"F0.wireOp",EDGE,"E13.55.2"),sQuery(id+"F0.wireOp",EDGE,"E13.55.3"),sQuery(id+"F0.wireOp",EDGE,"E13.55.4"),sQuery(id+"F0.wireOp",EDGE,"E13.55.5"),sQuery(id+"F0.wireOp",EDGE,"E13.55.6"),sQuery(id+"F0.wireOp",EDGE,"E13.55.7"),sQuery(id+"F0.wireOp",EDGE,"E13.55.8"),sQuery(id+"F0.wireOp",EDGE,"E13.55.9"),sQuery(id+"F0.wireOp",EDGE,"E13.55.10"),sQuery(id+"F0.wireOp",EDGE,"E13.55.11"),sQuery(id+"F0.wireOp",EDGE,"E13.56.0"),sQuery(id+"F0.wireOp",EDGE,"E13.56.1"),sQuery(id+"F0.wireOp",EDGE,"E13.56.2"),sQuery(id+"F0.wireOp",EDGE,"E13.56.3"),sQuery(id+"F0.wireOp",EDGE,"E13.56.4"),sQuery(id+"F0.wireOp",EDGE,"E13.56.5"),sQuery(id+"F0.wireOp",EDGE,"E13.56.6"),sQuery(id+"F0.wireOp",EDGE,"E13.56.7"),sQuery(id+"F0.wireOp",EDGE,"E13.56.8"),sQuery(id+"F0.wireOp",EDGE,"E13.56.9"),sQuery(id+"F0.wireOp",EDGE,"E13.56.10"),sQuery(id+"F0.wireOp",EDGE,"E13.56.11"),sQuery(id+"F0.wireOp",EDGE,"E13.57.0"),sQuery(id+"F0.wireOp",EDGE,"E13.57.1"),sQuery(id+"F0.wireOp",EDGE,"E13.57.2"),sQuery(id+"F0.wireOp",EDGE,"E13.57.3"),sQuery(id+"F0.wireOp",EDGE,"E13.57.4"),sQuery(id+"F0.wireOp",EDGE,"E13.57.5"),sQuery(id+"F0.wireOp",EDGE,"E13.57.6"),sQuery(id+"F0.wireOp",EDGE,"E13.57.7"),sQuery(id+"F0.wireOp",EDGE,"E13.57.8"),sQuery(id+"F0.wireOp",EDGE,"E13.57.9"),sQuery(id+"F0.wireOp",EDGE,"E13.57.10"),sQuery(id+"F0.wireOp",EDGE,"E13.57.11"),sQuery(id+"F0.wireOp",EDGE,"E13.58.0"),sQuery(id+"F0.wireOp",EDGE,"E13.58.1"),sQuery(id+"F0.wireOp",EDGE,"E13.58.2"),sQuery(id+"F0.wireOp",EDGE,"E13.58.3"),sQuery(id+"F0.wireOp",EDGE,"E13.58.4"),sQuery(id+"F0.wireOp",EDGE,"E13.58.5"),sQuery(id+"F0.wireOp",EDGE,"E13.58.6"),sQuery(id+"F0.wireOp",EDGE,"E13.58.7"),sQuery(id+"F0.wireOp",EDGE,"E13.58.8"),sQuery(id+"F0.wireOp",EDGE,"E13.58.9"),sQuery(id+"F0.wireOp",EDGE,"E13.58.10"),sQuery(id+"F0.wireOp",EDGE,"E13.58.11"),sQuery(id+"F0.wireOp",EDGE,"E13.59.0"),sQuery(id+"F0.wireOp",EDGE,"E13.59.1"),sQuery(id+"F0.wireOp",EDGE,"E13.59.2"),sQuery(id+"F0.wireOp",EDGE,"E13.59.3"),sQuery(id+"F0.wireOp",EDGE,"E13.59.4"),sQuery(id+"F0.wireOp",EDGE,"E13.59.5"),sQuery(id+"F0.wireOp",EDGE,"E13.59.6"),sQuery(id+"F0.wireOp",EDGE,"E13.59.7"),sQuery(id+"F0.wireOp",EDGE,"E13.59.8"),sQuery(id+"F0.wireOp",EDGE,"E13.59.9"),sQuery(id+"F0.wireOp",EDGE,"E13.59.10"),sQuery(id+"F0.wireOp",EDGE,"E13.59.11"),sQuery(id+"F0.wireOp",EDGE,"E13.60.0"),sQuery(id+"F0.wireOp",EDGE,"E13.60.1"),sQuery(id+"F0.wireOp",EDGE,"E13.60.2"),sQuery(id+"F0.wireOp",EDGE,"E13.60.3"),sQuery(id+"F0.wireOp",EDGE,"E13.60.4"),sQuery(id+"F0.wireOp",EDGE,"E13.60.5"),sQuery(id+"F0.wireOp",EDGE,"E13.60.6"),sQuery(id+"F0.wireOp",EDGE,"E13.60.7"),sQuery(id+"F0.wireOp",EDGE,"E13.60.8"),sQuery(id+"F0.wireOp",EDGE,"E13.60.9"),sQuery(id+"F0.wireOp",EDGE,"E13.60.10"),sQuery(id+"F0.wireOp",EDGE,"E13.60.11"),sQuery(id+"F0.wireOp",EDGE,"E13.61.0"),sQuery(id+"F0.wireOp",EDGE,"E13.61.1"),sQuery(id+"F0.wireOp",EDGE,"E13.61.2"),sQuery(id+"F0.wireOp",EDGE,"E13.61.3"),sQuery(id+"F0.wireOp",EDGE,"E13.61.4"),sQuery(id+"F0.wireOp",EDGE,"E13.61.5"),sQuery(id+"F0.wireOp",EDGE,"E13.61.6"),sQuery(id+"F0.wireOp",EDGE,"E13.61.7"),sQuery(id+"F0.wireOp",EDGE,"E13.61.8"),sQuery(id+"F0.wireOp",EDGE,"E13.61.9"),sQuery(id+"F0.wireOp",EDGE,"E13.61.10"),sQuery(id+"F0.wireOp",EDGE,"E13.61.11"),sQuery(id+"F0.wireOp",EDGE,"E13.62.0"),sQuery(id+"F0.wireOp",EDGE,"E13.62.1"),sQuery(id+"F0.wireOp",EDGE,"E13.62.2"),sQuery(id+"F0.wireOp",EDGE,"E13.62.3"),sQuery(id+"F0.wireOp",EDGE,"E13.62.4"),sQuery(id+"F0.wireOp",EDGE,"E13.62.5"),sQuery(id+"F0.wireOp",EDGE,"E13.62.6"),sQuery(id+"F0.wireOp",EDGE,"E13.62.7"),sQuery(id+"F0.wireOp",EDGE,"E13.62.8"),sQuery(id+"F0.wireOp",EDGE,"E13.62.9"),sQuery(id+"F0.wireOp",EDGE,"E13.62.10"),sQuery(id+"F0.wireOp",EDGE,"E13.62.11"),sQuery(id+"F0.wireOp",EDGE,"E13.63.0"),sQuery(id+"F0.wireOp",EDGE,"E13.63.1"),sQuery(id+"F0.wireOp",EDGE,"E13.63.2"),sQuery(id+"F0.wireOp",EDGE,"E13.63.3"),sQuery(id+"F0.wireOp",EDGE,"E13.63.4"),sQuery(id+"F0.wireOp",EDGE,"E13.63.5"),sQuery(id+"F0.wireOp",EDGE,"E13.63.6"),sQuery(id+"F0.wireOp",EDGE,"E13.63.7"),sQuery(id+"F0.wireOp",EDGE,"E13.63.8"),sQuery(id+"F0.wireOp",EDGE,"E13.63.9"),sQuery(id+"F0.wireOp",EDGE,"E13.63.10"),sQuery(id+"F0.wireOp",EDGE,"E13.63.11"),sQuery(id+"F0.wireOp",EDGE,"E13.64.0"),sQuery(id+"F0.wireOp",EDGE,"E13.64.1"),sQuery(id+"F0.wireOp",EDGE,"E13.64.2"),sQuery(id+"F0.wireOp",EDGE,"E13.64.3"),sQuery(id+"F0.wireOp",EDGE,"E13.64.4"),sQuery(id+"F0.wireOp",EDGE,"E13.64.5"),sQuery(id+"F0.wireOp",EDGE,"E13.64.6"),sQuery(id+"F0.wireOp",EDGE,"E13.64.7"),sQuery(id+"F0.wireOp",EDGE,"E13.64.8"),sQuery(id+"F0.wireOp",EDGE,"E13.64.9"),sQuery(id+"F0.wireOp",EDGE,"E13.64.10"),sQuery(id+"F0.wireOp",EDGE,"E13.64.11"),sQuery(id+"F0.wireOp",EDGE,"E13.65.0"),sQuery(id+"F0.wireOp",EDGE,"E13.65.1"),sQuery(id+"F0.wireOp",EDGE,"E13.65.2"),sQuery(id+"F0.wireOp",EDGE,"E13.65.3"),sQuery(id+"F0.wireOp",EDGE,"E13.65.4"),sQuery(id+"F0.wireOp",EDGE,"E13.65.5"),sQuery(id+"F0.wireOp",EDGE,"E13.65.6"),sQuery(id+"F0.wireOp",EDGE,"E13.65.7"),sQuery(id+"F0.wireOp",EDGE,"E13.65.8"),sQuery(id+"F0.wireOp",EDGE,"E13.65.9"),sQuery(id+"F0.wireOp",EDGE,"E13.65.10"),sQuery(id+"F0.wireOp",EDGE,"E13.65.11"),sQuery(id+"F0.wireOp",EDGE,"E13.66.0"),sQuery(id+"F0.wireOp",EDGE,"E13.66.1"),sQuery(id+"F0.wireOp",EDGE,"E13.66.2"),sQuery(id+"F0.wireOp",EDGE,"E13.66.3"),sQuery(id+"F0.wireOp",EDGE,"E13.66.4"),sQuery(id+"F0.wireOp",EDGE,"E13.66.5"),sQuery(id+"F0.wireOp",EDGE,"E13.66.6"),sQuery(id+"F0.wireOp",EDGE,"E13.66.7"),sQuery(id+"F0.wireOp",EDGE,"E13.66.8"),sQuery(id+"F0.wireOp",EDGE,"E13.66.9"),sQuery(id+"F0.wireOp",EDGE,"E13.66.10"),sQuery(id+"F0.wireOp",EDGE,"E13.66.11"),sQuery(id+"F0.wireOp",EDGE,"E13.67.0"),sQuery(id+"F0.wireOp",EDGE,"E13.67.1"),sQuery(id+"F0.wireOp",EDGE,"E13.67.2"),sQuery(id+"F0.wireOp",EDGE,"E13.67.3"),sQuery(id+"F0.wireOp",EDGE,"E13.67.4"),sQuery(id+"F0.wireOp",EDGE,"E13.67.5"),sQuery(id+"F0.wireOp",EDGE,"E13.67.6"),sQuery(id+"F0.wireOp",EDGE,"E13.67.7"),sQuery(id+"F0.wireOp",EDGE,"E13.67.8"),sQuery(id+"F0.wireOp",EDGE,"E13.67.9"),sQuery(id+"F0.wireOp",EDGE,"E13.67.10"),sQuery(id+"F0.wireOp",EDGE,"E13.67.11"),sQuery(id+"F0.wireOp",EDGE,"E13.68.0"),sQuery(id+"F0.wireOp",EDGE,"E13.68.1"),sQuery(id+"F0.wireOp",EDGE,"E13.68.2"),sQuery(id+"F0.wireOp",EDGE,"E13.68.3"),sQuery(id+"F0.wireOp",EDGE,"E13.68.4"),sQuery(id+"F0.wireOp",EDGE,"E13.68.5"),sQuery(id+"F0.wireOp",EDGE,"E13.68.6"),sQuery(id+"F0.wireOp",EDGE,"E13.68.7"),sQuery(id+"F0.wireOp",EDGE,"E13.68.8"),sQuery(id+"F0.wireOp",EDGE,"E13.68.9"),sQuery(id+"F0.wireOp",EDGE,"E13.68.10"),sQuery(id+"F0.wireOp",EDGE,"E13.68.11"),sQuery(id+"F0.wireOp",EDGE,"E13.69.0"),sQuery(id+"F0.wireOp",EDGE,"E13.69.1"),sQuery(id+"F0.wireOp",EDGE,"E13.69.2"),sQuery(id+"F0.wireOp",EDGE,"E13.69.3"),sQuery(id+"F0.wireOp",EDGE,"E13.69.4"),sQuery(id+"F0.wireOp",EDGE,"E13.69.5"),sQuery(id+"F0.wireOp",EDGE,"E13.69.6"),sQuery(id+"F0.wireOp",EDGE,"E13.69.7"),sQuery(id+"F0.wireOp",EDGE,"E13.69.8"),sQuery(id+"F0.wireOp",EDGE,"E13.69.9"),sQuery(id+"F0.wireOp",EDGE,"E13.69.10"),sQuery(id+"F0.wireOp",EDGE,"E13.69.11"),sQuery(id+"F0.wireOp",EDGE,"E13.70.0"),sQuery(id+"F0.wireOp",EDGE,"E13.70.1"),sQuery(id+"F0.wireOp",EDGE,"E13.70.2"),sQuery(id+"F0.wireOp",EDGE,"E13.70.3"),sQuery(id+"F0.wireOp",EDGE,"E13.70.4"),sQuery(id+"F0.wireOp",EDGE,"E13.70.5"),sQuery(id+"F0.wireOp",EDGE,"E13.70.6"),sQuery(id+"F0.wireOp",EDGE,"E13.70.7"),sQuery(id+"F0.wireOp",EDGE,"E13.70.8"),sQuery(id+"F0.wireOp",EDGE,"E13.70.9"),sQuery(id+"F0.wireOp",EDGE,"E13.70.10"),sQuery(id+"F0.wireOp",EDGE,"E13.70.11"),sQuery(id+"F0.wireOp",EDGE,"E13.71.0"),sQuery(id+"F0.wireOp",EDGE,"E13.71.1"),sQuery(id+"F0.wireOp",EDGE,"E13.71.2"),sQuery(id+"F0.wireOp",EDGE,"E13.71.3"),sQuery(id+"F0.wireOp",EDGE,"E13.71.4"),sQuery(id+"F0.wireOp",EDGE,"E13.71.5"),sQuery(id+"F0.wireOp",EDGE,"E13.71.6"),sQuery(id+"F0.wireOp",EDGE,"E13.71.7"),sQuery(id+"F0.wireOp",EDGE,"E13.71.8"),sQuery(id+"F0.wireOp",EDGE,"E13.71.9"),sQuery(id+"F0.wireOp",EDGE,"E13.71.10"),sQuery(id+"F0.wireOp",EDGE,"E13.71.11"),sQuery(id+"F0.wireOp",EDGE,"E14.trimOffspring"),sQuery(id+"F0.wireOp",EDGE,"E15.trimOffspring"),sQuery(id+"F0.wireOp",EDGE,"E16.trimOffspring"),sQuery(id+"F0.wireOp",EDGE,"E17.trimOffspring"),sQuery(id+"F0.wireOp",EDGE,"E18.trimOffspring"),sQuery(id+"F0.wireOp",EDGE,"E19.trimOffspring"),sQuery(id+"F0.wireOp",EDGE,"E20.trimOffspring"),sQuery(id+"F0.wireOp",EDGE,"E21.trimOffspring"),sQuery(id+"F0.wireOp",EDGE,"E22.trimOffspring"),sQuery(id+"F0.wireOp",EDGE,"E23.trimOffspring"),sQuery(id+"F0.wireOp",EDGE,"E24.trimOffspring"),sQuery(id+"F0.wireOp",EDGE,"E25.trimOffspring"),sQuery(id+"F0.wireOp",EDGE,"E26.trimOffspring"),sQuery(id+"F0.wireOp",EDGE,"E27.trimOffspring"),sQuery(id+"F0.wireOp",EDGE,"E28.trimOffspring"),sQuery(id+"F0.wireOp",EDGE,"E29.trimOffspring"),sQuery(id+"F0.wireOp",EDGE,"E30.trimOffspring"),sQuery(id+"F0.wireOp",EDGE,"E31.trimOffspring"),sQuery(id+"F0.wireOp",EDGE,"E32.trimOffspring"),sQuery(id+"F0.wireOp",EDGE,"E33.trimOffspring"),sQuery(id+"F0.wireOp",EDGE,"E34.trimOffspring"),sQuery(id+"F0.wireOp",EDGE,"E35.trimOffspring"),sQuery(id+"F0.wireOp",EDGE,"E36.trimOffspring"),sQuery(id+"F0.wireOp",EDGE,"E37.trimOffspring"),sQuery(id+"F0.wireOp",EDGE,"E38.trimOffspring"),sQuery(id+"F0.wireOp",EDGE,"E39.trimOffspring"),sQuery(id+"F0.wireOp",EDGE,"E40.trimOffspring"),sQuery(id+"F0.wireOp",EDGE,"E41.trimOffspring"),sQuery(id+"F0.wireOp",EDGE,"E42.trimOffspring"),sQuery(id+"F0.wireOp",EDGE,"E43.trimOffspring"),sQuery(id+"F0.wireOp",EDGE,"E44.trimOffspring"),sQuery(id+"F0.wireOp",EDGE,"E45.trimOffspring"),sQuery(id+"F0.wireOp",EDGE,"E46.trimOffspring"),sQuery(id+"F0.wireOp",EDGE,"E47.trimOffspring"),sQuery(id+"F0.wireOp",EDGE,"E48.trimOffspring"),sQuery(id+"F0.wireOp",EDGE,"E49.trimOffspring"),sQuery(id+"F0.wireOp",EDGE,"E50.trimOffspring"),sQuery(id+"F0.wireOp",EDGE,"E51.trimOffspring"),sQuery(id+"F0.wireOp",EDGE,"E52.trimOffspring"),sQuery(id+"F0.wireOp",EDGE,"E53.trimOffspring"),sQuery(id+"F0.wireOp",EDGE,"E54.trimOffspring"),sQuery(id+"F0.wireOp",EDGE,"E55.trimOffspring"),sQuery(id+"F0.wireOp",EDGE,"E56.trimOffspring"),sQuery(id+"F0.wireOp",EDGE,"E57.trimOffspring"),sQuery(id+"F0.wireOp",EDGE,"E58.trimOffspring"),sQuery(id+"F0.wireOp",EDGE,"E59.trimOffspring"),sQuery(id+"F0.wireOp",EDGE,"E60.trimOffspring"),sQuery(id+"F0.wireOp",EDGE,"E61.trimOffspring"),sQuery(id+"F0.wireOp",EDGE,"E62.trimOffspring"),sQuery(id+"F0.wireOp",EDGE,"E63.trimOffspring"),sQuery(id+"F0.wireOp",EDGE,"E64.trimOffspring"),sQuery(id+"F0.wireOp",EDGE,"E65.trimOffspring"),sQuery(id+"F0.wireOp",EDGE,"E66.trimOffspring"),sQuery(id+"F0.wireOp",EDGE,"E67.trimOffspring"),sQuery(id+"F0.wireOp",EDGE,"E68.trimOffspring"),sQuery(id+"F0.wireOp",EDGE,"E69.trimOffspring"),sQuery(id+"F0.wireOp",EDGE,"E70.trimOffspring"),sQuery(id+"F0.wireOp",EDGE,"E71.trimOffspring"),sQuery(id+"F0.wireOp",EDGE,"E72.trimOffspring"),sQuery(id+"F0.wireOp",EDGE,"E73.trimOffspring"),sQuery(id+"F0.wireOp",EDGE,"E74.trimOffspring"),sQuery(id+"F0.wireOp",EDGE,"E75.trimOffspring"),sQuery(id+"F0.wireOp",EDGE,"E76.trimOffspring"),sQuery(id+"F0.wireOp",EDGE,"E77.trimOffspring"),sQuery(id+"F0.wireOp",EDGE,"E78.trimOffspring"),sQuery(id+"F0.wireOp",EDGE,"E79.trimOffspring"),sQuery(id+"F0.wireOp",EDGE,"E80.trimOffspring"),sQuery(id+"F0.wireOp",EDGE,"E81.trimOffspring"),sQuery(id+"F0.wireOp",EDGE,"E82.trimOffspring"),sQuery(id+"F0.wireOp",EDGE,"E83.trimOffspring"),sQuery(id+"F0.wireOp",EDGE,"E84.trimOffspring")])],"isStart":false});
            var sketch = newSketch(context, id + "F3", { "sketchPlane" : qUnion([Q0])});
            skPoint(sketch, "E86", {"position": v(0, 0) * mm});
            skCircle(sketch, "E87", {"center": v(0, 0) * mm, "radius": 3.18 * mm});
            skPoint(sketch, "E88", {"position": v(0, 50.8) * mm});
            skPoint(sketch, "E89.1.0", {"position": v(-66.1, -34.79) * mm});
            skPoint(sketch, "E89.2.0", {"position": v(29.81, -55.74) * mm});
            skCircle(sketch, "E90", {"center": v(0, 50.8) * mm, "radius": 3.18 * mm});
            skCircle(sketch, "E91.1.0", {"center": v(-44, -25.4) * mm, "radius": 3.18 * mm});
            skCircle(sketch, "E91.2.0", {"center": v(44, -25.4) * mm, "radius": 3.18 * mm});
            skSolve(sketch);
        }
        {
            var Q0;
            Q0=makeQuery(id+"F3.imprint","IMPRINT",FACE,{"disambiguationData":[TD([[makeQuery(id+"F3.imprint","IMPRINT",EDGE,{"derivedFrom":sQuery(id+"F3.wireOp",EDGE,"E87")}),1.0]])]});
            var Q1;
            Q1=makeQuery(id+"F3.imprint","IMPRINT",FACE,{"disambiguationData":[TD([[makeQuery(id+"F3.imprint","IMPRINT",EDGE,{"derivedFrom":sQuery(id+"F3.wireOp",EDGE,"E90")}),1.0]])]});
            var Q2;
            Q2=makeQuery(id+"F3.imprint","IMPRINT",FACE,{"disambiguationData":[TD([[makeQuery(id+"F3.imprint","IMPRINT",EDGE,{"derivedFrom":sQuery(id+"F3.wireOp",EDGE,"E91.2.0")}),1.0]])]});
            var Q3;
            Q3=makeQuery(id+"F3.imprint","IMPRINT",FACE,{"disambiguationData":[TD([[makeQuery(id+"F3.imprint","IMPRINT",EDGE,{"derivedFrom":sQuery(id+"F3.wireOp",EDGE,"E91.1.0")}),1.0]])]});
            extrude(context, id + "F4", {"entities" : qUnion([Q0, Q1, Q2, Q3]), "operationType" : NewBodyOperationType.ADD, "depth" : 10.16 * mm});
        }
    });
